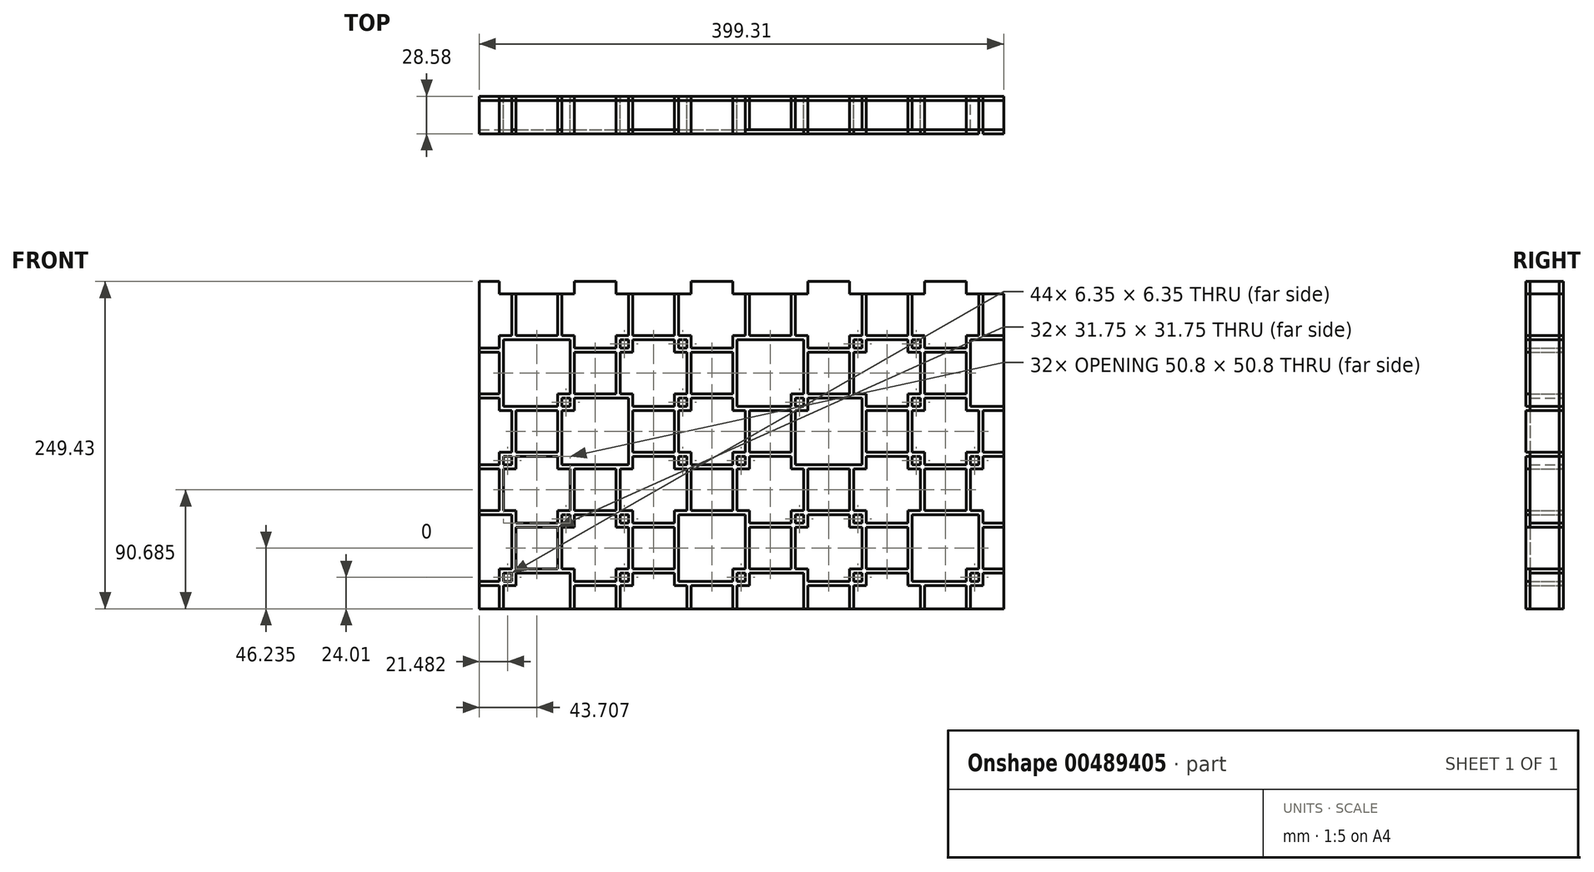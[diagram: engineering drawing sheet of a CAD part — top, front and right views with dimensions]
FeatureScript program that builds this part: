
annotation { "Feature Type Name" : "Feature", "Feature Type Description" : "" }
export const myFeature = defineFeature(function(context is Context, id is Id, definition is map)
    precondition{}
    {
        {
            var Q0;
            Q0=qCreatedBy(makeId("Front.planeOp"),FACE);
            var sketch = newSketch(context, id + "F0", { "sketchPlane" : qUnion([Q0])});
            skLineSegment(sketch, "E0.top", {"start": v(-283.74, 148.71) * mm, "end": v(-268.6, 148.71) * mm});
            skLineSegment(sketch, "E0.right", {"start": v(-259.08, 173.7) * mm, "end": v(-259.08, 158.24) * mm});
            skLineSegment(sketch, "E1.bottom", {"start": v(-265.43, 155.06) * mm, "end": v(-214.63, 155.06) * mm});
            skLineSegment(sketch, "E1.top", {"start": v(-265.43, 104.26) * mm, "end": v(-214.63, 104.26) * mm});
            skLineSegment(sketch, "E1.left", {"start": v(-265.43, 155.06) * mm, "end": v(-265.43, 104.26) * mm});
            skLineSegment(sketch, "E1.right", {"start": v(-214.63, 155.06) * mm, "end": v(-214.63, 104.26) * mm});
            skLineSegment(sketch, "E2.2", {"start": v(-283.74, 145.54) * mm, "end": v(-268.6, 145.54) * mm});
            skLineSegment(sketch, "E2.3", {"start": v(-255.9, 173.7) * mm, "end": v(-255.9, 158.24) * mm});
            skLineSegment(sketch, "E3.0", {"start": v(-268.6, 158.24) * mm, "end": v(-211.46, 158.24) * mm});
            skLineSegment(sketch, "E3.1", {"start": v(-268.6, 158.24) * mm, "end": v(-268.6, 101.09) * mm});
            skLineSegment(sketch, "E3.2", {"start": v(-268.6, 101.09) * mm, "end": v(-211.46, 101.09) * mm});
            skLineSegment(sketch, "E3.3", {"start": v(-211.46, 158.24) * mm, "end": v(-211.46, 101.09) * mm});
            skLineSegment(sketch, "E4.0.1.0", {"start": v(-268.6, 12.19) * mm, "end": v(-224.16, 12.19) * mm});
            skLineSegment(sketch, "E4.0.1.1", {"start": v(-268.6, 69.34) * mm, "end": v(-211.46, 69.34) * mm});
            skLineSegment(sketch, "E4.0.1.2", {"start": v(-265.43, 66.16) * mm, "end": v(-214.63, 66.16) * mm});
            skLineSegment(sketch, "E4.0.1.3", {"start": v(-283.74, 113.79) * mm, "end": v(-268.6, 113.79) * mm});
            skLineSegment(sketch, "E4.0.1.4", {"start": v(-214.63, 66.16) * mm, "end": v(-214.63, 24.89) * mm});
            skLineSegment(sketch, "E4.0.1.5", {"start": v(-265.43, 66.16) * mm, "end": v(-265.43, 15.36) * mm});
            skLineSegment(sketch, "E4.0.1.6", {"start": v(-265.43, 15.36) * mm, "end": v(-224.16, 15.36) * mm});
            skLineSegment(sketch, "E4.0.1.7", {"start": v(-259.08, 101.09) * mm, "end": v(-259.08, 69.34) * mm});
            skLineSegment(sketch, "E4.0.1.9", {"start": v(-283.74, 59.81) * mm, "end": v(-268.6, 59.81) * mm});
            skLineSegment(sketch, "E4.0.1.10", {"start": v(-283.74, 110.61) * mm, "end": v(-268.6, 110.61) * mm});
            skLineSegment(sketch, "E4.0.1.11", {"start": v(-211.46, 69.34) * mm, "end": v(-211.46, 24.89) * mm});
            skLineSegment(sketch, "E4.0.1.13", {"start": v(-268.6, 69.34) * mm, "end": v(-268.6, 12.19) * mm});
            skLineSegment(sketch, "E4.0.1.14", {"start": v(-283.74, 56.64) * mm, "end": v(-268.6, 56.64) * mm});
            skLineSegment(sketch, "E4.0.1.15", {"start": v(-255.9, 101.09) * mm, "end": v(-255.9, 69.34) * mm});
            skLineSegment(sketch, "E4.0.2.0", {"start": v(-255.9, -76.71) * mm, "end": v(-211.46, -76.71) * mm});
            skLineSegment(sketch, "E4.0.2.1", {"start": v(-268.6, -19.56) * mm, "end": v(-224.16, -19.56) * mm});
            skLineSegment(sketch, "E4.0.2.2", {"start": v(-265.43, -22.74) * mm, "end": v(-224.16, -22.74) * mm});
            skLineSegment(sketch, "E4.0.2.4", {"start": v(-214.63, -32.26) * mm, "end": v(-214.63, -73.54) * mm});
            skLineSegment(sketch, "E4.0.2.5", {"start": v(-265.43, -22.74) * mm, "end": v(-265.43, -64.01) * mm});
            skLineSegment(sketch, "E4.0.2.6", {"start": v(-255.9, -73.54) * mm, "end": v(-214.63, -73.54) * mm});
            skLineSegment(sketch, "E4.0.2.7", {"start": v(-259.08, 12.19) * mm, "end": v(-259.08, -29.09) * mm});
            skLineSegment(sketch, "E4.0.2.9", {"start": v(-283.74, -29.09) * mm, "end": v(-259.08, -29.09) * mm});
            skLineSegment(sketch, "E4.0.2.10", {"start": v(-283.74, 21.71) * mm, "end": v(-268.6, 21.71) * mm});
            skLineSegment(sketch, "E4.0.2.11", {"start": v(-211.46, -32.26) * mm, "end": v(-211.46, -76.71) * mm});
            skLineSegment(sketch, "E4.0.2.13", {"start": v(-268.6, -19.56) * mm, "end": v(-268.6, -32.26) * mm});
            skLineSegment(sketch, "E4.0.2.14", {"start": v(-283.74, -32.26) * mm, "end": v(-255.9, -32.26) * mm});
            skLineSegment(sketch, "E4.0.2.15", {"start": v(-255.9, 12.19) * mm, "end": v(-255.9, -32.26) * mm});
            skLineSegment(sketch, "E4.0.3.1", {"start": v(-268.6, -108.46) * mm, "end": v(-211.46, -108.46) * mm});
            skLineSegment(sketch, "E4.0.3.2", {"start": v(-265.43, -111.64) * mm, "end": v(-214.63, -111.64) * mm});
            skLineSegment(sketch, "E4.0.3.3", {"start": v(-283.74, -64.01) * mm, "end": v(-255.9, -64.01) * mm});
            skLineSegment(sketch, "E4.0.3.4", {"start": v(-214.63, -111.64) * mm, "end": v(-214.63, -138.82) * mm});
            skLineSegment(sketch, "E4.0.3.5", {"start": v(-265.43, -111.64) * mm, "end": v(-265.43, -138.82) * mm});
            skLineSegment(sketch, "E4.0.3.7", {"start": v(-259.08, -67.19) * mm, "end": v(-259.08, -108.46) * mm});
            skLineSegment(sketch, "E4.0.3.9", {"start": v(-283.74, -117.99) * mm, "end": v(-268.6, -117.99) * mm});
            skLineSegment(sketch, "E4.0.3.10", {"start": v(-283.74, -67.19) * mm, "end": v(-259.08, -67.19) * mm});
            skLineSegment(sketch, "E4.0.3.11", {"start": v(-211.46, -108.46) * mm, "end": v(-211.46, -138.82) * mm});
            skLineSegment(sketch, "E4.0.3.13", {"start": v(-268.6, -108.46) * mm, "end": v(-268.6, -138.82) * mm});
            skLineSegment(sketch, "E4.0.3.14", {"start": v(-283.74, -121.16) * mm, "end": v(-268.6, -121.16) * mm});
            skLineSegment(sketch, "E4.0.3.15", {"start": v(-255.9, -64.01) * mm, "end": v(-255.9, -108.46) * mm});
            skLineSegment(sketch, "E4.1.0.0", {"start": v(-179.7, 101.09) * mm, "end": v(-122.56, 101.09) * mm});
            skLineSegment(sketch, "E4.1.0.1", {"start": v(-179.7, 158.24) * mm, "end": v(-170.18, 158.24) * mm});
            skLineSegment(sketch, "E4.1.0.2", {"start": v(-176.53, 155.06) * mm, "end": v(-125.73, 155.06) * mm});
            skLineSegment(sketch, "E4.1.0.4", {"start": v(-125.73, 155.06) * mm, "end": v(-125.73, 104.26) * mm});
            skLineSegment(sketch, "E4.1.0.5", {"start": v(-176.53, 155.06) * mm, "end": v(-176.53, 148.71) * mm});
            skLineSegment(sketch, "E4.1.0.6", {"start": v(-176.53, 104.26) * mm, "end": v(-125.73, 104.26) * mm});
            skLineSegment(sketch, "E4.1.0.7", {"start": v(-170.18, 173.7) * mm, "end": v(-170.18, 158.24) * mm});
            skLineSegment(sketch, "E4.1.0.8", {"start": v(-220.98, 173.7) * mm, "end": v(-220.98, 158.24) * mm});
            skLineSegment(sketch, "E4.1.0.9", {"start": v(-211.46, 148.71) * mm, "end": v(-179.7, 148.71) * mm});
            skLineSegment(sketch, "E4.1.0.11", {"start": v(-122.56, 158.24) * mm, "end": v(-122.56, 101.09) * mm});
            skLineSegment(sketch, "E4.1.0.12", {"start": v(-224.16, 173.7) * mm, "end": v(-224.16, 158.24) * mm});
            skLineSegment(sketch, "E4.1.0.13", {"start": v(-179.7, 158.24) * mm, "end": v(-179.7, 148.71) * mm});
            skLineSegment(sketch, "E4.1.0.14", {"start": v(-211.46, 145.54) * mm, "end": v(-179.7, 145.54) * mm});
            skLineSegment(sketch, "E4.1.0.15", {"start": v(-167, 173.7) * mm, "end": v(-167, 158.24) * mm});
            skLineSegment(sketch, "E4.1.1.0", {"start": v(-167, 12.19) * mm, "end": v(-122.56, 12.19) * mm});
            skLineSegment(sketch, "E4.1.1.1", {"start": v(-179.7, 69.34) * mm, "end": v(-122.56, 69.34) * mm});
            skLineSegment(sketch, "E4.1.1.2", {"start": v(-176.53, 66.16) * mm, "end": v(-125.73, 66.16) * mm});
            skLineSegment(sketch, "E4.1.1.3", {"start": v(-211.46, 113.79) * mm, "end": v(-179.7, 113.79) * mm});
            skLineSegment(sketch, "E4.1.1.4", {"start": v(-125.73, 66.16) * mm, "end": v(-125.73, 15.36) * mm});
            skLineSegment(sketch, "E4.1.1.5", {"start": v(-176.53, 66.16) * mm, "end": v(-176.53, 24.89) * mm});
            skLineSegment(sketch, "E4.1.1.6", {"start": v(-167, 15.36) * mm, "end": v(-125.73, 15.36) * mm});
            skLineSegment(sketch, "E4.1.1.7", {"start": v(-170.18, 101.09) * mm, "end": v(-170.18, 59.81) * mm});
            skLineSegment(sketch, "E4.1.1.8", {"start": v(-220.98, 101.09) * mm, "end": v(-220.98, 69.34) * mm});
            skLineSegment(sketch, "E4.1.1.9", {"start": v(-211.46, 59.81) * mm, "end": v(-170.18, 59.81) * mm});
            skLineSegment(sketch, "E4.1.1.10", {"start": v(-211.46, 110.61) * mm, "end": v(-179.7, 110.61) * mm});
            skLineSegment(sketch, "E4.1.1.11", {"start": v(-122.56, 69.34) * mm, "end": v(-122.56, 12.19) * mm});
            skLineSegment(sketch, "E4.1.1.12", {"start": v(-224.16, 101.09) * mm, "end": v(-224.16, 69.34) * mm});
            skLineSegment(sketch, "E4.1.1.13", {"start": v(-179.7, 69.34) * mm, "end": v(-179.7, 24.89) * mm});
            skLineSegment(sketch, "E4.1.1.14", {"start": v(-211.46, 56.64) * mm, "end": v(-167, 56.64) * mm});
            skLineSegment(sketch, "E4.1.1.15", {"start": v(-167, 101.09) * mm, "end": v(-167, 56.64) * mm});
            skLineSegment(sketch, "E4.1.2.0", {"start": v(-179.7, -76.71) * mm, "end": v(-167, -76.71) * mm});
            skLineSegment(sketch, "E4.1.2.1", {"start": v(-167, -19.56) * mm, "end": v(-122.56, -19.56) * mm});
            skLineSegment(sketch, "E4.1.2.2", {"start": v(-167, -22.74) * mm, "end": v(-125.73, -22.74) * mm});
            skLineSegment(sketch, "E4.1.2.3", {"start": v(-224.16, 24.89) * mm, "end": v(-167, 24.89) * mm});
            skLineSegment(sketch, "E4.1.2.4", {"start": v(-125.73, -22.74) * mm, "end": v(-125.73, -64.01) * mm});
            skLineSegment(sketch, "E4.1.2.6", {"start": v(-176.53, -73.54) * mm, "end": v(-167, -73.54) * mm});
            skLineSegment(sketch, "E4.1.2.7", {"start": v(-170.18, 21.71) * mm, "end": v(-170.18, -29.09) * mm});
            skLineSegment(sketch, "E4.1.2.8", {"start": v(-220.98, 21.71) * mm, "end": v(-220.98, -29.09) * mm});
            skLineSegment(sketch, "E4.1.2.9", {"start": v(-220.98, -29.09) * mm, "end": v(-170.18, -29.09) * mm});
            skLineSegment(sketch, "E4.1.2.10", {"start": v(-220.98, 21.71) * mm, "end": v(-170.18, 21.71) * mm});
            skLineSegment(sketch, "E4.1.2.11", {"start": v(-122.56, -19.56) * mm, "end": v(-122.56, -64.01) * mm});
            skLineSegment(sketch, "E4.1.2.12", {"start": v(-224.16, 24.89) * mm, "end": v(-224.16, -32.26) * mm});
            skLineSegment(sketch, "E4.1.2.13", {"start": v(-179.7, -32.26) * mm, "end": v(-179.7, -76.71) * mm});
            skLineSegment(sketch, "E4.1.2.14", {"start": v(-224.16, -32.26) * mm, "end": v(-167, -32.26) * mm});
            skLineSegment(sketch, "E4.1.2.15", {"start": v(-167, 24.89) * mm, "end": v(-167, -32.26) * mm});
            skLineSegment(sketch, "E4.1.3.1", {"start": v(-179.7, -108.46) * mm, "end": v(-135.26, -108.46) * mm});
            skLineSegment(sketch, "E4.1.3.2", {"start": v(-176.53, -111.64) * mm, "end": v(-135.26, -111.64) * mm});
            skLineSegment(sketch, "E4.1.3.3", {"start": v(-224.16, -64.01) * mm, "end": v(-167, -64.01) * mm});
            skLineSegment(sketch, "E4.1.3.4", {"start": v(-125.73, -121.16) * mm, "end": v(-125.73, -138.82) * mm});
            skLineSegment(sketch, "E4.1.3.5", {"start": v(-176.53, -111.64) * mm, "end": v(-176.53, -138.82) * mm});
            skLineSegment(sketch, "E4.1.3.7", {"start": v(-170.18, -67.19) * mm, "end": v(-170.18, -117.99) * mm});
            skLineSegment(sketch, "E4.1.3.8", {"start": v(-220.98, -67.19) * mm, "end": v(-220.98, -108.46) * mm});
            skLineSegment(sketch, "E4.1.3.9", {"start": v(-211.46, -117.99) * mm, "end": v(-170.18, -117.99) * mm});
            skLineSegment(sketch, "E4.1.3.10", {"start": v(-220.98, -67.19) * mm, "end": v(-170.18, -67.19) * mm});
            skLineSegment(sketch, "E4.1.3.11", {"start": v(-122.56, -121.16) * mm, "end": v(-122.56, -138.82) * mm});
            skLineSegment(sketch, "E4.1.3.12", {"start": v(-224.16, -64.01) * mm, "end": v(-224.16, -108.46) * mm});
            skLineSegment(sketch, "E4.1.3.13", {"start": v(-179.7, -108.46) * mm, "end": v(-179.7, -138.82) * mm});
            skLineSegment(sketch, "E4.1.3.14", {"start": v(-211.46, -121.16) * mm, "end": v(-167, -121.16) * mm});
            skLineSegment(sketch, "E4.1.3.15", {"start": v(-167, -64.01) * mm, "end": v(-167, -121.16) * mm});
            skLineSegment(sketch, "E4.2.0.0", {"start": v(-90.8, 101.09) * mm, "end": v(-33.66, 101.09) * mm});
            skLineSegment(sketch, "E4.2.0.1", {"start": v(-90.8, 158.24) * mm, "end": v(-33.66, 158.24) * mm});
            skLineSegment(sketch, "E4.2.0.2", {"start": v(-87.63, 155.06) * mm, "end": v(-36.83, 155.06) * mm});
            skLineSegment(sketch, "E4.2.0.4", {"start": v(-36.83, 155.06) * mm, "end": v(-36.83, 104.26) * mm});
            skLineSegment(sketch, "E4.2.0.5", {"start": v(-87.63, 155.06) * mm, "end": v(-87.63, 104.26) * mm});
            skLineSegment(sketch, "E4.2.0.6", {"start": v(-87.63, 104.26) * mm, "end": v(-36.83, 104.26) * mm});
            skLineSegment(sketch, "E4.2.0.7", {"start": v(-81.28, 173.7) * mm, "end": v(-81.28, 158.24) * mm});
            skLineSegment(sketch, "E4.2.0.8", {"start": v(-132.08, 173.7) * mm, "end": v(-132.08, 158.24) * mm});
            skLineSegment(sketch, "E4.2.0.9", {"start": v(-122.56, 148.71) * mm, "end": v(-90.8, 148.71) * mm});
            skLineSegment(sketch, "E4.2.0.11", {"start": v(-33.66, 158.24) * mm, "end": v(-33.66, 101.09) * mm});
            skLineSegment(sketch, "E4.2.0.12", {"start": v(-135.26, 173.7) * mm, "end": v(-135.26, 158.24) * mm});
            skLineSegment(sketch, "E4.2.0.13", {"start": v(-90.8, 158.24) * mm, "end": v(-90.8, 101.09) * mm});
            skLineSegment(sketch, "E4.2.0.14", {"start": v(-122.56, 145.54) * mm, "end": v(-90.8, 145.54) * mm});
            skLineSegment(sketch, "E4.2.0.15", {"start": v(-78.1, 173.7) * mm, "end": v(-78.1, 158.24) * mm});
            skLineSegment(sketch, "E4.2.1.0", {"start": v(-90.8, 12.19) * mm, "end": v(-46.36, 12.19) * mm});
            skLineSegment(sketch, "E4.2.1.1", {"start": v(-90.8, 69.34) * mm, "end": v(-33.66, 69.34) * mm});
            skLineSegment(sketch, "E4.2.1.2", {"start": v(-87.63, 66.16) * mm, "end": v(-36.83, 66.16) * mm});
            skLineSegment(sketch, "E4.2.1.3", {"start": v(-122.56, 113.79) * mm, "end": v(-90.8, 113.79) * mm});
            skLineSegment(sketch, "E4.2.1.4", {"start": v(-36.83, 66.16) * mm, "end": v(-36.83, 24.89) * mm});
            skLineSegment(sketch, "E4.2.1.5", {"start": v(-87.63, 66.16) * mm, "end": v(-87.63, 15.36) * mm});
            skLineSegment(sketch, "E4.2.1.6", {"start": v(-87.63, 15.36) * mm, "end": v(-46.36, 15.36) * mm});
            skLineSegment(sketch, "E4.2.1.7", {"start": v(-81.28, 101.09) * mm, "end": v(-81.28, 69.34) * mm});
            skLineSegment(sketch, "E4.2.1.8", {"start": v(-132.08, 101.09) * mm, "end": v(-132.08, 59.81) * mm});
            skLineSegment(sketch, "E4.2.1.9", {"start": v(-132.08, 59.81) * mm, "end": v(-90.8, 59.81) * mm});
            skLineSegment(sketch, "E4.2.1.10", {"start": v(-122.56, 110.61) * mm, "end": v(-90.8, 110.61) * mm});
            skLineSegment(sketch, "E4.2.1.11", {"start": v(-33.66, 69.34) * mm, "end": v(-33.66, 24.89) * mm});
            skLineSegment(sketch, "E4.2.1.12", {"start": v(-135.26, 101.09) * mm, "end": v(-135.26, 56.64) * mm});
            skLineSegment(sketch, "E4.2.1.13", {"start": v(-90.8, 69.34) * mm, "end": v(-90.8, 12.19) * mm});
            skLineSegment(sketch, "E4.2.1.14", {"start": v(-135.26, 56.64) * mm, "end": v(-90.8, 56.64) * mm});
            skLineSegment(sketch, "E4.2.1.15", {"start": v(-78.1, 101.09) * mm, "end": v(-78.1, 69.34) * mm});
            skLineSegment(sketch, "E4.2.2.1", {"start": v(-90.8, -19.56) * mm, "end": v(-46.36, -19.56) * mm});
            skLineSegment(sketch, "E4.2.2.2", {"start": v(-87.63, -22.74) * mm, "end": v(-46.36, -22.74) * mm});
            skLineSegment(sketch, "E4.2.2.3", {"start": v(-135.26, 24.89) * mm, "end": v(-90.8, 24.89) * mm});
            skLineSegment(sketch, "E4.2.2.5", {"start": v(-87.63, -22.74) * mm, "end": v(-87.63, -64.01) * mm});
            skLineSegment(sketch, "E4.2.2.7", {"start": v(-81.28, 12.19) * mm, "end": v(-81.28, -29.09) * mm});
            skLineSegment(sketch, "E4.2.2.8", {"start": v(-132.08, 21.71) * mm, "end": v(-132.08, -29.09) * mm});
            skLineSegment(sketch, "E4.2.2.9", {"start": v(-132.08, -29.09) * mm, "end": v(-81.28, -29.09) * mm});
            skLineSegment(sketch, "E4.2.2.10", {"start": v(-132.08, 21.71) * mm, "end": v(-90.8, 21.71) * mm});
            skLineSegment(sketch, "E4.2.2.12", {"start": v(-135.26, 24.89) * mm, "end": v(-135.26, -32.26) * mm});
            skLineSegment(sketch, "E4.2.2.13", {"start": v(-90.8, -19.56) * mm, "end": v(-90.8, -64.01) * mm});
            skLineSegment(sketch, "E4.2.2.14", {"start": v(-135.26, -32.26) * mm, "end": v(-78.1, -32.26) * mm});
            skLineSegment(sketch, "E4.2.2.15", {"start": v(-78.1, 12.19) * mm, "end": v(-78.1, -32.26) * mm});
            skLineSegment(sketch, "E4.2.3.1", {"start": v(-90.8, -108.46) * mm, "end": v(-33.66, -108.46) * mm});
            skLineSegment(sketch, "E4.2.3.2", {"start": v(-87.63, -111.64) * mm, "end": v(-36.83, -111.64) * mm});
            skLineSegment(sketch, "E4.2.3.3", {"start": v(-135.26, -64.01) * mm, "end": v(-78.1, -64.01) * mm});
            skLineSegment(sketch, "E4.2.3.4", {"start": v(-36.83, -111.64) * mm, "end": v(-36.83, -138.82) * mm});
            skLineSegment(sketch, "E4.2.3.5", {"start": v(-87.63, -111.64) * mm, "end": v(-87.63, -138.82) * mm});
            skLineSegment(sketch, "E4.2.3.7", {"start": v(-81.28, -67.19) * mm, "end": v(-81.28, -108.46) * mm});
            skLineSegment(sketch, "E4.2.3.8", {"start": v(-132.08, -67.19) * mm, "end": v(-132.08, -117.99) * mm});
            skLineSegment(sketch, "E4.2.3.9", {"start": v(-132.08, -117.99) * mm, "end": v(-90.8, -117.99) * mm});
            skLineSegment(sketch, "E4.2.3.10", {"start": v(-132.08, -67.19) * mm, "end": v(-81.28, -67.19) * mm});
            skLineSegment(sketch, "E4.2.3.11", {"start": v(-33.66, -108.46) * mm, "end": v(-33.66, -138.82) * mm});
            skLineSegment(sketch, "E4.2.3.12", {"start": v(-135.26, -64.01) * mm, "end": v(-135.26, -121.16) * mm});
            skLineSegment(sketch, "E4.2.3.13", {"start": v(-90.8, -108.46) * mm, "end": v(-90.8, -138.82) * mm});
            skLineSegment(sketch, "E4.2.3.14", {"start": v(-135.26, -121.16) * mm, "end": v(-90.8, -121.16) * mm});
            skLineSegment(sketch, "E4.2.3.15", {"start": v(-78.1, -64.01) * mm, "end": v(-78.1, -108.46) * mm});
            skLineSegment(sketch, "E4.3.0.0", {"start": v(-1.9, 101.09) * mm, "end": v(55.24, 101.09) * mm});
            skLineSegment(sketch, "E4.3.0.1", {"start": v(-1.9, 158.24) * mm, "end": v(55.24, 158.24) * mm});
            skLineSegment(sketch, "E4.3.0.2", {"start": v(1.27, 155.06) * mm, "end": v(52.07, 155.06) * mm});
            skLineSegment(sketch, "E4.3.0.4", {"start": v(52.07, 155.06) * mm, "end": v(52.07, 104.26) * mm});
            skLineSegment(sketch, "E4.3.0.5", {"start": v(1.27, 155.06) * mm, "end": v(1.27, 104.26) * mm});
            skLineSegment(sketch, "E4.3.0.6", {"start": v(1.27, 104.26) * mm, "end": v(52.07, 104.26) * mm});
            skLineSegment(sketch, "E4.3.0.7", {"start": v(7.62, 173.7) * mm, "end": v(7.62, 158.24) * mm});
            skLineSegment(sketch, "E4.3.0.8", {"start": v(-43.18, 173.7) * mm, "end": v(-43.18, 158.24) * mm});
            skLineSegment(sketch, "E4.3.0.9", {"start": v(-33.66, 148.71) * mm, "end": v(-1.9, 148.71) * mm});
            skLineSegment(sketch, "E4.3.0.11", {"start": v(55.24, 158.24) * mm, "end": v(55.24, 101.09) * mm});
            skLineSegment(sketch, "E4.3.0.12", {"start": v(-46.36, 173.7) * mm, "end": v(-46.36, 158.24) * mm});
            skLineSegment(sketch, "E4.3.0.13", {"start": v(-1.9, 158.24) * mm, "end": v(-1.9, 101.09) * mm});
            skLineSegment(sketch, "E4.3.0.14", {"start": v(-33.66, 145.54) * mm, "end": v(-1.9, 145.54) * mm});
            skLineSegment(sketch, "E4.3.0.15", {"start": v(10.8, 173.7) * mm, "end": v(10.8, 158.24) * mm});
            skLineSegment(sketch, "E4.3.1.0", {"start": v(10.8, 12.19) * mm, "end": v(55.24, 12.19) * mm});
            skLineSegment(sketch, "E4.3.1.1", {"start": v(-1.9, 69.34) * mm, "end": v(55.24, 69.34) * mm});
            skLineSegment(sketch, "E4.3.1.2", {"start": v(1.27, 66.16) * mm, "end": v(52.07, 66.16) * mm});
            skLineSegment(sketch, "E4.3.1.3", {"start": v(-33.66, 113.79) * mm, "end": v(-1.9, 113.79) * mm});
            skLineSegment(sketch, "E4.3.1.4", {"start": v(52.07, 66.16) * mm, "end": v(52.07, 15.36) * mm});
            skLineSegment(sketch, "E4.3.1.5", {"start": v(1.27, 66.16) * mm, "end": v(1.27, 24.89) * mm});
            skLineSegment(sketch, "E4.3.1.6", {"start": v(10.8, 15.36) * mm, "end": v(52.07, 15.36) * mm});
            skLineSegment(sketch, "E4.3.1.8", {"start": v(-43.18, 101.09) * mm, "end": v(-43.18, 69.34) * mm});
            skLineSegment(sketch, "E4.3.1.10", {"start": v(-33.66, 110.61) * mm, "end": v(-1.9, 110.61) * mm});
            skLineSegment(sketch, "E4.3.1.11", {"start": v(55.24, 69.34) * mm, "end": v(55.24, 12.19) * mm});
            skLineSegment(sketch, "E4.3.1.12", {"start": v(-46.36, 101.09) * mm, "end": v(-46.36, 69.34) * mm});
            skLineSegment(sketch, "E4.3.1.13", {"start": v(-1.9, 69.34) * mm, "end": v(-1.9, 24.89) * mm});
            skLineSegment(sketch, "E4.3.2.0", {"start": v(-1.9, -76.71) * mm, "end": v(42.54, -76.71) * mm});
            skLineSegment(sketch, "E4.3.2.3", {"start": v(-46.36, 24.89) * mm, "end": v(-36.83, 24.89) * mm});
            skLineSegment(sketch, "E4.3.2.4", {"start": v(52.07, -22.74) * mm, "end": v(52.07, -64.01) * mm});
            skLineSegment(sketch, "E4.3.2.5", {"start": v(1.27, -32.26) * mm, "end": v(1.27, -73.54) * mm});
            skLineSegment(sketch, "E4.3.2.6", {"start": v(1.27, -73.54) * mm, "end": v(10.8, -73.54) * mm});
            skLineSegment(sketch, "E4.3.2.7", {"start": v(7.62, 21.71) * mm, "end": v(7.62, -29.09) * mm});
            skLineSegment(sketch, "E4.3.2.8", {"start": v(-43.18, 21.71) * mm, "end": v(-43.18, -29.09) * mm});
            skLineSegment(sketch, "E4.3.2.9", {"start": v(-43.18, -29.09) * mm, "end": v(7.62, -29.09) * mm});
            skLineSegment(sketch, "E4.3.2.10", {"start": v(-43.18, 21.71) * mm, "end": v(-36.83, 21.71) * mm});
            skLineSegment(sketch, "E4.3.2.11", {"start": v(55.24, -19.56) * mm, "end": v(55.24, -64.01) * mm});
            skLineSegment(sketch, "E4.3.2.12", {"start": v(-46.36, 24.89) * mm, "end": v(-46.36, -32.26) * mm});
            skLineSegment(sketch, "E4.3.2.13", {"start": v(-1.9, -32.26) * mm, "end": v(-1.9, -76.71) * mm});
            skLineSegment(sketch, "E4.3.2.14", {"start": v(-46.36, -32.26) * mm, "end": v(10.8, -32.26) * mm});
            skLineSegment(sketch, "E4.3.2.15", {"start": v(10.8, 24.89) * mm, "end": v(10.8, -32.26) * mm});
            skLineSegment(sketch, "E4.3.3.1", {"start": v(-1.9, -108.46) * mm, "end": v(42.54, -108.46) * mm});
            skLineSegment(sketch, "E4.3.3.2", {"start": v(1.27, -111.64) * mm, "end": v(10.8, -111.64) * mm});
            skLineSegment(sketch, "E4.3.3.3", {"start": v(-46.36, -64.01) * mm, "end": v(10.8, -64.01) * mm});
            skLineSegment(sketch, "E4.3.3.4", {"start": v(52.07, -121.16) * mm, "end": v(52.07, -138.82) * mm});
            skLineSegment(sketch, "E4.3.3.5", {"start": v(1.27, -111.64) * mm, "end": v(1.27, -138.82) * mm});
            skLineSegment(sketch, "E4.3.3.7", {"start": v(7.62, -67.19) * mm, "end": v(7.62, -117.99) * mm});
            skLineSegment(sketch, "E4.3.3.8", {"start": v(-43.18, -67.19) * mm, "end": v(-43.18, -108.46) * mm});
            skLineSegment(sketch, "E4.3.3.10", {"start": v(-43.18, -67.19) * mm, "end": v(7.62, -67.19) * mm});
            skLineSegment(sketch, "E4.3.3.11", {"start": v(55.24, -121.16) * mm, "end": v(55.24, -138.82) * mm});
            skLineSegment(sketch, "E4.3.3.12", {"start": v(-46.36, -64.01) * mm, "end": v(-46.36, -108.46) * mm});
            skLineSegment(sketch, "E4.3.3.13", {"start": v(-1.9, -108.46) * mm, "end": v(-1.9, -138.82) * mm});
            skLineSegment(sketch, "E4.3.3.15", {"start": v(10.8, -64.01) * mm, "end": v(10.8, -121.16) * mm});
            skLineSegment(sketch, "E4.4.0.0", {"start": v(87, 101.09) * mm, "end": v(115.57, 101.09) * mm});
            skLineSegment(sketch, "E4.4.0.1", {"start": v(87, 158.24) * mm, "end": v(115.57, 158.24) * mm});
            skLineSegment(sketch, "E4.4.0.2", {"start": v(90.17, 155.06) * mm, "end": v(115.57, 155.06) * mm});
            skLineSegment(sketch, "E4.4.0.5", {"start": v(90.17, 155.06) * mm, "end": v(90.17, 104.26) * mm});
            skLineSegment(sketch, "E4.4.0.6", {"start": v(90.17, 104.26) * mm, "end": v(115.57, 104.26) * mm});
            skLineSegment(sketch, "E4.4.0.7", {"start": v(96.52, 173.7) * mm, "end": v(96.52, 148.71) * mm});
            skLineSegment(sketch, "E4.4.0.8", {"start": v(45.72, 173.7) * mm, "end": v(45.72, 158.24) * mm});
            skLineSegment(sketch, "E4.4.0.9", {"start": v(55.24, 148.71) * mm, "end": v(96.52, 148.71) * mm});
            skLineSegment(sketch, "E4.4.0.12", {"start": v(42.54, 173.7) * mm, "end": v(42.54, 158.24) * mm});
            skLineSegment(sketch, "E4.4.0.13", {"start": v(87, 158.24) * mm, "end": v(87, 101.09) * mm});
            skLineSegment(sketch, "E4.4.0.14", {"start": v(55.24, 145.54) * mm, "end": v(99.7, 145.54) * mm});
            skLineSegment(sketch, "E4.4.0.15", {"start": v(99.7, 173.7) * mm, "end": v(99.7, 145.54) * mm});
            skLineSegment(sketch, "E4.4.1.0", {"start": v(87, 12.19) * mm, "end": v(115.57, 12.19) * mm});
            skLineSegment(sketch, "E4.4.1.1", {"start": v(87, 69.34) * mm, "end": v(115.57, 69.34) * mm});
            skLineSegment(sketch, "E4.4.1.2", {"start": v(90.17, 66.16) * mm, "end": v(115.57, 66.16) * mm});
            skLineSegment(sketch, "E4.4.1.3", {"start": v(55.24, 113.79) * mm, "end": v(99.7, 113.79) * mm});
            skLineSegment(sketch, "E4.4.1.5", {"start": v(90.17, 66.16) * mm, "end": v(90.17, 15.36) * mm});
            skLineSegment(sketch, "E4.4.1.6", {"start": v(90.17, 15.36) * mm, "end": v(115.57, 15.36) * mm});
            skLineSegment(sketch, "E4.4.1.7", {"start": v(96.52, 110.61) * mm, "end": v(96.52, 69.34) * mm});
            skLineSegment(sketch, "E4.4.1.8", {"start": v(45.72, 101.09) * mm, "end": v(45.72, 59.81) * mm});
            skLineSegment(sketch, "E4.4.1.9", {"start": v(45.72, 59.81) * mm, "end": v(87, 59.81) * mm});
            skLineSegment(sketch, "E4.4.1.10", {"start": v(55.24, 110.61) * mm, "end": v(96.52, 110.61) * mm});
            skLineSegment(sketch, "E4.4.1.12", {"start": v(42.54, 101.09) * mm, "end": v(42.54, 56.64) * mm});
            skLineSegment(sketch, "E4.4.1.13", {"start": v(87, 69.34) * mm, "end": v(87, 12.19) * mm});
            skLineSegment(sketch, "E4.4.1.14", {"start": v(42.54, 56.64) * mm, "end": v(87, 56.64) * mm});
            skLineSegment(sketch, "E4.4.1.15", {"start": v(99.7, 113.79) * mm, "end": v(99.7, 69.34) * mm});
            skLineSegment(sketch, "E4.4.2.1", {"start": v(87, -19.56) * mm, "end": v(115.57, -19.56) * mm});
            skLineSegment(sketch, "E4.4.2.2", {"start": v(90.17, -22.74) * mm, "end": v(115.57, -22.74) * mm});
            skLineSegment(sketch, "E4.4.2.3", {"start": v(42.54, 24.89) * mm, "end": v(87, 24.89) * mm});
            skLineSegment(sketch, "E4.4.2.5", {"start": v(90.17, -22.74) * mm, "end": v(90.17, -32.26) * mm});
            skLineSegment(sketch, "E4.4.2.7", {"start": v(96.52, 12.19) * mm, "end": v(96.52, -29.09) * mm});
            skLineSegment(sketch, "E4.4.2.8", {"start": v(45.72, 21.71) * mm, "end": v(45.72, -29.09) * mm});
            skLineSegment(sketch, "E4.4.2.9", {"start": v(45.72, -29.09) * mm, "end": v(96.52, -29.09) * mm});
            skLineSegment(sketch, "E4.4.2.10", {"start": v(45.72, 21.71) * mm, "end": v(87, 21.71) * mm});
            skLineSegment(sketch, "E4.4.2.12", {"start": v(42.54, 24.89) * mm, "end": v(42.54, -32.26) * mm});
            skLineSegment(sketch, "E4.4.2.13", {"start": v(87, -19.56) * mm, "end": v(87, -64.01) * mm});
            skLineSegment(sketch, "E4.4.2.14", {"start": v(42.54, -32.26) * mm, "end": v(99.7, -32.26) * mm});
            skLineSegment(sketch, "E4.4.3.1", {"start": v(87, -108.46) * mm, "end": v(115.57, -108.46) * mm});
            skLineSegment(sketch, "E4.4.3.2", {"start": v(90.17, -111.64) * mm, "end": v(115.57, -111.64) * mm});
            skLineSegment(sketch, "E4.4.3.3", {"start": v(42.54, -64.01) * mm, "end": v(99.7, -64.01) * mm});
            skLineSegment(sketch, "E4.4.3.5", {"start": v(90.17, -111.64) * mm, "end": v(90.17, -138.82) * mm});
            skLineSegment(sketch, "E4.4.3.7", {"start": v(96.52, -67.19) * mm, "end": v(96.52, -108.46) * mm});
            skLineSegment(sketch, "E4.4.3.8", {"start": v(45.72, -67.19) * mm, "end": v(45.72, -117.99) * mm});
            skLineSegment(sketch, "E4.4.3.9", {"start": v(45.72, -117.99) * mm, "end": v(87, -117.99) * mm});
            skLineSegment(sketch, "E4.4.3.10", {"start": v(45.72, -67.19) * mm, "end": v(96.52, -67.19) * mm});
            skLineSegment(sketch, "E4.4.3.12", {"start": v(42.54, -64.01) * mm, "end": v(42.54, -121.16) * mm});
            skLineSegment(sketch, "E4.4.3.13", {"start": v(87, -108.46) * mm, "end": v(87, -138.82) * mm});
            skLineSegment(sketch, "E4.4.3.14", {"start": v(42.54, -121.16) * mm, "end": v(87, -121.16) * mm});
            skLineSegment(sketch, "E4.4.3.15", {"start": v(99.7, -64.01) * mm, "end": v(99.7, -108.46) * mm});
            skLineSegment(sketch, "E4.direction1", {"start": v(-268.6, 101.09) * mm, "end": v(-179.7, 101.09) * mm, "construction": true});
            skLineSegment(sketch, "E4.direction2", {"start": v(-268.6, 101.09) * mm, "end": v(-268.6, 12.19) * mm, "construction": true});
            skPoint(sketch, "E5.oppositeSnap0", {"position": v(115.57, -111.64) * mm});
            skLineSegment(sketch, "E5.bottom", {"start": v(-283.74, 173.7) * mm, "end": v(115.57, 173.7) * mm});
            skLineSegment(sketch, "E5.top", {"start": v(-283.74, -138.82) * mm, "end": v(115.57, -138.82) * mm});
            skLineSegment(sketch, "E5.left", {"start": v(-283.74, 173.7) * mm, "end": v(-283.74, -138.82) * mm});
            skLineSegment(sketch, "E5.right", {"start": v(115.57, 173.7) * mm, "end": v(115.57, -138.82) * mm});
            skPoint(sketch, "E6.orphan", {"position": v(140.97, -111.64) * mm});
            skLineSegment(sketch, "E7.trimOffspring", {"start": v(-259.08, 155.06) * mm, "end": v(-259.08, 148.71) * mm});
            skLineSegment(sketch, "E8.trimOffspring", {"start": v(-255.9, 155.06) * mm, "end": v(-255.9, 145.54) * mm});
            skLineSegment(sketch, "E9.trimOffspring", {"start": v(-265.43, 148.71) * mm, "end": v(-259.08, 148.71) * mm});
            skLineSegment(sketch, "E10.trimOffspring", {"start": v(-265.43, 145.54) * mm, "end": v(-255.9, 145.54) * mm});
            skLineSegment(sketch, "E11.trimOffspring", {"start": v(-176.53, 148.71) * mm, "end": v(-170.18, 148.71) * mm});
            skLineSegment(sketch, "E12.trimOffspring", {"start": v(-176.53, 145.54) * mm, "end": v(-167, 145.54) * mm});
            skLineSegment(sketch, "E13.trimOffspring", {"start": v(-167, 158.24) * mm, "end": v(-122.56, 158.24) * mm});
            skLineSegment(sketch, "E14.trimOffspring", {"start": v(-170.18, 155.06) * mm, "end": v(-170.18, 148.71) * mm});
            skLineSegment(sketch, "E15.trimOffspring", {"start": v(-167, 155.06) * mm, "end": v(-167, 145.54) * mm});
            skLineSegment(sketch, "E16.trimOffspring", {"start": v(-176.53, 145.54) * mm, "end": v(-176.53, 104.26) * mm});
            skLineSegment(sketch, "E17.trimOffspring", {"start": v(-179.7, 145.54) * mm, "end": v(-179.7, 101.09) * mm});
            skLineSegment(sketch, "E18", {"start": v(-179.7, 148.71) * mm, "end": v(-179.7, 145.54) * mm});
            skLineSegment(sketch, "E19", {"start": v(-176.53, 148.71) * mm, "end": v(-176.53, 145.54) * mm});
            skLineSegment(sketch, "E20", {"start": v(-170.18, 158.24) * mm, "end": v(-167, 158.24) * mm});
            skLineSegment(sketch, "E21.trimOffspring", {"start": v(-78.1, 155.06) * mm, "end": v(-78.1, 145.54) * mm});
            skLineSegment(sketch, "E22.trimOffspring", {"start": v(-81.28, 155.06) * mm, "end": v(-81.28, 148.71) * mm});
            skLineSegment(sketch, "E23.trimOffspring", {"start": v(-87.63, 148.71) * mm, "end": v(-81.28, 148.71) * mm});
            skLineSegment(sketch, "E24.trimOffspring", {"start": v(-87.63, 145.54) * mm, "end": v(-78.1, 145.54) * mm});
            skLineSegment(sketch, "E25.trimOffspring", {"start": v(7.62, 155.06) * mm, "end": v(7.62, 148.71) * mm});
            skLineSegment(sketch, "E26.trimOffspring", {"start": v(10.8, 155.06) * mm, "end": v(10.8, 145.54) * mm});
            skLineSegment(sketch, "E27.trimOffspring", {"start": v(1.27, 148.71) * mm, "end": v(7.62, 148.71) * mm});
            skLineSegment(sketch, "E28.trimOffspring", {"start": v(1.27, 145.54) * mm, "end": v(10.8, 145.54) * mm});
            skLineSegment(sketch, "E29.trimOffspring", {"start": v(10.8, 101.09) * mm, "end": v(10.8, 56.64) * mm});
            skLineSegment(sketch, "E30.trimOffspring", {"start": v(7.62, 101.09) * mm, "end": v(7.62, 59.81) * mm});
            skLineSegment(sketch, "E31.trimOffspring", {"start": v(-220.98, 15.36) * mm, "end": v(-214.63, 15.36) * mm});
            skLineSegment(sketch, "E32.trimOffspring", {"start": v(-220.98, 12.19) * mm, "end": v(-211.46, 12.19) * mm});
            skLineSegment(sketch, "E33.trimOffspring", {"start": v(-214.63, 21.71) * mm, "end": v(-214.63, 15.36) * mm});
            skLineSegment(sketch, "E34.trimOffspring", {"start": v(-211.46, 21.71) * mm, "end": v(-211.46, 12.19) * mm});
            skLineSegment(sketch, "E35.trimOffspring", {"start": v(-176.53, -32.26) * mm, "end": v(-176.53, -73.54) * mm});
            skLineSegment(sketch, "E36.trimOffspring", {"start": v(-43.18, 15.36) * mm, "end": v(-36.83, 15.36) * mm});
            skLineSegment(sketch, "E37.trimOffspring", {"start": v(-43.18, 12.19) * mm, "end": v(-33.66, 12.19) * mm});
            skLineSegment(sketch, "E38.trimOffspring", {"start": v(-33.66, 21.71) * mm, "end": v(7.62, 21.71) * mm});
            skLineSegment(sketch, "E39.trimOffspring", {"start": v(-33.66, 24.89) * mm, "end": v(10.8, 24.89) * mm});
            skLineSegment(sketch, "E40.trimOffspring", {"start": v(-33.66, 56.64) * mm, "end": v(10.8, 56.64) * mm});
            skLineSegment(sketch, "E41.trimOffspring", {"start": v(-33.66, 59.81) * mm, "end": v(7.62, 59.81) * mm});
            skLineSegment(sketch, "E42", {"start": v(-33.66, 24.89) * mm, "end": v(-36.83, 24.89) * mm});
            skLineSegment(sketch, "E43", {"start": v(-33.66, 21.71) * mm, "end": v(-36.83, 21.71) * mm});
            skLineSegment(sketch, "E44.trimOffspring", {"start": v(-36.83, 21.71) * mm, "end": v(-36.83, 15.36) * mm});
            skLineSegment(sketch, "E45.trimOffspring", {"start": v(-33.66, 21.71) * mm, "end": v(-33.66, 12.19) * mm});
            skLineSegment(sketch, "E46.trimOffspring", {"start": v(10.8, -19.56) * mm, "end": v(55.24, -19.56) * mm});
            skLineSegment(sketch, "E47.trimOffspring", {"start": v(10.8, -22.74) * mm, "end": v(52.07, -22.74) * mm});
            skLineSegment(sketch, "E48.trimOffspring", {"start": v(-33.66, -32.26) * mm, "end": v(-33.66, -76.71) * mm});
            skLineSegment(sketch, "E49.trimOffspring", {"start": v(-36.83, -32.26) * mm, "end": v(-36.83, -73.54) * mm});
            skLineSegment(sketch, "E50.trimOffspring", {"start": v(-259.08, -111.64) * mm, "end": v(-259.08, -117.99) * mm});
            skLineSegment(sketch, "E51.trimOffspring", {"start": v(-255.9, -111.64) * mm, "end": v(-255.9, -121.16) * mm});
            skLineSegment(sketch, "E52.trimOffspring", {"start": v(-265.43, -117.99) * mm, "end": v(-259.08, -117.99) * mm});
            skLineSegment(sketch, "E53.trimOffspring", {"start": v(-265.43, -121.16) * mm, "end": v(-255.9, -121.16) * mm});
            skLineSegment(sketch, "E54.trimOffspring", {"start": v(-78.1, -73.54) * mm, "end": v(-36.83, -73.54) * mm});
            skLineSegment(sketch, "E55.trimOffspring", {"start": v(-78.1, -76.71) * mm, "end": v(-33.66, -76.71) * mm});
            skLineSegment(sketch, "E56.trimOffspring", {"start": v(-81.28, -111.64) * mm, "end": v(-81.28, -117.99) * mm});
            skLineSegment(sketch, "E57.trimOffspring", {"start": v(-78.1, -111.64) * mm, "end": v(-78.1, -121.16) * mm});
            skLineSegment(sketch, "E58.trimOffspring", {"start": v(-87.63, -117.99) * mm, "end": v(-81.28, -117.99) * mm});
            skLineSegment(sketch, "E59.trimOffspring", {"start": v(-87.63, -121.16) * mm, "end": v(-78.1, -121.16) * mm});
            skLineSegment(sketch, "E60.trimOffspring", {"start": v(-33.66, -117.99) * mm, "end": v(7.62, -117.99) * mm});
            skLineSegment(sketch, "E61.trimOffspring", {"start": v(-33.66, -121.16) * mm, "end": v(10.8, -121.16) * mm});
            skLineSegment(sketch, "E62.trimOffspring", {"start": v(99.7, -73.54) * mm, "end": v(115.57, -73.54) * mm});
            skLineSegment(sketch, "E63.trimOffspring", {"start": v(99.7, -76.71) * mm, "end": v(115.57, -76.71) * mm});
            skLineSegment(sketch, "E64.trimOffspring", {"start": v(96.52, -111.64) * mm, "end": v(96.52, -117.99) * mm});
            skLineSegment(sketch, "E65.trimOffspring", {"start": v(99.7, -111.64) * mm, "end": v(99.7, -121.16) * mm});
            skLineSegment(sketch, "E66.trimOffspring", {"start": v(90.17, -117.99) * mm, "end": v(96.52, -117.99) * mm});
            skLineSegment(sketch, "E67.trimOffspring", {"start": v(90.17, -121.16) * mm, "end": v(99.7, -121.16) * mm});
            skLineSegment(sketch, "E68", {"start": v(10.8, -111.64) * mm, "end": v(42.54, -111.64) * mm});
            skLineSegment(sketch, "E69", {"start": v(10.8, -73.54) * mm, "end": v(42.54, -73.54) * mm});
            skLineSegment(sketch, "E70", {"start": v(-268.6, 24.89) * mm, "end": v(-283.74, 24.89) * mm});
            skLineSegment(sketch, "E71.trimOffspring", {"start": v(99.7, 12.19) * mm, "end": v(99.7, -32.26) * mm});
            skLineSegment(sketch, "E72", {"start": v(-167, -76.71) * mm, "end": v(-135.26, -76.71) * mm});
            skLineSegment(sketch, "E73", {"start": v(-167, -73.54) * mm, "end": v(-135.26, -73.54) * mm});
            skLineSegment(sketch, "E74", {"start": v(-268.6, -32.26) * mm, "end": v(-268.6, -64.01) * mm});
            skLineSegment(sketch, "E75", {"start": v(90.17, -32.26) * mm, "end": v(90.17, -64.01) * mm});
            skSolve(sketch);
        }
        {
            var Q0;
            {var subQ0=sQuery(id+"F0.wireOp",EDGE,"E4.0.1.9");Q0=makeQuery(id+"F0.imprint","IMPRINT",FACE,{"disambiguationData":[TD([[makeQuery(id+"F0.imprint","IMPRINT",EDGE,{"derivedFrom":subQ0}),-1.0]])]});}
            var Q1;
            Q1=makeQuery(id+"F0.imprint","IMPRINT",FACE,{"disambiguationData":[TD([[makeQuery(id+"F0.imprint","IMPRINT",EDGE,{"derivedFrom":sQuery(id+"F0.wireOp",EDGE,"E4.0.1.2")}),1.0]])]});
            var Q2;
            {var subQ0=sQuery(id+"F0.wireOp",EDGE,"E4.0.1.7");Q2=makeQuery(id+"F0.imprint","IMPRINT",FACE,{"disambiguationData":[TD([[makeQuery(id+"F0.imprint","IMPRINT",EDGE,{"derivedFrom":subQ0}),1.0]])]});}
            var Q3;
            {var subQ0=sQuery(id+"F0.wireOp",EDGE,"E4.1.1.8");Q3=makeQuery(id+"F0.imprint","IMPRINT",FACE,{"disambiguationData":[TD([[makeQuery(id+"F0.imprint","IMPRINT",EDGE,{"derivedFrom":subQ0}),-1.0]])]});}
            var Q4;
            {var subQ0=sQuery(id+"F0.wireOp",EDGE,"E4.1.1.9");var subQ1=sQuery(id+"F0.wireOp",EDGE,"E4.0.1.11");var subQ2=makeQuery(id+"F0.imprint","INTERSECT",VERTEX,{"derivedFrom":[subQ1,subQ0]});Q4=makeQuery(id+"F0.imprint","IMPRINT",FACE,{"disambiguationData":[TD([[makeQuery(id+"F0.imprint","IMPRINT",EDGE,{"disambiguationData":[TD([[subQ2,-1.0]])],"derivedFrom":subQ1}),1.0]])]});}
            var Q5;
            {var subQ0=sQuery(id+"F0.wireOp",EDGE,"E4.1.1.9");var subQ1=sQuery(id+"F0.wireOp",EDGE,"E4.1.1.5");var subQ2=makeQuery(id+"F0.imprint","INTERSECT",VERTEX,{"derivedFrom":[subQ1,subQ0]});Q5=makeQuery(id+"F0.imprint","IMPRINT",FACE,{"disambiguationData":[TD([[makeQuery(id+"F0.imprint","IMPRINT",EDGE,{"disambiguationData":[TD([[subQ2,-1.0]])],"derivedFrom":subQ1}),-1.0]])]});}
            var Q6;
            {var subQ1=sQuery(id+"F0.wireOp",EDGE,"E4.1.1.7");var subQ7=sQuery(id+"F0.wireOp",EDGE,"E4.1.1.2");var subQ8=makeQuery(id+"F0.imprint","INTERSECT",VERTEX,{"derivedFrom":[subQ7,subQ1]});Q6=makeQuery(id+"F0.imprint","IMPRINT",FACE,{"disambiguationData":[TD([[makeQuery(id+"F0.imprint","IMPRINT",EDGE,{"disambiguationData":[TD([[subQ8,-1.0]])],"derivedFrom":subQ7}),-1.0]])]});}
            var Q7;
            {var subQ1=sQuery(id+"F0.wireOp",EDGE,"E4.1.1.1");var subQ9=sQuery(id+"F0.wireOp",EDGE,"E4.1.1.13");var subQ11=makeQuery(id+"F0.imprint","INTERSECT",VERTEX,{"derivedFrom":[subQ1,subQ9]});Q7=makeQuery(id+"F0.imprint","IMPRINT",FACE,{"disambiguationData":[TD([[makeQuery(id+"F0.imprint","IMPRINT",EDGE,{"disambiguationData":[TD([[subQ11,-1.0]])],"derivedFrom":subQ1}),-1.0]])]});}
            var Q8;
            {var subQ0=sQuery(id+"F0.wireOp",EDGE,"E4.1.1.7");var subQ1=sQuery(id+"F0.wireOp",EDGE,"E4.1.1.1");var subQ2=makeQuery(id+"F0.imprint","INTERSECT",VERTEX,{"derivedFrom":[subQ1,subQ0]});Q8=makeQuery(id+"F0.imprint","IMPRINT",FACE,{"disambiguationData":[TD([[makeQuery(id+"F0.imprint","IMPRINT",EDGE,{"disambiguationData":[TD([[subQ2,-1.0]])],"derivedFrom":subQ1}),-1.0]])]});}
            var Q9;
            {var subQ0=sQuery(id+"F0.wireOp",EDGE,"E4.1.1.7");var subQ1=sQuery(id+"F0.wireOp",EDGE,"E4.1.0.0");var subQ2=makeQuery(id+"F0.imprint","INTERSECT",VERTEX,{"derivedFrom":[subQ1,subQ0]});Q9=makeQuery(id+"F0.imprint","IMPRINT",FACE,{"disambiguationData":[TD([[makeQuery(id+"F0.imprint","IMPRINT",EDGE,{"disambiguationData":[TD([[subQ2,-1.0]])],"derivedFrom":subQ1}),-1.0]])]});}
            var Q10;
            {var subQ12=sQuery(id+"F0.wireOp",EDGE,"E4.1.2.7");Q10=makeQuery(id+"F0.imprint","IMPRINT",FACE,{"disambiguationData":[TD([[makeQuery(id+"F0.imprint","IMPRINT",EDGE,{"derivedFrom":subQ12}),1.0]])]});}
            var Q11;
            {var subQ0=sQuery(id+"F0.wireOp",EDGE,"E31.trimOffspring");Q11=makeQuery(id+"F0.imprint","IMPRINT",FACE,{"disambiguationData":[TD([[makeQuery(id+"F0.imprint","IMPRINT",EDGE,{"derivedFrom":subQ0}),-1.0]])]});}
            var Q12;
            {var subQ0=sQuery(id+"F0.wireOp",EDGE,"E4.1.2.3");var subQ1=sQuery(id+"F0.wireOp",EDGE,"E4.1.1.5");var subQ2=makeQuery(id+"F0.imprint","INTERSECT",VERTEX,{"derivedFrom":[subQ1,subQ0]});Q12=makeQuery(id+"F0.imprint","IMPRINT",FACE,{"disambiguationData":[TD([[makeQuery(id+"F0.imprint","IMPRINT",EDGE,{"disambiguationData":[TD([[subQ2,1.0]])],"derivedFrom":subQ1}),-1.0]])]});}
            var Q13;
            {var subQ0=sQuery(id+"F0.wireOp",EDGE,"E4.1.2.15");var subQ1=sQuery(id+"F0.wireOp",EDGE,"E4.1.1.0");var subQ2=makeQuery(id+"F0.imprint","INTERSECT",VERTEX,{"derivedFrom":[subQ1,subQ0]});Q13=makeQuery(id+"F0.imprint","IMPRINT",FACE,{"disambiguationData":[TD([[makeQuery(id+"F0.imprint","IMPRINT",EDGE,{"disambiguationData":[TD([[subQ2,-1.0]])],"derivedFrom":subQ1}),1.0]])]});}
            var Q14;
            {var subQ0=sQuery(id+"F0.wireOp",EDGE,"E4.0.2.10");Q14=makeQuery(id+"F0.imprint","IMPRINT",FACE,{"disambiguationData":[TD([[makeQuery(id+"F0.imprint","IMPRINT",EDGE,{"derivedFrom":subQ0}),1.0]])]});}
            var Q15;
            {var subQ0=sQuery(id+"F0.wireOp",EDGE,"E4.0.2.7");var subQ1=sQuery(id+"F0.wireOp",EDGE,"E4.0.1.0");var subQ2=makeQuery(id+"F0.imprint","INTERSECT",VERTEX,{"derivedFrom":[subQ1,subQ0]});Q15=makeQuery(id+"F0.imprint","IMPRINT",FACE,{"disambiguationData":[TD([[makeQuery(id+"F0.imprint","IMPRINT",EDGE,{"disambiguationData":[TD([[subQ2,-1.0]])],"derivedFrom":subQ1}),-1.0]])]});}
            var Q16;
            {var subQ0=sQuery(id+"F0.wireOp",EDGE,"E4.1.2.15");var subQ1=sQuery(id+"F0.wireOp",EDGE,"E4.1.2.1");var subQ2=makeQuery(id+"F0.imprint","INTERSECT",VERTEX,{"derivedFrom":[subQ1,subQ0]});Q16=makeQuery(id+"F0.imprint","IMPRINT",FACE,{"disambiguationData":[TD([[makeQuery(id+"F0.imprint","IMPRINT",EDGE,{"disambiguationData":[TD([[subQ2,-1.0]])],"derivedFrom":subQ1}),-1.0]])]});}
            var Q17;
            {var subQ0=sQuery(id+"F0.wireOp",EDGE,"E4.2.2.12");var subQ1=sQuery(id+"F0.wireOp",EDGE,"E4.1.2.1");var subQ2=makeQuery(id+"F0.imprint","INTERSECT",VERTEX,{"derivedFrom":[subQ1,subQ0]});Q17=makeQuery(id+"F0.imprint","IMPRINT",FACE,{"disambiguationData":[TD([[makeQuery(id+"F0.imprint","IMPRINT",EDGE,{"disambiguationData":[TD([[subQ2,-1.0]])],"derivedFrom":subQ1}),-1.0]])]});}
            var Q18;
            {var subQ0=sQuery(id+"F0.wireOp",EDGE,"E4.1.2.11");var subQ1=sQuery(id+"F0.wireOp",EDGE,"E4.1.2.1");var subQ2=makeQuery(id+"F0.imprint","INTERSECT",VERTEX,{"derivedFrom":[subQ1,subQ0]});Q18=makeQuery(id+"F0.imprint","IMPRINT",FACE,{"disambiguationData":[TD([[makeQuery(id+"F0.imprint","IMPRINT",EDGE,{"disambiguationData":[TD([[subQ2,1.0]])],"derivedFrom":subQ1}),-1.0]])]});}
            var Q19;
            {var subQ5=sQuery(id+"F0.wireOp",EDGE,"E4.1.2.2");var subQ7=sQuery(id+"F0.wireOp",EDGE,"E4.2.2.12");var subQ8=makeQuery(id+"F0.imprint","INTERSECT",VERTEX,{"derivedFrom":[subQ5,subQ7]});Q19=makeQuery(id+"F0.imprint","IMPRINT",FACE,{"disambiguationData":[TD([[makeQuery(id+"F0.imprint","IMPRINT",EDGE,{"disambiguationData":[TD([[subQ8,-1.0]])],"derivedFrom":subQ5}),-1.0]])]});}
            var Q20;
            {var subQ0=sQuery(id+"F0.wireOp",EDGE,"E4.2.2.9");var subQ1=sQuery(id+"F0.wireOp",EDGE,"E4.1.2.4");var subQ2=makeQuery(id+"F0.imprint","INTERSECT",VERTEX,{"derivedFrom":[subQ1,subQ0]});Q20=makeQuery(id+"F0.imprint","IMPRINT",FACE,{"disambiguationData":[TD([[makeQuery(id+"F0.imprint","IMPRINT",EDGE,{"disambiguationData":[TD([[subQ2,-1.0]])],"derivedFrom":subQ1}),1.0]])]});}
            var Q21;
            {var subQ0=sQuery(id+"F0.wireOp",EDGE,"E4.2.2.9");var subQ1=sQuery(id+"F0.wireOp",EDGE,"E4.1.2.11");var subQ2=makeQuery(id+"F0.imprint","INTERSECT",VERTEX,{"derivedFrom":[subQ1,subQ0]});Q21=makeQuery(id+"F0.imprint","IMPRINT",FACE,{"disambiguationData":[TD([[makeQuery(id+"F0.imprint","IMPRINT",EDGE,{"disambiguationData":[TD([[subQ2,-1.0]])],"derivedFrom":subQ1}),1.0]])]});}
            var Q22;
            {var subQ0=sQuery(id+"F0.wireOp",EDGE,"E4.2.2.12");var subQ1=sQuery(id+"F0.wireOp",EDGE,"E4.1.1.0");var subQ2=makeQuery(id+"F0.imprint","INTERSECT",VERTEX,{"derivedFrom":[subQ1,subQ0]});Q22=makeQuery(id+"F0.imprint","IMPRINT",FACE,{"disambiguationData":[TD([[makeQuery(id+"F0.imprint","IMPRINT",EDGE,{"disambiguationData":[TD([[subQ2,-1.0]])],"derivedFrom":subQ1}),-1.0]])]});}
            var Q23;
            {var subQ0=sQuery(id+"F0.wireOp",EDGE,"E4.2.2.12");var subQ1=sQuery(id+"F0.wireOp",EDGE,"E4.1.1.0");var subQ2=makeQuery(id+"F0.imprint","INTERSECT",VERTEX,{"derivedFrom":[subQ1,subQ0]});Q23=makeQuery(id+"F0.imprint","IMPRINT",FACE,{"disambiguationData":[TD([[makeQuery(id+"F0.imprint","IMPRINT",EDGE,{"disambiguationData":[TD([[subQ2,-1.0]])],"derivedFrom":subQ1}),1.0]])]});}
            var Q24;
            {var subQ5=sQuery(id+"F0.wireOp",EDGE,"E4.2.2.3");var subQ6=sQuery(id+"F0.wireOp",EDGE,"E4.1.1.4");var subQ7=makeQuery(id+"F0.imprint","INTERSECT",VERTEX,{"derivedFrom":[subQ6,subQ5]});Q24=makeQuery(id+"F0.imprint","IMPRINT",FACE,{"disambiguationData":[TD([[makeQuery(id+"F0.imprint","IMPRINT",EDGE,{"disambiguationData":[TD([[subQ7,-1.0]])],"derivedFrom":subQ6}),-1.0]])]});}
            var Q25;
            {var subQ0=sQuery(id+"F0.wireOp",EDGE,"E4.2.2.3");var subQ1=sQuery(id+"F0.wireOp",EDGE,"E4.1.1.4");var subQ2=makeQuery(id+"F0.imprint","INTERSECT",VERTEX,{"derivedFrom":[subQ1,subQ0]});Q25=makeQuery(id+"F0.imprint","IMPRINT",FACE,{"disambiguationData":[TD([[makeQuery(id+"F0.imprint","IMPRINT",EDGE,{"disambiguationData":[TD([[subQ2,-1.0]])],"derivedFrom":subQ1}),1.0]])]});}
            var Q26;
            {var subQ5=sQuery(id+"F0.wireOp",EDGE,"E4.1.1.11");var subQ6=sQuery(id+"F0.wireOp",EDGE,"E4.1.1.0");var subQ7=makeQuery(id+"F0.imprint","INTERSECT",VERTEX,{"derivedFrom":[subQ6,subQ5]});Q26=makeQuery(id+"F0.imprint","IMPRINT",FACE,{"disambiguationData":[TD([[makeQuery(id+"F0.imprint","IMPRINT",EDGE,{"disambiguationData":[TD([[subQ7,1.0]])],"derivedFrom":subQ6}),1.0]])]});}
            var Q27;
            {var subQ0=sQuery(id+"F0.wireOp",EDGE,"E4.2.2.3");var subQ1=sQuery(id+"F0.wireOp",EDGE,"E4.1.1.11");var subQ2=makeQuery(id+"F0.imprint","INTERSECT",VERTEX,{"derivedFrom":[subQ1,subQ0]});Q27=makeQuery(id+"F0.imprint","IMPRINT",FACE,{"disambiguationData":[TD([[makeQuery(id+"F0.imprint","IMPRINT",EDGE,{"disambiguationData":[TD([[subQ2,-1.0]])],"derivedFrom":subQ1}),1.0]])]});}
            var Q28;
            {var subQ0=sQuery(id+"F0.wireOp",EDGE,"E4.2.1.14");var subQ1=sQuery(id+"F0.wireOp",EDGE,"E4.1.1.4");var subQ2=makeQuery(id+"F0.imprint","INTERSECT",VERTEX,{"derivedFrom":[subQ1,subQ0]});Q28=makeQuery(id+"F0.imprint","IMPRINT",FACE,{"disambiguationData":[TD([[makeQuery(id+"F0.imprint","IMPRINT",EDGE,{"disambiguationData":[TD([[subQ2,-1.0]])],"derivedFrom":subQ1}),1.0]])]});}
            var Q29;
            Q29=makeQuery(id+"F0.imprint","IMPRINT",FACE,{"disambiguationData":[TD([[makeQuery(id+"F0.imprint","IMPRINT",EDGE,{"derivedFrom":sQuery(id+"F0.wireOp",EDGE,"E4.2.1.2")}),1.0]])]});
            var Q30;
            {var subQ0=sQuery(id+"F0.wireOp",EDGE,"E4.2.2.7");var subQ1=sQuery(id+"F0.wireOp",EDGE,"E4.2.1.0");var subQ2=makeQuery(id+"F0.imprint","INTERSECT",VERTEX,{"derivedFrom":[subQ1,subQ0]});Q30=makeQuery(id+"F0.imprint","IMPRINT",FACE,{"disambiguationData":[TD([[makeQuery(id+"F0.imprint","IMPRINT",EDGE,{"disambiguationData":[TD([[subQ2,-1.0]])],"derivedFrom":subQ1}),-1.0]])]});}
            var Q31;
            {var subQ0=sQuery(id+"F0.wireOp",EDGE,"E4.2.2.7");var subQ1=sQuery(id+"F0.wireOp",EDGE,"E4.2.2.1");var subQ2=makeQuery(id+"F0.imprint","INTERSECT",VERTEX,{"derivedFrom":[subQ1,subQ0]});Q31=makeQuery(id+"F0.imprint","IMPRINT",FACE,{"disambiguationData":[TD([[makeQuery(id+"F0.imprint","IMPRINT",EDGE,{"disambiguationData":[TD([[subQ2,-1.0]])],"derivedFrom":subQ1}),-1.0]])]});}
            var Q32;
            {var subQ7=sQuery(id+"F0.wireOp",EDGE,"E4.2.2.2");var subQ9=sQuery(id+"F0.wireOp",EDGE,"E4.2.2.7");var subQ11=makeQuery(id+"F0.imprint","INTERSECT",VERTEX,{"derivedFrom":[subQ7,subQ9]});Q32=makeQuery(id+"F0.imprint","IMPRINT",FACE,{"disambiguationData":[TD([[makeQuery(id+"F0.imprint","IMPRINT",EDGE,{"disambiguationData":[TD([[subQ11,-1.0]])],"derivedFrom":subQ7}),-1.0]])]});}
            var Q33;
            {var subQ0=sQuery(id+"F0.wireOp",EDGE,"E4.2.2.9");var subQ1=sQuery(id+"F0.wireOp",EDGE,"E4.2.2.5");var subQ2=makeQuery(id+"F0.imprint","INTERSECT",VERTEX,{"derivedFrom":[subQ1,subQ0]});Q33=makeQuery(id+"F0.imprint","IMPRINT",FACE,{"disambiguationData":[TD([[makeQuery(id+"F0.imprint","IMPRINT",EDGE,{"disambiguationData":[TD([[subQ2,-1.0]])],"derivedFrom":subQ1}),-1.0]])]});}
            var Q34;
            {var subQ6=sQuery(id+"F0.wireOp",EDGE,"E4.2.2.1");var subQ9=sQuery(id+"F0.wireOp",EDGE,"E4.2.2.13");var subQ10=makeQuery(id+"F0.imprint","INTERSECT",VERTEX,{"derivedFrom":[subQ6,subQ9]});Q34=makeQuery(id+"F0.imprint","IMPRINT",FACE,{"disambiguationData":[TD([[makeQuery(id+"F0.imprint","IMPRINT",EDGE,{"disambiguationData":[TD([[subQ10,-1.0]])],"derivedFrom":subQ6}),-1.0]])]});}
            var Q35;
            {var subQ0=sQuery(id+"F0.wireOp",EDGE,"E4.3.2.12");var subQ1=sQuery(id+"F0.wireOp",EDGE,"E4.2.2.1");var subQ2=makeQuery(id+"F0.imprint","INTERSECT",VERTEX,{"derivedFrom":[subQ1,subQ0]});Q35=makeQuery(id+"F0.imprint","IMPRINT",FACE,{"disambiguationData":[TD([[makeQuery(id+"F0.imprint","IMPRINT",EDGE,{"disambiguationData":[TD([[subQ2,1.0]])],"derivedFrom":subQ1}),-1.0]])]});}
            var Q36;
            {var subQ19=sQuery(id+"F0.wireOp",EDGE,"E4.3.2.3");Q36=makeQuery(id+"F0.imprint","IMPRINT",FACE,{"disambiguationData":[TD([[makeQuery(id+"F0.imprint","IMPRINT",EDGE,{"derivedFrom":subQ19}),-1.0]])]});}
            var Q37;
            {var subQ1=sQuery(id+"F0.wireOp",EDGE,"E36.trimOffspring");Q37=makeQuery(id+"F0.imprint","IMPRINT",FACE,{"disambiguationData":[TD([[makeQuery(id+"F0.imprint","IMPRINT",EDGE,{"derivedFrom":subQ1}),-1.0]])]});}
            var Q38;
            {var subQ0=sQuery(id+"F0.wireOp",EDGE,"E4.2.1.8");var subQ1=sQuery(id+"F0.wireOp",EDGE,"E4.1.0.0");var subQ2=makeQuery(id+"F0.imprint","INTERSECT",VERTEX,{"derivedFrom":[subQ1,subQ0]});Q38=makeQuery(id+"F0.imprint","IMPRINT",FACE,{"disambiguationData":[TD([[makeQuery(id+"F0.imprint","IMPRINT",EDGE,{"disambiguationData":[TD([[subQ2,1.0]])],"derivedFrom":subQ1}),-1.0]])]});}
            var Q39;
            {var subQ0=sQuery(id+"F0.wireOp",EDGE,"E4.2.1.12");var subQ1=sQuery(id+"F0.wireOp",EDGE,"E4.1.1.1");var subQ2=makeQuery(id+"F0.imprint","INTERSECT",VERTEX,{"derivedFrom":[subQ1,subQ0]});Q39=makeQuery(id+"F0.imprint","IMPRINT",FACE,{"disambiguationData":[TD([[makeQuery(id+"F0.imprint","IMPRINT",EDGE,{"disambiguationData":[TD([[subQ2,-1.0]])],"derivedFrom":subQ1}),-1.0]])]});}
            var Q40;
            {var subQ7=sQuery(id+"F0.wireOp",EDGE,"E4.1.1.2");var subQ9=sQuery(id+"F0.wireOp",EDGE,"E4.2.1.12");var subQ10=makeQuery(id+"F0.imprint","INTERSECT",VERTEX,{"derivedFrom":[subQ7,subQ9]});Q40=makeQuery(id+"F0.imprint","IMPRINT",FACE,{"disambiguationData":[TD([[makeQuery(id+"F0.imprint","IMPRINT",EDGE,{"disambiguationData":[TD([[subQ10,-1.0]])],"derivedFrom":subQ7}),-1.0]])]});}
            var Q41;
            {var subQ0=sQuery(id+"F0.wireOp",EDGE,"E4.1.1.11");var subQ1=sQuery(id+"F0.wireOp",EDGE,"E4.1.1.1");var subQ2=makeQuery(id+"F0.imprint","INTERSECT",VERTEX,{"derivedFrom":[subQ1,subQ0]});Q41=makeQuery(id+"F0.imprint","IMPRINT",FACE,{"disambiguationData":[TD([[makeQuery(id+"F0.imprint","IMPRINT",EDGE,{"disambiguationData":[TD([[subQ2,1.0]])],"derivedFrom":subQ1}),-1.0]])]});}
            var Q42;
            {var subQ0=sQuery(id+"F0.wireOp",EDGE,"E4.1.1.15");var subQ1=sQuery(id+"F0.wireOp",EDGE,"E4.1.1.1");var subQ2=makeQuery(id+"F0.imprint","INTERSECT",VERTEX,{"derivedFrom":[subQ1,subQ0]});Q42=makeQuery(id+"F0.imprint","IMPRINT",FACE,{"disambiguationData":[TD([[makeQuery(id+"F0.imprint","IMPRINT",EDGE,{"disambiguationData":[TD([[subQ2,-1.0]])],"derivedFrom":subQ1}),-1.0]])]});}
            var Q43;
            {var subQ0=sQuery(id+"F0.wireOp",EDGE,"E4.2.1.9");var subQ1=sQuery(id+"F0.wireOp",EDGE,"E4.1.1.11");var subQ2=makeQuery(id+"F0.imprint","INTERSECT",VERTEX,{"derivedFrom":[subQ1,subQ0]});Q43=makeQuery(id+"F0.imprint","IMPRINT",FACE,{"disambiguationData":[TD([[makeQuery(id+"F0.imprint","IMPRINT",EDGE,{"disambiguationData":[TD([[subQ2,-1.0]])],"derivedFrom":subQ1}),1.0]])]});}
            var Q44;
            {var subQ0=sQuery(id+"F0.wireOp",EDGE,"E4.2.1.9");var subQ1=sQuery(id+"F0.wireOp",EDGE,"E4.1.1.4");var subQ2=makeQuery(id+"F0.imprint","INTERSECT",VERTEX,{"derivedFrom":[subQ1,subQ0]});Q44=makeQuery(id+"F0.imprint","IMPRINT",FACE,{"disambiguationData":[TD([[makeQuery(id+"F0.imprint","IMPRINT",EDGE,{"disambiguationData":[TD([[subQ2,-1.0]])],"derivedFrom":subQ1}),1.0]])]});}
            var Q45;
            {var subQ0=sQuery(id+"F0.wireOp",EDGE,"E4.2.1.7");Q45=makeQuery(id+"F0.imprint","IMPRINT",FACE,{"disambiguationData":[TD([[makeQuery(id+"F0.imprint","IMPRINT",EDGE,{"derivedFrom":subQ0}),1.0]])]});}
            var Q46;
            {var subQ0=sQuery(id+"F0.wireOp",EDGE,"E4.3.1.8");Q46=makeQuery(id+"F0.imprint","IMPRINT",FACE,{"disambiguationData":[TD([[makeQuery(id+"F0.imprint","IMPRINT",EDGE,{"derivedFrom":subQ0}),-1.0]])]});}
            var Q47;
            {var subQ0=sQuery(id+"F0.wireOp",EDGE,"E40.trimOffspring");var subQ1=sQuery(id+"F0.wireOp",EDGE,"E4.2.1.11");var subQ2=makeQuery(id+"F0.imprint","INTERSECT",VERTEX,{"derivedFrom":[subQ1,subQ0]});Q47=makeQuery(id+"F0.imprint","IMPRINT",FACE,{"disambiguationData":[TD([[makeQuery(id+"F0.imprint","IMPRINT",EDGE,{"disambiguationData":[TD([[subQ2,1.0]])],"derivedFrom":subQ1}),1.0]])]});}
            var Q48;
            {var subQ0=sQuery(id+"F0.wireOp",EDGE,"E41.trimOffspring");var subQ1=sQuery(id+"F0.wireOp",EDGE,"E4.3.1.5");var subQ2=makeQuery(id+"F0.imprint","INTERSECT",VERTEX,{"derivedFrom":[subQ1,subQ0]});Q48=makeQuery(id+"F0.imprint","IMPRINT",FACE,{"disambiguationData":[TD([[makeQuery(id+"F0.imprint","IMPRINT",EDGE,{"disambiguationData":[TD([[subQ2,-1.0]])],"derivedFrom":subQ1}),-1.0]])]});}
            var Q49;
            {var subQ1=sQuery(id+"F0.wireOp",EDGE,"E30.trimOffspring");var subQ3=sQuery(id+"F0.wireOp",EDGE,"E4.3.1.2");var subQ4=makeQuery(id+"F0.imprint","INTERSECT",VERTEX,{"derivedFrom":[subQ3,subQ1]});Q49=makeQuery(id+"F0.imprint","IMPRINT",FACE,{"disambiguationData":[TD([[makeQuery(id+"F0.imprint","IMPRINT",EDGE,{"disambiguationData":[TD([[subQ4,-1.0]])],"derivedFrom":subQ3}),-1.0]])]});}
            var Q50;
            {var subQ7=sQuery(id+"F0.wireOp",EDGE,"E4.3.1.13");var subQ8=sQuery(id+"F0.wireOp",EDGE,"E4.3.1.1");var subQ9=makeQuery(id+"F0.imprint","INTERSECT",VERTEX,{"derivedFrom":[subQ8,subQ7]});Q50=makeQuery(id+"F0.imprint","IMPRINT",FACE,{"disambiguationData":[TD([[makeQuery(id+"F0.imprint","IMPRINT",EDGE,{"disambiguationData":[TD([[subQ9,-1.0]])],"derivedFrom":subQ8}),-1.0]])]});}
            var Q51;
            {var subQ0=sQuery(id+"F0.wireOp",EDGE,"E30.trimOffspring");var subQ1=sQuery(id+"F0.wireOp",EDGE,"E4.3.1.1");var subQ2=makeQuery(id+"F0.imprint","INTERSECT",VERTEX,{"derivedFrom":[subQ1,subQ0]});Q51=makeQuery(id+"F0.imprint","IMPRINT",FACE,{"disambiguationData":[TD([[makeQuery(id+"F0.imprint","IMPRINT",EDGE,{"disambiguationData":[TD([[subQ2,-1.0]])],"derivedFrom":subQ1}),-1.0]])]});}
            var Q52;
            {var subQ0=sQuery(id+"F0.wireOp",EDGE,"E29.trimOffspring");var subQ1=sQuery(id+"F0.wireOp",EDGE,"E4.3.0.0");var subQ2=makeQuery(id+"F0.imprint","INTERSECT",VERTEX,{"derivedFrom":[subQ1,subQ0]});Q52=makeQuery(id+"F0.imprint","IMPRINT",FACE,{"disambiguationData":[TD([[makeQuery(id+"F0.imprint","IMPRINT",EDGE,{"disambiguationData":[TD([[subQ2,1.0]])],"derivedFrom":subQ1}),-1.0]])]});}
            var Q53;
            {var subQ0=sQuery(id+"F0.wireOp",EDGE,"E29.trimOffspring");var subQ1=sQuery(id+"F0.wireOp",EDGE,"E4.3.1.1");var subQ2=makeQuery(id+"F0.imprint","INTERSECT",VERTEX,{"derivedFrom":[subQ1,subQ0]});Q53=makeQuery(id+"F0.imprint","IMPRINT",FACE,{"disambiguationData":[TD([[makeQuery(id+"F0.imprint","IMPRINT",EDGE,{"disambiguationData":[TD([[subQ2,-1.0]])],"derivedFrom":subQ1}),-1.0]])]});}
            var Q54;
            {var subQ0=sQuery(id+"F0.wireOp",EDGE,"E39.trimOffspring");var subQ1=sQuery(id+"F0.wireOp",EDGE,"E4.3.1.5");var subQ2=makeQuery(id+"F0.imprint","INTERSECT",VERTEX,{"derivedFrom":[subQ1,subQ0]});Q54=makeQuery(id+"F0.imprint","IMPRINT",FACE,{"disambiguationData":[TD([[makeQuery(id+"F0.imprint","IMPRINT",EDGE,{"disambiguationData":[TD([[subQ2,1.0]])],"derivedFrom":subQ1}),-1.0]])]});}
            var Q55;
            {var subQ0=sQuery(id+"F0.wireOp",EDGE,"E46.trimOffspring");var subQ1=sQuery(id+"F0.wireOp",EDGE,"E4.3.2.15");var subQ2=makeQuery(id+"F0.imprint","INTERSECT",VERTEX,{"derivedFrom":[subQ1,subQ0]});Q55=makeQuery(id+"F0.imprint","IMPRINT",FACE,{"disambiguationData":[TD([[makeQuery(id+"F0.imprint","IMPRINT",EDGE,{"disambiguationData":[TD([[subQ2,-1.0]])],"derivedFrom":subQ1}),1.0]])]});}
            var Q56;
            {var subQ0=sQuery(id+"F0.wireOp",EDGE,"E46.trimOffspring");var subQ1=sQuery(id+"F0.wireOp",EDGE,"E4.4.2.8");var subQ2=makeQuery(id+"F0.imprint","INTERSECT",VERTEX,{"derivedFrom":[subQ1,subQ0]});Q56=makeQuery(id+"F0.imprint","IMPRINT",FACE,{"disambiguationData":[TD([[makeQuery(id+"F0.imprint","IMPRINT",EDGE,{"disambiguationData":[TD([[subQ2,-1.0]])],"derivedFrom":subQ1}),-1.0]])]});}
            var Q57;
            {var subQ1=sQuery(id+"F0.wireOp",EDGE,"E4.3.2.4");var subQ9=sQuery(id+"F0.wireOp",EDGE,"E47.trimOffspring");var subQ11=makeQuery(id+"F0.imprint","INTERSECT",VERTEX,{"derivedFrom":[subQ1,subQ9]});Q57=makeQuery(id+"F0.imprint","IMPRINT",FACE,{"disambiguationData":[TD([[makeQuery(id+"F0.imprint","IMPRINT",EDGE,{"disambiguationData":[TD([[subQ11,-1.0]])],"derivedFrom":subQ1}),1.0]])]});}
            var Q58;
            {var subQ0=sQuery(id+"F0.wireOp",EDGE,"E4.4.2.12");var subQ1=sQuery(id+"F0.wireOp",EDGE,"E4.3.1.0");var subQ2=makeQuery(id+"F0.imprint","INTERSECT",VERTEX,{"derivedFrom":[subQ1,subQ0]});Q58=makeQuery(id+"F0.imprint","IMPRINT",FACE,{"disambiguationData":[TD([[makeQuery(id+"F0.imprint","IMPRINT",EDGE,{"disambiguationData":[TD([[subQ2,-1.0]])],"derivedFrom":subQ1}),-1.0]])]});}
            var Q59;
            {var subQ0=sQuery(id+"F0.wireOp",EDGE,"E4.4.2.12");var subQ1=sQuery(id+"F0.wireOp",EDGE,"E4.3.1.0");var subQ2=makeQuery(id+"F0.imprint","INTERSECT",VERTEX,{"derivedFrom":[subQ1,subQ0]});Q59=makeQuery(id+"F0.imprint","IMPRINT",FACE,{"disambiguationData":[TD([[makeQuery(id+"F0.imprint","IMPRINT",EDGE,{"disambiguationData":[TD([[subQ2,-1.0]])],"derivedFrom":subQ1}),1.0]])]});}
            var Q60;
            {var subQ1=sQuery(id+"F0.wireOp",EDGE,"E4.4.2.3");var subQ3=sQuery(id+"F0.wireOp",EDGE,"E4.3.1.4");var subQ4=makeQuery(id+"F0.imprint","INTERSECT",VERTEX,{"derivedFrom":[subQ3,subQ1]});Q60=makeQuery(id+"F0.imprint","IMPRINT",FACE,{"disambiguationData":[TD([[makeQuery(id+"F0.imprint","IMPRINT",EDGE,{"disambiguationData":[TD([[subQ4,-1.0]])],"derivedFrom":subQ3}),-1.0]])]});}
            var Q61;
            {var subQ0=sQuery(id+"F0.wireOp",EDGE,"E4.3.1.11");var subQ1=sQuery(id+"F0.wireOp",EDGE,"E4.3.1.0");var subQ2=makeQuery(id+"F0.imprint","INTERSECT",VERTEX,{"derivedFrom":[subQ1,subQ0]});Q61=makeQuery(id+"F0.imprint","IMPRINT",FACE,{"disambiguationData":[TD([[makeQuery(id+"F0.imprint","IMPRINT",EDGE,{"disambiguationData":[TD([[subQ2,1.0]])],"derivedFrom":subQ1}),1.0]])]});}
            var Q62;
            {var subQ0=sQuery(id+"F0.wireOp",EDGE,"E4.3.2.15");var subQ1=sQuery(id+"F0.wireOp",EDGE,"E4.3.1.0");var subQ2=makeQuery(id+"F0.imprint","INTERSECT",VERTEX,{"derivedFrom":[subQ1,subQ0]});Q62=makeQuery(id+"F0.imprint","IMPRINT",FACE,{"disambiguationData":[TD([[makeQuery(id+"F0.imprint","IMPRINT",EDGE,{"disambiguationData":[TD([[subQ2,-1.0]])],"derivedFrom":subQ1}),1.0]])]});}
            var Q63;
            {var subQ0=sQuery(id+"F0.wireOp",EDGE,"E4.4.2.3");var subQ1=sQuery(id+"F0.wireOp",EDGE,"E4.3.1.4");var subQ2=makeQuery(id+"F0.imprint","INTERSECT",VERTEX,{"derivedFrom":[subQ1,subQ0]});Q63=makeQuery(id+"F0.imprint","IMPRINT",FACE,{"disambiguationData":[TD([[makeQuery(id+"F0.imprint","IMPRINT",EDGE,{"disambiguationData":[TD([[subQ2,-1.0]])],"derivedFrom":subQ1}),1.0]])]});}
            var Q64;
            {var subQ0=sQuery(id+"F0.wireOp",EDGE,"E4.4.1.14");var subQ1=sQuery(id+"F0.wireOp",EDGE,"E4.3.1.4");var subQ2=makeQuery(id+"F0.imprint","INTERSECT",VERTEX,{"derivedFrom":[subQ1,subQ0]});Q64=makeQuery(id+"F0.imprint","IMPRINT",FACE,{"disambiguationData":[TD([[makeQuery(id+"F0.imprint","IMPRINT",EDGE,{"disambiguationData":[TD([[subQ2,-1.0]])],"derivedFrom":subQ1}),1.0]])]});}
            var Q65;
            {var subQ0=sQuery(id+"F0.wireOp",EDGE,"E4.4.2.3");var subQ1=sQuery(id+"F0.wireOp",EDGE,"E4.3.1.11");var subQ2=makeQuery(id+"F0.imprint","INTERSECT",VERTEX,{"derivedFrom":[subQ1,subQ0]});Q65=makeQuery(id+"F0.imprint","IMPRINT",FACE,{"disambiguationData":[TD([[makeQuery(id+"F0.imprint","IMPRINT",EDGE,{"disambiguationData":[TD([[subQ2,-1.0]])],"derivedFrom":subQ1}),1.0]])]});}
            var Q66;
            {var subQ0=sQuery(id+"F0.wireOp",EDGE,"E4.4.1.9");var subQ1=sQuery(id+"F0.wireOp",EDGE,"E4.3.1.4");var subQ2=makeQuery(id+"F0.imprint","INTERSECT",VERTEX,{"derivedFrom":[subQ1,subQ0]});Q66=makeQuery(id+"F0.imprint","IMPRINT",FACE,{"disambiguationData":[TD([[makeQuery(id+"F0.imprint","IMPRINT",EDGE,{"disambiguationData":[TD([[subQ2,-1.0]])],"derivedFrom":subQ1}),1.0]])]});}
            var Q67;
            {var subQ0=sQuery(id+"F0.wireOp",EDGE,"E4.4.1.9");var subQ1=sQuery(id+"F0.wireOp",EDGE,"E4.3.1.11");var subQ2=makeQuery(id+"F0.imprint","INTERSECT",VERTEX,{"derivedFrom":[subQ1,subQ0]});Q67=makeQuery(id+"F0.imprint","IMPRINT",FACE,{"disambiguationData":[TD([[makeQuery(id+"F0.imprint","IMPRINT",EDGE,{"disambiguationData":[TD([[subQ2,-1.0]])],"derivedFrom":subQ1}),1.0]])]});}
            var Q68;
            {var subQ0=sQuery(id+"F0.wireOp",EDGE,"E4.4.1.2");Q68=makeQuery(id+"F0.imprint","IMPRINT",FACE,{"disambiguationData":[TD([[makeQuery(id+"F0.imprint","IMPRINT",EDGE,{"derivedFrom":subQ0}),1.0]])]});}
            var Q69;
            {var subQ5=sQuery(id+"F0.wireOp",EDGE,"E4.3.1.11");var subQ6=sQuery(id+"F0.wireOp",EDGE,"E4.3.1.1");var subQ7=makeQuery(id+"F0.imprint","INTERSECT",VERTEX,{"derivedFrom":[subQ6,subQ5]});Q69=makeQuery(id+"F0.imprint","IMPRINT",FACE,{"disambiguationData":[TD([[makeQuery(id+"F0.imprint","IMPRINT",EDGE,{"disambiguationData":[TD([[subQ7,1.0]])],"derivedFrom":subQ6}),-1.0]])]});}
            var Q70;
            {var subQ0=sQuery(id+"F0.wireOp",EDGE,"E4.4.1.12");var subQ1=sQuery(id+"F0.wireOp",EDGE,"E4.3.1.1");var subQ2=makeQuery(id+"F0.imprint","INTERSECT",VERTEX,{"derivedFrom":[subQ1,subQ0]});Q70=makeQuery(id+"F0.imprint","IMPRINT",FACE,{"disambiguationData":[TD([[makeQuery(id+"F0.imprint","IMPRINT",EDGE,{"disambiguationData":[TD([[subQ2,-1.0]])],"derivedFrom":subQ1}),-1.0]])]});}
            var Q71;
            {var subQ5=sQuery(id+"F0.wireOp",EDGE,"E4.3.1.2");var subQ9=sQuery(id+"F0.wireOp",EDGE,"E4.4.1.12");var subQ10=makeQuery(id+"F0.imprint","INTERSECT",VERTEX,{"derivedFrom":[subQ5,subQ9]});Q71=makeQuery(id+"F0.imprint","IMPRINT",FACE,{"disambiguationData":[TD([[makeQuery(id+"F0.imprint","IMPRINT",EDGE,{"disambiguationData":[TD([[subQ10,-1.0]])],"derivedFrom":subQ5}),-1.0]])]});}
            var Q72;
            {var subQ0=sQuery(id+"F0.wireOp",EDGE,"E4.4.1.8");var subQ1=sQuery(id+"F0.wireOp",EDGE,"E4.3.0.0");var subQ2=makeQuery(id+"F0.imprint","INTERSECT",VERTEX,{"derivedFrom":[subQ1,subQ0]});Q72=makeQuery(id+"F0.imprint","IMPRINT",FACE,{"disambiguationData":[TD([[makeQuery(id+"F0.imprint","IMPRINT",EDGE,{"disambiguationData":[TD([[subQ2,1.0]])],"derivedFrom":subQ1}),-1.0]])]});}
            var Q73;
            {var subQ0=sQuery(id+"F0.wireOp",EDGE,"E4.4.1.7");var subQ1=sQuery(id+"F0.wireOp",EDGE,"E4.4.0.0");var subQ2=makeQuery(id+"F0.imprint","INTERSECT",VERTEX,{"derivedFrom":[subQ1,subQ0]});Q73=makeQuery(id+"F0.imprint","IMPRINT",FACE,{"disambiguationData":[TD([[makeQuery(id+"F0.imprint","IMPRINT",EDGE,{"disambiguationData":[TD([[subQ2,-1.0]])],"derivedFrom":subQ1}),-1.0]])]});}
            var Q74;
            {var subQ0=sQuery(id+"F0.wireOp",EDGE,"E4.4.2.7");var subQ1=sQuery(id+"F0.wireOp",EDGE,"E4.4.1.0");var subQ2=makeQuery(id+"F0.imprint","INTERSECT",VERTEX,{"derivedFrom":[subQ1,subQ0]});Q74=makeQuery(id+"F0.imprint","IMPRINT",FACE,{"disambiguationData":[TD([[makeQuery(id+"F0.imprint","IMPRINT",EDGE,{"disambiguationData":[TD([[subQ2,-1.0]])],"derivedFrom":subQ1}),-1.0]])]});}
            var Q75;
            {var subQ5=sQuery(id+"F0.wireOp",EDGE,"E4.4.2.9");var subQ8=sQuery(id+"F0.wireOp",EDGE,"E4.3.2.4");var subQ9=makeQuery(id+"F0.imprint","INTERSECT",VERTEX,{"derivedFrom":[subQ8,subQ5]});Q75=makeQuery(id+"F0.imprint","IMPRINT",FACE,{"disambiguationData":[TD([[makeQuery(id+"F0.imprint","IMPRINT",EDGE,{"disambiguationData":[TD([[subQ9,-1.0]])],"derivedFrom":subQ8}),-1.0]])]});}
            var Q76;
            {var subQ0=sQuery(id+"F0.wireOp",EDGE,"E4.4.3.3");var subQ1=sQuery(id+"F0.wireOp",EDGE,"E4.3.2.4");var subQ2=makeQuery(id+"F0.imprint","INTERSECT",VERTEX,{"derivedFrom":[subQ1,subQ0]});Q76=makeQuery(id+"F0.imprint","IMPRINT",FACE,{"disambiguationData":[TD([[makeQuery(id+"F0.imprint","IMPRINT",EDGE,{"disambiguationData":[TD([[subQ2,1.0]])],"derivedFrom":subQ1}),1.0]])]});}
            var Q77;
            {var subQ0=sQuery(id+"F0.wireOp",EDGE,"E4.4.2.9");var subQ1=sQuery(id+"F0.wireOp",EDGE,"E4.3.2.4");var subQ2=makeQuery(id+"F0.imprint","INTERSECT",VERTEX,{"derivedFrom":[subQ1,subQ0]});Q77=makeQuery(id+"F0.imprint","IMPRINT",FACE,{"disambiguationData":[TD([[makeQuery(id+"F0.imprint","IMPRINT",EDGE,{"disambiguationData":[TD([[subQ2,-1.0]])],"derivedFrom":subQ1}),1.0]])]});}
            var Q78;
            {var subQ0=sQuery(id+"F0.wireOp",EDGE,"E4.4.2.9");var subQ1=sQuery(id+"F0.wireOp",EDGE,"E4.3.2.11");var subQ2=makeQuery(id+"F0.imprint","INTERSECT",VERTEX,{"derivedFrom":[subQ1,subQ0]});Q78=makeQuery(id+"F0.imprint","IMPRINT",FACE,{"disambiguationData":[TD([[makeQuery(id+"F0.imprint","IMPRINT",EDGE,{"disambiguationData":[TD([[subQ2,-1.0]])],"derivedFrom":subQ1}),1.0]])]});}
            var Q79;
            {var subQ1=sQuery(id+"F0.wireOp",EDGE,"E4.4.2.7");var subQ5=sQuery(id+"F0.wireOp",EDGE,"E4.4.2.2");var subQ6=makeQuery(id+"F0.imprint","INTERSECT",VERTEX,{"derivedFrom":[subQ5,subQ1]});Q79=makeQuery(id+"F0.imprint","IMPRINT",FACE,{"disambiguationData":[TD([[makeQuery(id+"F0.imprint","IMPRINT",EDGE,{"disambiguationData":[TD([[subQ6,-1.0]])],"derivedFrom":subQ5}),-1.0]])]});}
            var Q80;
            {var subQ0=sQuery(id+"F0.wireOp",EDGE,"E4.4.2.14");var subQ1=sQuery(id+"F0.wireOp",EDGE,"E4.4.2.5");var subQ2=makeQuery(id+"F0.imprint","INTERSECT",VERTEX,{"derivedFrom":[subQ1,subQ0]});Q80=makeQuery(id+"F0.imprint","IMPRINT",FACE,{"disambiguationData":[TD([[makeQuery(id+"F0.imprint","IMPRINT",EDGE,{"disambiguationData":[TD([[subQ2,1.0]])],"derivedFrom":subQ1}),-1.0]])]});}
            var Q81;
            {var subQ1=sQuery(id+"F0.wireOp",EDGE,"E4.4.2.1");var subQ9=sQuery(id+"F0.wireOp",EDGE,"E4.4.2.13");var subQ10=makeQuery(id+"F0.imprint","INTERSECT",VERTEX,{"derivedFrom":[subQ1,subQ9]});Q81=makeQuery(id+"F0.imprint","IMPRINT",FACE,{"disambiguationData":[TD([[makeQuery(id+"F0.imprint","IMPRINT",EDGE,{"disambiguationData":[TD([[subQ10,-1.0]])],"derivedFrom":subQ1}),-1.0]])]});}
            var Q82;
            {var subQ0=sQuery(id+"F0.wireOp",EDGE,"E5.right");var subQ1=sQuery(id+"F0.wireOp",EDGE,"E4.4.2.1");var subQ2=makeQuery(id+"F0.imprint","INTERSECT",VERTEX,{"derivedFrom":[subQ1,subQ0]});Q82=makeQuery(id+"F0.imprint","IMPRINT",FACE,{"disambiguationData":[TD([[makeQuery(id+"F0.imprint","IMPRINT",EDGE,{"disambiguationData":[TD([[subQ2,1.0]])],"derivedFrom":subQ1}),-1.0]])]});}
            var Q83;
            {var subQ0=sQuery(id+"F0.wireOp",EDGE,"E4.4.2.7");var subQ1=sQuery(id+"F0.wireOp",EDGE,"E4.4.2.1");var subQ2=makeQuery(id+"F0.imprint","INTERSECT",VERTEX,{"derivedFrom":[subQ1,subQ0]});Q83=makeQuery(id+"F0.imprint","IMPRINT",FACE,{"disambiguationData":[TD([[makeQuery(id+"F0.imprint","IMPRINT",EDGE,{"disambiguationData":[TD([[subQ2,-1.0]])],"derivedFrom":subQ1}),-1.0]])]});}
            var Q84;
            {var subQ1=sQuery(id+"F0.wireOp",EDGE,"E4.4.3.7");Q84=makeQuery(id+"F0.imprint","IMPRINT",FACE,{"disambiguationData":[TD([[makeQuery(id+"F0.imprint","IMPRINT",EDGE,{"derivedFrom":subQ1}),1.0]])]});}
            var Q85;
            {var subQ0=sQuery(id+"F0.wireOp",EDGE,"E62.trimOffspring");Q85=makeQuery(id+"F0.imprint","IMPRINT",FACE,{"disambiguationData":[TD([[makeQuery(id+"F0.imprint","IMPRINT",EDGE,{"derivedFrom":subQ0}),-1.0]])]});}
            var Q86;
            {var subQ7=sQuery(id+"F0.wireOp",EDGE,"E4.4.3.1");var subQ10=sQuery(id+"F0.wireOp",EDGE,"E4.4.3.13");var subQ11=makeQuery(id+"F0.imprint","INTERSECT",VERTEX,{"derivedFrom":[subQ7,subQ10]});Q86=makeQuery(id+"F0.imprint","IMPRINT",FACE,{"disambiguationData":[TD([[makeQuery(id+"F0.imprint","IMPRINT",EDGE,{"disambiguationData":[TD([[subQ11,-1.0]])],"derivedFrom":subQ7}),-1.0]])]});}
            var Q87;
            {var subQ0=sQuery(id+"F0.wireOp",EDGE,"E64.trimOffspring");Q87=makeQuery(id+"F0.imprint","IMPRINT",FACE,{"disambiguationData":[TD([[makeQuery(id+"F0.imprint","IMPRINT",EDGE,{"derivedFrom":subQ0}),1.0]])]});}
            var Q88;
            {var subQ0=sQuery(id+"F0.wireOp",EDGE,"E4.3.3.4");Q88=makeQuery(id+"F0.imprint","IMPRINT",FACE,{"disambiguationData":[TD([[makeQuery(id+"F0.imprint","IMPRINT",EDGE,{"derivedFrom":subQ0}),1.0]])]});}
            var Q89;
            {var subQ5=sQuery(id+"F0.wireOp",EDGE,"E68");Q89=makeQuery(id+"F0.imprint","IMPRINT",FACE,{"disambiguationData":[TD([[makeQuery(id+"F0.imprint","IMPRINT",EDGE,{"derivedFrom":subQ5}),1.0]])]});}
            var Q90;
            {var subQ0=sQuery(id+"F0.wireOp",EDGE,"E4.3.3.7");var subQ1=sQuery(id+"F0.wireOp",EDGE,"E4.3.3.1");var subQ2=makeQuery(id+"F0.imprint","INTERSECT",VERTEX,{"derivedFrom":[subQ1,subQ0]});Q90=makeQuery(id+"F0.imprint","IMPRINT",FACE,{"disambiguationData":[TD([[makeQuery(id+"F0.imprint","IMPRINT",EDGE,{"disambiguationData":[TD([[subQ2,-1.0]])],"derivedFrom":subQ1}),-1.0]])]});}
            var Q91;
            {var subQ1=sQuery(id+"F0.wireOp",EDGE,"E4.3.3.1");var subQ9=sQuery(id+"F0.wireOp",EDGE,"E4.3.3.13");var subQ10=makeQuery(id+"F0.imprint","INTERSECT",VERTEX,{"derivedFrom":[subQ1,subQ9]});Q91=makeQuery(id+"F0.imprint","IMPRINT",FACE,{"disambiguationData":[TD([[makeQuery(id+"F0.imprint","IMPRINT",EDGE,{"disambiguationData":[TD([[subQ10,-1.0]])],"derivedFrom":subQ1}),-1.0]])]});}
            var Q92;
            {var subQ5=sQuery(id+"F0.wireOp",EDGE,"E60.trimOffspring");var subQ8=sQuery(id+"F0.wireOp",EDGE,"E4.3.3.5");var subQ9=makeQuery(id+"F0.imprint","INTERSECT",VERTEX,{"derivedFrom":[subQ8,subQ5]});Q92=makeQuery(id+"F0.imprint","IMPRINT",FACE,{"disambiguationData":[TD([[makeQuery(id+"F0.imprint","IMPRINT",EDGE,{"disambiguationData":[TD([[subQ9,-1.0]])],"derivedFrom":subQ8}),1.0]])]});}
            var Q93;
            {var subQ0=sQuery(id+"F0.wireOp",EDGE,"E5.top");var subQ1=sQuery(id+"F0.wireOp",EDGE,"E4.3.3.5");var subQ2=makeQuery(id+"F0.imprint","INTERSECT",VERTEX,{"derivedFrom":[subQ1,subQ0]});Q93=makeQuery(id+"F0.imprint","IMPRINT",FACE,{"disambiguationData":[TD([[makeQuery(id+"F0.imprint","IMPRINT",EDGE,{"disambiguationData":[TD([[subQ2,1.0]])],"derivedFrom":subQ1}),-1.0]])]});}
            var Q94;
            {var subQ0=sQuery(id+"F0.wireOp",EDGE,"E60.trimOffspring");var subQ1=sQuery(id+"F0.wireOp",EDGE,"E4.3.3.5");var subQ2=makeQuery(id+"F0.imprint","INTERSECT",VERTEX,{"derivedFrom":[subQ1,subQ0]});Q94=makeQuery(id+"F0.imprint","IMPRINT",FACE,{"disambiguationData":[TD([[makeQuery(id+"F0.imprint","IMPRINT",EDGE,{"disambiguationData":[TD([[subQ2,-1.0]])],"derivedFrom":subQ1}),-1.0]])]});}
            var Q95;
            {var subQ0=sQuery(id+"F0.wireOp",EDGE,"E60.trimOffspring");var subQ1=sQuery(id+"F0.wireOp",EDGE,"E4.2.3.11");var subQ2=makeQuery(id+"F0.imprint","INTERSECT",VERTEX,{"derivedFrom":[subQ1,subQ0]});Q95=makeQuery(id+"F0.imprint","IMPRINT",FACE,{"disambiguationData":[TD([[makeQuery(id+"F0.imprint","IMPRINT",EDGE,{"disambiguationData":[TD([[subQ2,-1.0]])],"derivedFrom":subQ1}),1.0]])]});}
            var Q96;
            {var subQ0=sQuery(id+"F0.wireOp",EDGE,"E4.3.3.7");var subQ1=sQuery(id+"F0.wireOp",EDGE,"E4.3.2.0");var subQ2=makeQuery(id+"F0.imprint","INTERSECT",VERTEX,{"derivedFrom":[subQ1,subQ0]});Q96=makeQuery(id+"F0.imprint","IMPRINT",FACE,{"disambiguationData":[TD([[makeQuery(id+"F0.imprint","IMPRINT",EDGE,{"disambiguationData":[TD([[subQ2,-1.0]])],"derivedFrom":subQ1}),-1.0]])]});}
            var Q97;
            {var subQ0=sQuery(id+"F0.wireOp",EDGE,"E4.3.3.7");var subQ1=sQuery(id+"F0.wireOp",EDGE,"E4.3.2.0");var subQ2=makeQuery(id+"F0.imprint","INTERSECT",VERTEX,{"derivedFrom":[subQ1,subQ0]});Q97=makeQuery(id+"F0.imprint","IMPRINT",FACE,{"disambiguationData":[TD([[makeQuery(id+"F0.imprint","IMPRINT",EDGE,{"disambiguationData":[TD([[subQ2,-1.0]])],"derivedFrom":subQ1}),1.0]])]});}
            var Q98;
            {var subQ7=sQuery(id+"F0.wireOp",EDGE,"E4.3.3.3");var subQ9=sQuery(id+"F0.wireOp",EDGE,"E4.3.2.5");var subQ10=makeQuery(id+"F0.imprint","INTERSECT",VERTEX,{"derivedFrom":[subQ9,subQ7]});Q98=makeQuery(id+"F0.imprint","IMPRINT",FACE,{"disambiguationData":[TD([[makeQuery(id+"F0.imprint","IMPRINT",EDGE,{"disambiguationData":[TD([[subQ10,-1.0]])],"derivedFrom":subQ9}),1.0]])]});}
            var Q99;
            {var subQ0=sQuery(id+"F0.wireOp",EDGE,"E4.3.2.13");var subQ1=sQuery(id+"F0.wireOp",EDGE,"E4.3.2.0");var subQ2=makeQuery(id+"F0.imprint","INTERSECT",VERTEX,{"derivedFrom":[subQ1,subQ0]});Q99=makeQuery(id+"F0.imprint","IMPRINT",FACE,{"disambiguationData":[TD([[makeQuery(id+"F0.imprint","IMPRINT",EDGE,{"disambiguationData":[TD([[subQ2,-1.0]])],"derivedFrom":subQ1}),1.0]])]});}
            var Q100;
            {var subQ5=sQuery(id+"F0.wireOp",EDGE,"E69");Q100=makeQuery(id+"F0.imprint","IMPRINT",FACE,{"disambiguationData":[TD([[makeQuery(id+"F0.imprint","IMPRINT",EDGE,{"derivedFrom":subQ5}),-1.0]])]});}
            var Q101;
            {var subQ0=sQuery(id+"F0.wireOp",EDGE,"E4.3.2.14");var subQ1=sQuery(id+"F0.wireOp",EDGE,"E4.3.2.5");var subQ2=makeQuery(id+"F0.imprint","INTERSECT",VERTEX,{"derivedFrom":[subQ1,subQ0]});Q101=makeQuery(id+"F0.imprint","IMPRINT",FACE,{"disambiguationData":[TD([[makeQuery(id+"F0.imprint","IMPRINT",EDGE,{"disambiguationData":[TD([[subQ2,-1.0]])],"derivedFrom":subQ1}),-1.0]])]});}
            var Q102;
            {var subQ0=sQuery(id+"F0.wireOp",EDGE,"E4.3.3.3");var subQ1=sQuery(id+"F0.wireOp",EDGE,"E4.3.2.5");var subQ2=makeQuery(id+"F0.imprint","INTERSECT",VERTEX,{"derivedFrom":[subQ1,subQ0]});Q102=makeQuery(id+"F0.imprint","IMPRINT",FACE,{"disambiguationData":[TD([[makeQuery(id+"F0.imprint","IMPRINT",EDGE,{"disambiguationData":[TD([[subQ2,-1.0]])],"derivedFrom":subQ1}),-1.0]])]});}
            var Q103;
            {var subQ0=sQuery(id+"F0.wireOp",EDGE,"E4.3.3.3");var subQ1=sQuery(id+"F0.wireOp",EDGE,"E4.3.2.13");var subQ2=makeQuery(id+"F0.imprint","INTERSECT",VERTEX,{"derivedFrom":[subQ1,subQ0]});Q103=makeQuery(id+"F0.imprint","IMPRINT",FACE,{"disambiguationData":[TD([[makeQuery(id+"F0.imprint","IMPRINT",EDGE,{"disambiguationData":[TD([[subQ2,-1.0]])],"derivedFrom":subQ1}),-1.0]])]});}
            var Q104;
            {var subQ0=sQuery(id+"F0.wireOp",EDGE,"E49.trimOffspring");var subQ1=sQuery(id+"F0.wireOp",EDGE,"E4.3.3.3");var subQ2=makeQuery(id+"F0.imprint","INTERSECT",VERTEX,{"derivedFrom":[subQ1,subQ0]});Q104=makeQuery(id+"F0.imprint","IMPRINT",FACE,{"disambiguationData":[TD([[makeQuery(id+"F0.imprint","IMPRINT",EDGE,{"disambiguationData":[TD([[subQ2,-1.0]])],"derivedFrom":subQ1}),-1.0]])]});}
            var Q105;
            {var subQ0=sQuery(id+"F0.wireOp",EDGE,"E4.3.3.12");var subQ1=sQuery(id+"F0.wireOp",EDGE,"E4.3.3.3");var subQ2=makeQuery(id+"F0.imprint","INTERSECT",VERTEX,{"derivedFrom":[subQ1,subQ0]});Q105=makeQuery(id+"F0.imprint","IMPRINT",FACE,{"disambiguationData":[TD([[makeQuery(id+"F0.imprint","IMPRINT",EDGE,{"disambiguationData":[TD([[subQ2,-1.0]])],"derivedFrom":subQ1}),-1.0]])]});}
            var Q106;
            {var subQ0=sQuery(id+"F0.wireOp",EDGE,"E54.trimOffspring");var subQ9=sQuery(id+"F0.wireOp",EDGE,"E4.3.3.8");var subQ10=makeQuery(id+"F0.imprint","INTERSECT",VERTEX,{"derivedFrom":[subQ9,subQ0]});Q106=makeQuery(id+"F0.imprint","IMPRINT",FACE,{"disambiguationData":[TD([[makeQuery(id+"F0.imprint","IMPRINT",EDGE,{"disambiguationData":[TD([[subQ10,-1.0]])],"derivedFrom":subQ9}),1.0]])]});}
            var Q107;
            {var subQ0=sQuery(id+"F0.wireOp",EDGE,"E48.trimOffspring");var subQ1=sQuery(id+"F0.wireOp",EDGE,"E4.3.2.14");var subQ2=makeQuery(id+"F0.imprint","INTERSECT",VERTEX,{"derivedFrom":[subQ1,subQ0]});Q107=makeQuery(id+"F0.imprint","IMPRINT",FACE,{"disambiguationData":[TD([[makeQuery(id+"F0.imprint","IMPRINT",EDGE,{"disambiguationData":[TD([[subQ2,1.0]])],"derivedFrom":subQ1}),-1.0]])]});}
            var Q108;
            {var subQ0=sQuery(id+"F0.wireOp",EDGE,"E54.trimOffspring");var subQ1=sQuery(id+"F0.wireOp",EDGE,"E4.3.3.8");var subQ2=makeQuery(id+"F0.imprint","INTERSECT",VERTEX,{"derivedFrom":[subQ1,subQ0]});Q108=makeQuery(id+"F0.imprint","IMPRINT",FACE,{"disambiguationData":[TD([[makeQuery(id+"F0.imprint","IMPRINT",EDGE,{"disambiguationData":[TD([[subQ2,-1.0]])],"derivedFrom":subQ1}),-1.0]])]});}
            var Q109;
            {var subQ0=sQuery(id+"F0.wireOp",EDGE,"E54.trimOffspring");var subQ1=sQuery(id+"F0.wireOp",EDGE,"E4.2.3.15");var subQ2=makeQuery(id+"F0.imprint","INTERSECT",VERTEX,{"derivedFrom":[subQ1,subQ0]});Q109=makeQuery(id+"F0.imprint","IMPRINT",FACE,{"disambiguationData":[TD([[makeQuery(id+"F0.imprint","IMPRINT",EDGE,{"disambiguationData":[TD([[subQ2,-1.0]])],"derivedFrom":subQ1}),1.0]])]});}
            var Q110;
            {var subQ0=sQuery(id+"F0.wireOp",EDGE,"E4.3.3.8");var subQ1=sQuery(id+"F0.wireOp",EDGE,"E4.2.3.1");var subQ2=makeQuery(id+"F0.imprint","INTERSECT",VERTEX,{"derivedFrom":[subQ1,subQ0]});Q110=makeQuery(id+"F0.imprint","IMPRINT",FACE,{"disambiguationData":[TD([[makeQuery(id+"F0.imprint","IMPRINT",EDGE,{"disambiguationData":[TD([[subQ2,1.0]])],"derivedFrom":subQ1}),1.0]])]});}
            var Q111;
            {var subQ0=sQuery(id+"F0.wireOp",EDGE,"E4.2.3.7");Q111=makeQuery(id+"F0.imprint","IMPRINT",FACE,{"disambiguationData":[TD([[makeQuery(id+"F0.imprint","IMPRINT",EDGE,{"derivedFrom":subQ0}),1.0]])]});}
            var Q112;
            {var subQ0=sQuery(id+"F0.wireOp",EDGE,"E4.2.3.3");var subQ1=sQuery(id+"F0.wireOp",EDGE,"E4.2.2.5");var subQ2=makeQuery(id+"F0.imprint","INTERSECT",VERTEX,{"derivedFrom":[subQ1,subQ0]});Q112=makeQuery(id+"F0.imprint","IMPRINT",FACE,{"disambiguationData":[TD([[makeQuery(id+"F0.imprint","IMPRINT",EDGE,{"disambiguationData":[TD([[subQ2,1.0]])],"derivedFrom":subQ1}),-1.0]])]});}
            var Q113;
            {var subQ0=sQuery(id+"F0.wireOp",EDGE,"E4.2.3.3");var subQ1=sQuery(id+"F0.wireOp",EDGE,"E4.1.2.4");var subQ2=makeQuery(id+"F0.imprint","INTERSECT",VERTEX,{"derivedFrom":[subQ1,subQ0]});Q113=makeQuery(id+"F0.imprint","IMPRINT",FACE,{"disambiguationData":[TD([[makeQuery(id+"F0.imprint","IMPRINT",EDGE,{"disambiguationData":[TD([[subQ2,1.0]])],"derivedFrom":subQ1}),1.0]])]});}
            var Q114;
            {var subQ0=sQuery(id+"F0.wireOp",EDGE,"E4.2.3.4");Q114=makeQuery(id+"F0.imprint","IMPRINT",FACE,{"disambiguationData":[TD([[makeQuery(id+"F0.imprint","IMPRINT",EDGE,{"derivedFrom":subQ0}),1.0]])]});}
            var Q115;
            {var subQ4=sQuery(id+"F0.wireOp",EDGE,"E56.trimOffspring");Q115=makeQuery(id+"F0.imprint","IMPRINT",FACE,{"disambiguationData":[TD([[makeQuery(id+"F0.imprint","IMPRINT",EDGE,{"derivedFrom":subQ4}),1.0]])]});}
            var Q116;
            {var subQ0=sQuery(id+"F0.wireOp",EDGE,"E4.1.3.4");Q116=makeQuery(id+"F0.imprint","IMPRINT",FACE,{"disambiguationData":[TD([[makeQuery(id+"F0.imprint","IMPRINT",EDGE,{"derivedFrom":subQ0}),1.0]])]});}
            var Q117;
            {var subQ0=sQuery(id+"F0.wireOp",EDGE,"E4.2.3.12");var subQ1=sQuery(id+"F0.wireOp",EDGE,"E4.1.3.1");var subQ2=makeQuery(id+"F0.imprint","INTERSECT",VERTEX,{"derivedFrom":[subQ1,subQ0]});Q117=makeQuery(id+"F0.imprint","IMPRINT",FACE,{"disambiguationData":[TD([[makeQuery(id+"F0.imprint","IMPRINT",EDGE,{"disambiguationData":[TD([[subQ2,1.0]])],"derivedFrom":subQ1}),-1.0]])]});}
            var Q118;
            {var subQ0=sQuery(id+"F0.wireOp",EDGE,"E72");Q118=makeQuery(id+"F0.imprint","IMPRINT",FACE,{"disambiguationData":[TD([[makeQuery(id+"F0.imprint","IMPRINT",EDGE,{"derivedFrom":subQ0}),1.0]])]});}
            var Q119;
            {var subQ5=sQuery(id+"F0.wireOp",EDGE,"E4.1.3.15");var subQ8=sQuery(id+"F0.wireOp",EDGE,"E4.1.3.3");var subQ9=makeQuery(id+"F0.imprint","INTERSECT",VERTEX,{"derivedFrom":[subQ8,subQ5]});Q119=makeQuery(id+"F0.imprint","IMPRINT",FACE,{"disambiguationData":[TD([[makeQuery(id+"F0.imprint","IMPRINT",EDGE,{"disambiguationData":[TD([[subQ9,1.0]])],"derivedFrom":subQ8}),-1.0]])]});}
            var Q120;
            {var subQ0=sQuery(id+"F0.wireOp",EDGE,"E4.1.2.14");var subQ1=sQuery(id+"F0.wireOp",EDGE,"E4.1.2.13");var subQ2=makeQuery(id+"F0.imprint","INTERSECT",VERTEX,{"derivedFrom":[subQ1,subQ0]});Q120=makeQuery(id+"F0.imprint","IMPRINT",FACE,{"disambiguationData":[TD([[makeQuery(id+"F0.imprint","IMPRINT",EDGE,{"disambiguationData":[TD([[subQ2,-1.0]])],"derivedFrom":subQ1}),1.0]])]});}
            var Q121;
            {var subQ0=sQuery(id+"F0.wireOp",EDGE,"E4.1.3.3");var subQ1=sQuery(id+"F0.wireOp",EDGE,"E4.1.2.13");var subQ2=makeQuery(id+"F0.imprint","INTERSECT",VERTEX,{"derivedFrom":[subQ1,subQ0]});Q121=makeQuery(id+"F0.imprint","IMPRINT",FACE,{"disambiguationData":[TD([[makeQuery(id+"F0.imprint","IMPRINT",EDGE,{"disambiguationData":[TD([[subQ2,-1.0]])],"derivedFrom":subQ1}),1.0]])]});}
            var Q122;
            {var subQ1=sQuery(id+"F0.wireOp",EDGE,"E4.1.2.0");var subQ5=sQuery(id+"F0.wireOp",EDGE,"E4.1.2.13");var subQ6=makeQuery(id+"F0.imprint","INTERSECT",VERTEX,{"derivedFrom":[subQ1,subQ5]});Q122=makeQuery(id+"F0.imprint","IMPRINT",FACE,{"disambiguationData":[TD([[makeQuery(id+"F0.imprint","IMPRINT",EDGE,{"disambiguationData":[TD([[subQ6,-1.0]])],"derivedFrom":subQ1}),1.0]])]});}
            var Q123;
            {var subQ1=sQuery(id+"F0.wireOp",EDGE,"E4.1.2.0");var subQ3=sQuery(id+"F0.wireOp",EDGE,"E4.1.3.7");var subQ4=makeQuery(id+"F0.imprint","INTERSECT",VERTEX,{"derivedFrom":[subQ1,subQ3]});Q123=makeQuery(id+"F0.imprint","IMPRINT",FACE,{"disambiguationData":[TD([[makeQuery(id+"F0.imprint","IMPRINT",EDGE,{"disambiguationData":[TD([[subQ4,1.0]])],"derivedFrom":subQ3}),1.0]])]});}
            var Q124;
            {var subQ3=sQuery(id+"F0.wireOp",EDGE,"E4.1.3.7");var subQ5=sQuery(id+"F0.wireOp",EDGE,"E4.1.3.1");var subQ6=makeQuery(id+"F0.imprint","INTERSECT",VERTEX,{"derivedFrom":[subQ5,subQ3]});Q124=makeQuery(id+"F0.imprint","IMPRINT",FACE,{"disambiguationData":[TD([[makeQuery(id+"F0.imprint","IMPRINT",EDGE,{"disambiguationData":[TD([[subQ6,-1.0]])],"derivedFrom":subQ5}),1.0]])]});}
            var Q125;
            {var subQ0=sQuery(id+"F0.wireOp",EDGE,"E4.1.3.7");var subQ1=sQuery(id+"F0.wireOp",EDGE,"E4.1.3.1");var subQ2=makeQuery(id+"F0.imprint","INTERSECT",VERTEX,{"derivedFrom":[subQ1,subQ0]});Q125=makeQuery(id+"F0.imprint","IMPRINT",FACE,{"disambiguationData":[TD([[makeQuery(id+"F0.imprint","IMPRINT",EDGE,{"disambiguationData":[TD([[subQ2,-1.0]])],"derivedFrom":subQ1}),-1.0]])]});}
            var Q126;
            {var subQ1=sQuery(id+"F0.wireOp",EDGE,"E4.1.3.7");var subQ7=sQuery(id+"F0.wireOp",EDGE,"E4.1.3.2");var subQ8=makeQuery(id+"F0.imprint","INTERSECT",VERTEX,{"derivedFrom":[subQ7,subQ1]});Q126=makeQuery(id+"F0.imprint","IMPRINT",FACE,{"disambiguationData":[TD([[makeQuery(id+"F0.imprint","IMPRINT",EDGE,{"disambiguationData":[TD([[subQ8,-1.0]])],"derivedFrom":subQ7}),-1.0]])]});}
            var Q127;
            {var subQ6=sQuery(id+"F0.wireOp",EDGE,"E4.1.3.1");var subQ9=sQuery(id+"F0.wireOp",EDGE,"E4.1.3.13");var subQ10=makeQuery(id+"F0.imprint","INTERSECT",VERTEX,{"derivedFrom":[subQ6,subQ9]});Q127=makeQuery(id+"F0.imprint","IMPRINT",FACE,{"disambiguationData":[TD([[makeQuery(id+"F0.imprint","IMPRINT",EDGE,{"disambiguationData":[TD([[subQ10,-1.0]])],"derivedFrom":subQ6}),-1.0]])]});}
            var Q128;
            {var subQ0=sQuery(id+"F0.wireOp",EDGE,"E4.1.3.9");var subQ1=sQuery(id+"F0.wireOp",EDGE,"E4.1.3.5");var subQ2=makeQuery(id+"F0.imprint","INTERSECT",VERTEX,{"derivedFrom":[subQ1,subQ0]});Q128=makeQuery(id+"F0.imprint","IMPRINT",FACE,{"disambiguationData":[TD([[makeQuery(id+"F0.imprint","IMPRINT",EDGE,{"disambiguationData":[TD([[subQ2,-1.0]])],"derivedFrom":subQ1}),-1.0]])]});}
            var Q129;
            {var subQ0=sQuery(id+"F0.wireOp",EDGE,"E4.1.3.9");var subQ1=sQuery(id+"F0.wireOp",EDGE,"E4.0.3.11");var subQ2=makeQuery(id+"F0.imprint","INTERSECT",VERTEX,{"derivedFrom":[subQ1,subQ0]});Q129=makeQuery(id+"F0.imprint","IMPRINT",FACE,{"disambiguationData":[TD([[makeQuery(id+"F0.imprint","IMPRINT",EDGE,{"disambiguationData":[TD([[subQ2,-1.0]])],"derivedFrom":subQ1}),1.0]])]});}
            var Q130;
            {var subQ0=sQuery(id+"F0.wireOp",EDGE,"E5.top");var subQ1=sQuery(id+"F0.wireOp",EDGE,"E4.1.3.5");var subQ2=makeQuery(id+"F0.imprint","INTERSECT",VERTEX,{"derivedFrom":[subQ1,subQ0]});Q130=makeQuery(id+"F0.imprint","IMPRINT",FACE,{"disambiguationData":[TD([[makeQuery(id+"F0.imprint","IMPRINT",EDGE,{"disambiguationData":[TD([[subQ2,1.0]])],"derivedFrom":subQ1}),-1.0]])]});}
            var Q131;
            {var subQ0=sQuery(id+"F0.wireOp",EDGE,"E4.1.2.12");var subQ1=sQuery(id+"F0.wireOp",EDGE,"E4.0.2.1");var subQ2=makeQuery(id+"F0.imprint","INTERSECT",VERTEX,{"derivedFrom":[subQ1,subQ0]});Q131=makeQuery(id+"F0.imprint","IMPRINT",FACE,{"disambiguationData":[TD([[makeQuery(id+"F0.imprint","IMPRINT",EDGE,{"disambiguationData":[TD([[subQ2,1.0]])],"derivedFrom":subQ1}),-1.0]])]});}
            var Q132;
            {var subQ0=sQuery(id+"F0.wireOp",EDGE,"E4.0.2.7");var subQ1=sQuery(id+"F0.wireOp",EDGE,"E4.0.2.1");var subQ2=makeQuery(id+"F0.imprint","INTERSECT",VERTEX,{"derivedFrom":[subQ1,subQ0]});Q132=makeQuery(id+"F0.imprint","IMPRINT",FACE,{"disambiguationData":[TD([[makeQuery(id+"F0.imprint","IMPRINT",EDGE,{"disambiguationData":[TD([[subQ2,-1.0]])],"derivedFrom":subQ1}),-1.0]])]});}
            var Q133;
            {var subQ1=sQuery(id+"F0.wireOp",EDGE,"E4.0.2.7");var subQ3=sQuery(id+"F0.wireOp",EDGE,"E4.0.2.2");var subQ4=makeQuery(id+"F0.imprint","INTERSECT",VERTEX,{"derivedFrom":[subQ3,subQ1]});Q133=makeQuery(id+"F0.imprint","IMPRINT",FACE,{"disambiguationData":[TD([[makeQuery(id+"F0.imprint","IMPRINT",EDGE,{"disambiguationData":[TD([[subQ4,-1.0]])],"derivedFrom":subQ3}),-1.0]])]});}
            var Q134;
            {var subQ1=sQuery(id+"F0.wireOp",EDGE,"E4.0.2.1");var subQ9=sQuery(id+"F0.wireOp",EDGE,"E4.0.2.13");var subQ10=makeQuery(id+"F0.imprint","INTERSECT",VERTEX,{"derivedFrom":[subQ1,subQ9]});Q134=makeQuery(id+"F0.imprint","IMPRINT",FACE,{"disambiguationData":[TD([[makeQuery(id+"F0.imprint","IMPRINT",EDGE,{"disambiguationData":[TD([[subQ10,-1.0]])],"derivedFrom":subQ1}),-1.0]])]});}
            var Q135;
            {var subQ0=sQuery(id+"F0.wireOp",EDGE,"E5.left");var subQ1=sQuery(id+"F0.wireOp",EDGE,"E4.0.2.9");var subQ2=makeQuery(id+"F0.imprint","INTERSECT",VERTEX,{"derivedFrom":[subQ1,subQ0]});Q135=makeQuery(id+"F0.imprint","IMPRINT",FACE,{"disambiguationData":[TD([[makeQuery(id+"F0.imprint","IMPRINT",EDGE,{"disambiguationData":[TD([[subQ2,-1.0]])],"derivedFrom":subQ1}),-1.0]])]});}
            var Q136;
            {var subQ0=sQuery(id+"F0.wireOp",EDGE,"E4.0.2.9");var subQ1=sQuery(id+"F0.wireOp",EDGE,"E4.0.2.5");var subQ2=makeQuery(id+"F0.imprint","INTERSECT",VERTEX,{"derivedFrom":[subQ1,subQ0]});Q136=makeQuery(id+"F0.imprint","IMPRINT",FACE,{"disambiguationData":[TD([[makeQuery(id+"F0.imprint","IMPRINT",EDGE,{"disambiguationData":[TD([[subQ2,-1.0]])],"derivedFrom":subQ1}),-1.0]])]});}
            var Q137;
            {var subQ0=sQuery(id+"F0.wireOp",EDGE,"E4.1.2.14");var subQ1=sQuery(id+"F0.wireOp",EDGE,"E4.0.2.4");var subQ2=makeQuery(id+"F0.imprint","INTERSECT",VERTEX,{"derivedFrom":[subQ1,subQ0]});Q137=makeQuery(id+"F0.imprint","IMPRINT",FACE,{"disambiguationData":[TD([[makeQuery(id+"F0.imprint","IMPRINT",EDGE,{"disambiguationData":[TD([[subQ2,-1.0]])],"derivedFrom":subQ1}),1.0]])]});}
            var Q138;
            {var subQ0=sQuery(id+"F0.wireOp",EDGE,"E4.1.3.3");var subQ1=sQuery(id+"F0.wireOp",EDGE,"E4.0.2.11");var subQ2=makeQuery(id+"F0.imprint","INTERSECT",VERTEX,{"derivedFrom":[subQ1,subQ0]});Q138=makeQuery(id+"F0.imprint","IMPRINT",FACE,{"disambiguationData":[TD([[makeQuery(id+"F0.imprint","IMPRINT",EDGE,{"disambiguationData":[TD([[subQ2,-1.0]])],"derivedFrom":subQ1}),1.0]])]});}
            var Q139;
            {var subQ5=sQuery(id+"F0.wireOp",EDGE,"E4.0.2.11");var subQ7=sQuery(id+"F0.wireOp",EDGE,"E4.0.2.0");var subQ8=makeQuery(id+"F0.imprint","INTERSECT",VERTEX,{"derivedFrom":[subQ7,subQ5]});Q139=makeQuery(id+"F0.imprint","IMPRINT",FACE,{"disambiguationData":[TD([[makeQuery(id+"F0.imprint","IMPRINT",EDGE,{"disambiguationData":[TD([[subQ8,1.0]])],"derivedFrom":subQ7}),1.0]])]});}
            var Q140;
            {var subQ6=sQuery(id+"F0.wireOp",EDGE,"E4.1.3.3");var subQ8=sQuery(id+"F0.wireOp",EDGE,"E4.0.2.4");var subQ9=makeQuery(id+"F0.imprint","INTERSECT",VERTEX,{"derivedFrom":[subQ8,subQ6]});Q140=makeQuery(id+"F0.imprint","IMPRINT",FACE,{"disambiguationData":[TD([[makeQuery(id+"F0.imprint","IMPRINT",EDGE,{"disambiguationData":[TD([[subQ9,-1.0]])],"derivedFrom":subQ8}),-1.0]])]});}
            var Q141;
            {var subQ0=sQuery(id+"F0.wireOp",EDGE,"E4.1.3.12");var subQ1=sQuery(id+"F0.wireOp",EDGE,"E4.0.2.0");var subQ2=makeQuery(id+"F0.imprint","INTERSECT",VERTEX,{"derivedFrom":[subQ1,subQ0]});Q141=makeQuery(id+"F0.imprint","IMPRINT",FACE,{"disambiguationData":[TD([[makeQuery(id+"F0.imprint","IMPRINT",EDGE,{"disambiguationData":[TD([[subQ2,-1.0]])],"derivedFrom":subQ1}),1.0]])]});}
            var Q142;
            {var subQ0=sQuery(id+"F0.wireOp",EDGE,"E4.1.3.3");var subQ1=sQuery(id+"F0.wireOp",EDGE,"E4.0.2.4");var subQ2=makeQuery(id+"F0.imprint","INTERSECT",VERTEX,{"derivedFrom":[subQ1,subQ0]});Q142=makeQuery(id+"F0.imprint","IMPRINT",FACE,{"disambiguationData":[TD([[makeQuery(id+"F0.imprint","IMPRINT",EDGE,{"disambiguationData":[TD([[subQ2,-1.0]])],"derivedFrom":subQ1}),1.0]])]});}
            var Q143;
            {var subQ0=sQuery(id+"F0.wireOp",EDGE,"E4.0.3.15");var subQ1=sQuery(id+"F0.wireOp",EDGE,"E4.0.2.0");var subQ2=makeQuery(id+"F0.imprint","INTERSECT",VERTEX,{"derivedFrom":[subQ1,subQ0]});Q143=makeQuery(id+"F0.imprint","IMPRINT",FACE,{"disambiguationData":[TD([[makeQuery(id+"F0.imprint","IMPRINT",EDGE,{"disambiguationData":[TD([[subQ2,-1.0]])],"derivedFrom":subQ1}),1.0]])]});}
            var Q144;
            {var subQ0=sQuery(id+"F0.wireOp",EDGE,"E4.1.3.12");var subQ1=sQuery(id+"F0.wireOp",EDGE,"E4.0.2.0");var subQ2=makeQuery(id+"F0.imprint","INTERSECT",VERTEX,{"derivedFrom":[subQ1,subQ0]});Q144=makeQuery(id+"F0.imprint","IMPRINT",FACE,{"disambiguationData":[TD([[makeQuery(id+"F0.imprint","IMPRINT",EDGE,{"disambiguationData":[TD([[subQ2,-1.0]])],"derivedFrom":subQ1}),-1.0]])]});}
            var Q145;
            {var subQ0=sQuery(id+"F0.wireOp",EDGE,"E4.0.3.7");Q145=makeQuery(id+"F0.imprint","IMPRINT",FACE,{"disambiguationData":[TD([[makeQuery(id+"F0.imprint","IMPRINT",EDGE,{"derivedFrom":subQ0}),1.0]])]});}
            var Q146;
            {var subQ0=sQuery(id+"F0.wireOp",EDGE,"E4.0.3.4");Q146=makeQuery(id+"F0.imprint","IMPRINT",FACE,{"disambiguationData":[TD([[makeQuery(id+"F0.imprint","IMPRINT",EDGE,{"derivedFrom":subQ0}),1.0]])]});}
            var Q147;
            {var subQ1=sQuery(id+"F0.wireOp",EDGE,"E50.trimOffspring");Q147=makeQuery(id+"F0.imprint","IMPRINT",FACE,{"disambiguationData":[TD([[makeQuery(id+"F0.imprint","IMPRINT",EDGE,{"derivedFrom":subQ1}),1.0]])]});}
            var Q148;
            {var subQ0=sQuery(id+"F0.wireOp",EDGE,"E4.0.3.9");Q148=makeQuery(id+"F0.imprint","IMPRINT",FACE,{"disambiguationData":[TD([[makeQuery(id+"F0.imprint","IMPRINT",EDGE,{"derivedFrom":subQ0}),-1.0]])]});}
            var Q149;
            {var subQ5=sQuery(id+"F0.wireOp",EDGE,"E74");Q149=makeQuery(id+"F0.imprint","IMPRINT",FACE,{"disambiguationData":[TD([[makeQuery(id+"F0.imprint","IMPRINT",EDGE,{"derivedFrom":subQ5}),1.0]])]});}
            var Q150;
            {var subQ5=sQuery(id+"F0.wireOp",EDGE,"E75");Q150=makeQuery(id+"F0.imprint","IMPRINT",FACE,{"disambiguationData":[TD([[makeQuery(id+"F0.imprint","IMPRINT",EDGE,{"derivedFrom":subQ5}),-1.0]])]});}
            extrude(context, id + "F1", {"entities" : qUnion([Q0, Q1, Q2, Q3, Q4, Q5, Q6, Q7, Q8, Q9, Q10, Q11, Q12, Q13, Q14, Q15, Q16, Q17, Q18, Q19, Q20, Q21, Q22, Q23, Q24, Q25, Q26, Q27, Q28, Q29, Q30, Q31, Q32, Q33, Q34, Q35, Q36, Q37, Q38, Q39, Q40, Q41, Q42, Q43, Q44, Q45, Q46, Q47, Q48, Q49, Q50, Q51, Q52, Q53, Q54, Q55, Q56, Q57, Q58, Q59, Q60, Q61, Q62, Q63, Q64, Q65, Q66, Q67, Q68, Q69, Q70, Q71, Q72, Q73, Q74, Q75, Q76, Q77, Q78, Q79, Q80, Q81, Q82, Q83, Q84, Q85, Q86, Q87, Q88, Q89, Q90, Q91, Q92, Q93, Q94, Q95, Q96, Q97, Q98, Q99, Q100, Q101, Q102, Q103, Q104, Q105, Q106, Q107, Q108, Q109, Q110, Q111, Q112, Q113, Q114, Q115, Q116, Q117, Q118, Q119, Q120, Q121, Q122, Q123, Q124, Q125, Q126, Q127, Q128, Q129, Q130, Q131, Q132, Q133, Q134, Q135, Q136, Q137, Q138, Q139, Q140, Q141, Q142, Q143, Q144, Q145, Q146, Q147, Q148, Q149, Q150]), "oppositeDirection" : true, "depth" : 3.17 * mm, "offsetDistance" : 25.4 * mm});
        }
        {
            var Q0;
            {var subQ0=sQuery(id+"F0.wireOp",EDGE,"E4.0.1.7");Q0=makeQuery(id+"F0.imprint","IMPRINT",FACE,{"disambiguationData":[TD([[makeQuery(id+"F0.imprint","IMPRINT",EDGE,{"derivedFrom":subQ0}),-1.0]])]});}
            var Q1;
            {var subQ0=sQuery(id+"F0.wireOp",EDGE,"E4.0.1.15");Q1=makeQuery(id+"F0.imprint","IMPRINT",FACE,{"disambiguationData":[TD([[makeQuery(id+"F0.imprint","IMPRINT",EDGE,{"derivedFrom":subQ0}),1.0]])]});}
            var Q2;
            {var subQ11=sQuery(id+"F0.wireOp",EDGE,"E4.1.1.8");Q2=makeQuery(id+"F0.imprint","IMPRINT",FACE,{"disambiguationData":[TD([[makeQuery(id+"F0.imprint","IMPRINT",EDGE,{"derivedFrom":subQ11}),1.0]])]});}
            var Q3;
            {var subQ0=sQuery(id+"F0.wireOp",EDGE,"E4.1.1.15");var subQ1=sQuery(id+"F0.wireOp",EDGE,"E4.1.0.0");var subQ2=makeQuery(id+"F0.imprint","INTERSECT",VERTEX,{"derivedFrom":[subQ1,subQ0]});Q3=makeQuery(id+"F0.imprint","IMPRINT",FACE,{"disambiguationData":[TD([[makeQuery(id+"F0.imprint","IMPRINT",EDGE,{"disambiguationData":[TD([[subQ2,-1.0]])],"derivedFrom":subQ1}),-1.0]])]});}
            var Q4;
            {var subQ0=sQuery(id+"F0.wireOp",EDGE,"E4.2.1.15");Q4=makeQuery(id+"F0.imprint","IMPRINT",FACE,{"disambiguationData":[TD([[makeQuery(id+"F0.imprint","IMPRINT",EDGE,{"derivedFrom":subQ0}),1.0]])]});}
            var Q5;
            {var subQ5=sQuery(id+"F0.wireOp",EDGE,"E4.3.1.8");Q5=makeQuery(id+"F0.imprint","IMPRINT",FACE,{"disambiguationData":[TD([[makeQuery(id+"F0.imprint","IMPRINT",EDGE,{"derivedFrom":subQ5}),1.0]])]});}
            var Q6;
            {var subQ0=sQuery(id+"F0.wireOp",EDGE,"E4.4.1.12");var subQ1=sQuery(id+"F0.wireOp",EDGE,"E4.3.0.0");var subQ2=makeQuery(id+"F0.imprint","INTERSECT",VERTEX,{"derivedFrom":[subQ1,subQ0]});Q6=makeQuery(id+"F0.imprint","IMPRINT",FACE,{"disambiguationData":[TD([[makeQuery(id+"F0.imprint","IMPRINT",EDGE,{"disambiguationData":[TD([[subQ2,1.0]])],"derivedFrom":subQ1}),-1.0]])]});}
            var Q7;
            {var subQ8=sQuery(id+"F0.wireOp",EDGE,"E4.3.0.0");var subQ20=sQuery(id+"F0.wireOp",EDGE,"E4.3.0.11");var subQ21=makeQuery(id+"F0.imprint","INTERSECT",VERTEX,{"derivedFrom":[subQ8,subQ20]});Q7=makeQuery(id+"F0.imprint","IMPRINT",FACE,{"disambiguationData":[TD([[makeQuery(id+"F0.imprint","IMPRINT",EDGE,{"disambiguationData":[TD([[subQ21,1.0]])],"derivedFrom":subQ8}),-1.0]])]});}
            var Q8;
            {var subQ0=sQuery(id+"F0.wireOp",EDGE,"E5.right");var subQ1=sQuery(id+"F0.wireOp",EDGE,"E4.4.0.0");var subQ2=makeQuery(id+"F0.imprint","INTERSECT",VERTEX,{"derivedFrom":[subQ1,subQ0]});Q8=makeQuery(id+"F0.imprint","IMPRINT",FACE,{"disambiguationData":[TD([[makeQuery(id+"F0.imprint","IMPRINT",EDGE,{"disambiguationData":[TD([[subQ2,1.0]])],"derivedFrom":subQ1}),-1.0]])]});}
            var Q9;
            {var subQ0=sQuery(id+"F0.wireOp",EDGE,"E4.2.1.7");Q9=makeQuery(id+"F0.imprint","IMPRINT",FACE,{"disambiguationData":[TD([[makeQuery(id+"F0.imprint","IMPRINT",EDGE,{"derivedFrom":subQ0}),-1.0]])]});}
            var Q10;
            {var subQ0=sQuery(id+"F0.wireOp",EDGE,"E4.0.1.14");Q10=makeQuery(id+"F0.imprint","IMPRINT",FACE,{"disambiguationData":[TD([[makeQuery(id+"F0.imprint","IMPRINT",EDGE,{"derivedFrom":subQ0}),-1.0]])]});}
            var Q11;
            Q11=makeQuery(id+"F0.imprint","IMPRINT",FACE,{"disambiguationData":[TD([[makeQuery(id+"F0.imprint","IMPRINT",EDGE,{"derivedFrom":sQuery(id+"F0.wireOp",EDGE,"E4.0.1.2")}),-1.0]])]});
            var Q12;
            {var subQ0=sQuery(id+"F0.wireOp",EDGE,"E4.1.2.3");var subQ1=sQuery(id+"F0.wireOp",EDGE,"E4.0.1.11");var subQ2=makeQuery(id+"F0.imprint","INTERSECT",VERTEX,{"derivedFrom":[subQ1,subQ0]});Q12=makeQuery(id+"F0.imprint","IMPRINT",FACE,{"disambiguationData":[TD([[makeQuery(id+"F0.imprint","IMPRINT",EDGE,{"disambiguationData":[TD([[subQ2,1.0]])],"derivedFrom":subQ1}),1.0]])]});}
            var Q13;
            {var subQ14=sQuery(id+"F0.wireOp",EDGE,"E4.1.1.15");var subQ16=sQuery(id+"F0.wireOp",EDGE,"E4.1.1.2");var subQ18=makeQuery(id+"F0.imprint","INTERSECT",VERTEX,{"derivedFrom":[subQ16,subQ14]});Q13=makeQuery(id+"F0.imprint","IMPRINT",FACE,{"disambiguationData":[TD([[makeQuery(id+"F0.imprint","IMPRINT",EDGE,{"disambiguationData":[TD([[subQ18,-1.0]])],"derivedFrom":subQ16}),-1.0]])]});}
            var Q14;
            {var subQ0=sQuery(id+"F0.wireOp",EDGE,"E4.2.1.14");var subQ1=sQuery(id+"F0.wireOp",EDGE,"E4.1.1.11");var subQ2=makeQuery(id+"F0.imprint","INTERSECT",VERTEX,{"derivedFrom":[subQ1,subQ0]});Q14=makeQuery(id+"F0.imprint","IMPRINT",FACE,{"disambiguationData":[TD([[makeQuery(id+"F0.imprint","IMPRINT",EDGE,{"disambiguationData":[TD([[subQ2,-1.0]])],"derivedFrom":subQ1}),1.0]])]});}
            var Q15;
            Q15=makeQuery(id+"F0.imprint","IMPRINT",FACE,{"disambiguationData":[TD([[makeQuery(id+"F0.imprint","IMPRINT",EDGE,{"derivedFrom":sQuery(id+"F0.wireOp",EDGE,"E4.2.1.2")}),-1.0]])]});
            var Q16;
            {var subQ0=sQuery(id+"F0.wireOp",EDGE,"E39.trimOffspring");var subQ5=sQuery(id+"F0.wireOp",EDGE,"E4.3.1.13");var subQ6=makeQuery(id+"F0.imprint","INTERSECT",VERTEX,{"derivedFrom":[subQ5,subQ0]});Q16=makeQuery(id+"F0.imprint","IMPRINT",FACE,{"disambiguationData":[TD([[makeQuery(id+"F0.imprint","IMPRINT",EDGE,{"disambiguationData":[TD([[subQ6,1.0]])],"derivedFrom":subQ5}),-1.0]])]});}
            var Q17;
            {var subQ5=sQuery(id+"F0.wireOp",EDGE,"E29.trimOffspring");var subQ6=sQuery(id+"F0.wireOp",EDGE,"E4.3.1.2");var subQ7=makeQuery(id+"F0.imprint","INTERSECT",VERTEX,{"derivedFrom":[subQ6,subQ5]});Q17=makeQuery(id+"F0.imprint","IMPRINT",FACE,{"disambiguationData":[TD([[makeQuery(id+"F0.imprint","IMPRINT",EDGE,{"disambiguationData":[TD([[subQ7,-1.0]])],"derivedFrom":subQ6}),-1.0]])]});}
            var Q18;
            {var subQ0=sQuery(id+"F0.wireOp",EDGE,"E4.4.1.14");var subQ1=sQuery(id+"F0.wireOp",EDGE,"E4.3.1.11");var subQ2=makeQuery(id+"F0.imprint","INTERSECT",VERTEX,{"derivedFrom":[subQ1,subQ0]});Q18=makeQuery(id+"F0.imprint","IMPRINT",FACE,{"disambiguationData":[TD([[makeQuery(id+"F0.imprint","IMPRINT",EDGE,{"disambiguationData":[TD([[subQ2,-1.0]])],"derivedFrom":subQ1}),1.0]])]});}
            var Q19;
            {var subQ0=sQuery(id+"F0.wireOp",EDGE,"E4.4.1.2");Q19=makeQuery(id+"F0.imprint","IMPRINT",FACE,{"disambiguationData":[TD([[makeQuery(id+"F0.imprint","IMPRINT",EDGE,{"derivedFrom":subQ0}),-1.0]])]});}
            var Q20;
            {var subQ0=sQuery(id+"F0.wireOp",EDGE,"E5.right");var subQ1=sQuery(id+"F0.wireOp",EDGE,"E4.4.1.0");var subQ2=makeQuery(id+"F0.imprint","INTERSECT",VERTEX,{"derivedFrom":[subQ1,subQ0]});Q20=makeQuery(id+"F0.imprint","IMPRINT",FACE,{"disambiguationData":[TD([[makeQuery(id+"F0.imprint","IMPRINT",EDGE,{"disambiguationData":[TD([[subQ2,1.0]])],"derivedFrom":subQ1}),-1.0]])]});}
            var Q21;
            {var subQ5=sQuery(id+"F0.wireOp",EDGE,"E4.3.1.11");var subQ6=sQuery(id+"F0.wireOp",EDGE,"E4.3.1.0");var subQ7=makeQuery(id+"F0.imprint","INTERSECT",VERTEX,{"derivedFrom":[subQ6,subQ5]});Q21=makeQuery(id+"F0.imprint","IMPRINT",FACE,{"disambiguationData":[TD([[makeQuery(id+"F0.imprint","IMPRINT",EDGE,{"disambiguationData":[TD([[subQ7,1.0]])],"derivedFrom":subQ6}),-1.0]])]});}
            var Q22;
            {var subQ0=sQuery(id+"F0.wireOp",EDGE,"E4.3.2.15");var subQ1=sQuery(id+"F0.wireOp",EDGE,"E4.3.1.0");var subQ2=makeQuery(id+"F0.imprint","INTERSECT",VERTEX,{"derivedFrom":[subQ1,subQ0]});Q22=makeQuery(id+"F0.imprint","IMPRINT",FACE,{"disambiguationData":[TD([[makeQuery(id+"F0.imprint","IMPRINT",EDGE,{"disambiguationData":[TD([[subQ2,-1.0]])],"derivedFrom":subQ1}),-1.0]])]});}
            var Q23;
            Q23=makeQuery(id+"F0.imprint","IMPRINT",FACE,{"disambiguationData":[TD([[makeQuery(id+"F0.imprint","IMPRINT",EDGE,{"derivedFrom":sQuery(id+"F0.wireOp",EDGE,"E4.3.2.7")}),-1.0]])]});
            var Q24;
            {var subQ0=sQuery(id+"F0.wireOp",EDGE,"E4.3.2.12");var subQ1=sQuery(id+"F0.wireOp",EDGE,"E4.2.1.0");var subQ2=makeQuery(id+"F0.imprint","INTERSECT",VERTEX,{"derivedFrom":[subQ1,subQ0]});Q24=makeQuery(id+"F0.imprint","IMPRINT",FACE,{"disambiguationData":[TD([[makeQuery(id+"F0.imprint","IMPRINT",EDGE,{"disambiguationData":[TD([[subQ2,1.0]])],"derivedFrom":subQ1}),-1.0]])]});}
            var Q25;
            {var subQ7=sQuery(id+"F0.wireOp",EDGE,"E4.1.1.11");var subQ8=sQuery(id+"F0.wireOp",EDGE,"E4.1.1.0");var subQ9=makeQuery(id+"F0.imprint","INTERSECT",VERTEX,{"derivedFrom":[subQ8,subQ7]});Q25=makeQuery(id+"F0.imprint","IMPRINT",FACE,{"disambiguationData":[TD([[makeQuery(id+"F0.imprint","IMPRINT",EDGE,{"disambiguationData":[TD([[subQ9,1.0]])],"derivedFrom":subQ8}),-1.0]])]});}
            var Q26;
            {var subQ0=sQuery(id+"F0.wireOp",EDGE,"E4.1.2.15");var subQ1=sQuery(id+"F0.wireOp",EDGE,"E4.1.1.0");var subQ2=makeQuery(id+"F0.imprint","INTERSECT",VERTEX,{"derivedFrom":[subQ1,subQ0]});Q26=makeQuery(id+"F0.imprint","IMPRINT",FACE,{"disambiguationData":[TD([[makeQuery(id+"F0.imprint","IMPRINT",EDGE,{"disambiguationData":[TD([[subQ2,-1.0]])],"derivedFrom":subQ1}),-1.0]])]});}
            var Q27;
            {var subQ1=sQuery(id+"F0.wireOp",EDGE,"E4.1.2.7");Q27=makeQuery(id+"F0.imprint","IMPRINT",FACE,{"disambiguationData":[TD([[makeQuery(id+"F0.imprint","IMPRINT",EDGE,{"derivedFrom":subQ1}),-1.0]])]});}
            var Q28;
            {var subQ0=sQuery(id+"F0.wireOp",EDGE,"E4.1.2.12");var subQ1=sQuery(id+"F0.wireOp",EDGE,"E4.0.1.0");var subQ2=makeQuery(id+"F0.imprint","INTERSECT",VERTEX,{"derivedFrom":[subQ1,subQ0]});Q28=makeQuery(id+"F0.imprint","IMPRINT",FACE,{"disambiguationData":[TD([[makeQuery(id+"F0.imprint","IMPRINT",EDGE,{"disambiguationData":[TD([[subQ2,1.0]])],"derivedFrom":subQ1}),-1.0]])]});}
            var Q29;
            {var subQ9=sQuery(id+"F0.wireOp",EDGE,"E4.0.2.10");Q29=makeQuery(id+"F0.imprint","IMPRINT",FACE,{"disambiguationData":[TD([[makeQuery(id+"F0.imprint","IMPRINT",EDGE,{"derivedFrom":subQ9}),-1.0]])]});}
            var Q30;
            {var subQ0=sQuery(id+"F0.wireOp",EDGE,"E74");Q30=makeQuery(id+"F0.imprint","IMPRINT",FACE,{"disambiguationData":[TD([[makeQuery(id+"F0.imprint","IMPRINT",EDGE,{"derivedFrom":subQ0}),-1.0]])]});}
            var Q31;
            {var subQ12=sQuery(id+"F0.wireOp",EDGE,"E4.0.2.2");var subQ17=sQuery(id+"F0.wireOp",EDGE,"E4.1.2.12");var subQ22=makeQuery(id+"F0.imprint","INTERSECT",VERTEX,{"derivedFrom":[subQ12,subQ17]});Q31=makeQuery(id+"F0.imprint","IMPRINT",FACE,{"disambiguationData":[TD([[makeQuery(id+"F0.imprint","IMPRINT",EDGE,{"disambiguationData":[TD([[subQ22,1.0]])],"derivedFrom":subQ12}),-1.0]])]});}
            var Q32;
            {var subQ0=sQuery(id+"F0.wireOp",EDGE,"E4.1.2.14");var subQ1=sQuery(id+"F0.wireOp",EDGE,"E4.0.2.11");var subQ2=makeQuery(id+"F0.imprint","INTERSECT",VERTEX,{"derivedFrom":[subQ1,subQ0]});Q32=makeQuery(id+"F0.imprint","IMPRINT",FACE,{"disambiguationData":[TD([[makeQuery(id+"F0.imprint","IMPRINT",EDGE,{"disambiguationData":[TD([[subQ2,-1.0]])],"derivedFrom":subQ1}),1.0]])]});}
            var Q33;
            {var subQ9=sQuery(id+"F0.wireOp",EDGE,"E73");Q33=makeQuery(id+"F0.imprint","IMPRINT",FACE,{"disambiguationData":[TD([[makeQuery(id+"F0.imprint","IMPRINT",EDGE,{"derivedFrom":subQ9}),1.0]])]});}
            var Q34;
            {var subQ0=sQuery(id+"F0.wireOp",EDGE,"E4.2.3.3");var subQ1=sQuery(id+"F0.wireOp",EDGE,"E4.1.2.11");var subQ2=makeQuery(id+"F0.imprint","INTERSECT",VERTEX,{"derivedFrom":[subQ1,subQ0]});Q34=makeQuery(id+"F0.imprint","IMPRINT",FACE,{"disambiguationData":[TD([[makeQuery(id+"F0.imprint","IMPRINT",EDGE,{"disambiguationData":[TD([[subQ2,1.0]])],"derivedFrom":subQ1}),1.0]])]});}
            var Q35;
            {var subQ13=sQuery(id+"F0.wireOp",EDGE,"E4.3.2.12");var subQ14=sQuery(id+"F0.wireOp",EDGE,"E4.2.2.2");var subQ15=makeQuery(id+"F0.imprint","INTERSECT",VERTEX,{"derivedFrom":[subQ14,subQ13]});Q35=makeQuery(id+"F0.imprint","IMPRINT",FACE,{"disambiguationData":[TD([[makeQuery(id+"F0.imprint","IMPRINT",EDGE,{"disambiguationData":[TD([[subQ15,1.0]])],"derivedFrom":subQ14}),-1.0]])]});}
            var Q36;
            {var subQ0=sQuery(id+"F0.wireOp",EDGE,"E4.3.2.14");var subQ1=sQuery(id+"F0.wireOp",EDGE,"E4.3.2.13");var subQ2=makeQuery(id+"F0.imprint","INTERSECT",VERTEX,{"derivedFrom":[subQ1,subQ0]});Q36=makeQuery(id+"F0.imprint","IMPRINT",FACE,{"disambiguationData":[TD([[makeQuery(id+"F0.imprint","IMPRINT",EDGE,{"disambiguationData":[TD([[subQ2,-1.0]])],"derivedFrom":subQ1}),-1.0]])]});}
            var Q37;
            {var subQ3=sQuery(id+"F0.wireOp",EDGE,"E69");Q37=makeQuery(id+"F0.imprint","IMPRINT",FACE,{"disambiguationData":[TD([[makeQuery(id+"F0.imprint","IMPRINT",EDGE,{"derivedFrom":subQ3}),1.0]])]});}
            var Q38;
            {var subQ0=sQuery(id+"F0.wireOp",EDGE,"E4.4.3.3");var subQ1=sQuery(id+"F0.wireOp",EDGE,"E4.3.2.11");var subQ2=makeQuery(id+"F0.imprint","INTERSECT",VERTEX,{"derivedFrom":[subQ1,subQ0]});Q38=makeQuery(id+"F0.imprint","IMPRINT",FACE,{"disambiguationData":[TD([[makeQuery(id+"F0.imprint","IMPRINT",EDGE,{"disambiguationData":[TD([[subQ2,1.0]])],"derivedFrom":subQ1}),1.0]])]});}
            var Q39;
            {var subQ3=sQuery(id+"F0.wireOp",EDGE,"E62.trimOffspring");Q39=makeQuery(id+"F0.imprint","IMPRINT",FACE,{"disambiguationData":[TD([[makeQuery(id+"F0.imprint","IMPRINT",EDGE,{"derivedFrom":subQ3}),1.0]])]});}
            var Q40;
            {var subQ5=sQuery(id+"F0.wireOp",EDGE,"E63.trimOffspring");Q40=makeQuery(id+"F0.imprint","IMPRINT",FACE,{"disambiguationData":[TD([[makeQuery(id+"F0.imprint","IMPRINT",EDGE,{"derivedFrom":subQ5}),-1.0]])]});}
            var Q41;
            {var subQ1=sQuery(id+"F0.wireOp",EDGE,"E4.4.3.7");Q41=makeQuery(id+"F0.imprint","IMPRINT",FACE,{"disambiguationData":[TD([[makeQuery(id+"F0.imprint","IMPRINT",EDGE,{"derivedFrom":subQ1}),-1.0]])]});}
            var Q42;
            {var subQ0=sQuery(id+"F0.wireOp",EDGE,"E4.4.3.12");var subQ1=sQuery(id+"F0.wireOp",EDGE,"E4.3.2.0");var subQ2=makeQuery(id+"F0.imprint","INTERSECT",VERTEX,{"derivedFrom":[subQ1,subQ0]});Q42=makeQuery(id+"F0.imprint","IMPRINT",FACE,{"disambiguationData":[TD([[makeQuery(id+"F0.imprint","IMPRINT",EDGE,{"disambiguationData":[TD([[subQ2,1.0]])],"derivedFrom":subQ1}),-1.0]])]});}
            var Q43;
            {var subQ13=sQuery(id+"F0.wireOp",EDGE,"E4.2.3.1");var subQ16=sQuery(id+"F0.wireOp",EDGE,"E4.2.3.11");var subQ17=makeQuery(id+"F0.imprint","INTERSECT",VERTEX,{"derivedFrom":[subQ13,subQ16]});Q43=makeQuery(id+"F0.imprint","IMPRINT",FACE,{"disambiguationData":[TD([[makeQuery(id+"F0.imprint","IMPRINT",EDGE,{"disambiguationData":[TD([[subQ17,1.0]])],"derivedFrom":subQ13}),1.0]])]});}
            var Q44;
            {var subQ0=sQuery(id+"F0.wireOp",EDGE,"E4.2.3.15");var subQ1=sQuery(id+"F0.wireOp",EDGE,"E4.2.3.1");var subQ2=makeQuery(id+"F0.imprint","INTERSECT",VERTEX,{"derivedFrom":[subQ1,subQ0]});Q44=makeQuery(id+"F0.imprint","IMPRINT",FACE,{"disambiguationData":[TD([[makeQuery(id+"F0.imprint","IMPRINT",EDGE,{"disambiguationData":[TD([[subQ2,-1.0]])],"derivedFrom":subQ1}),1.0]])]});}
            var Q45;
            {var subQ4=sQuery(id+"F0.wireOp",EDGE,"E4.2.3.7");Q45=makeQuery(id+"F0.imprint","IMPRINT",FACE,{"disambiguationData":[TD([[makeQuery(id+"F0.imprint","IMPRINT",EDGE,{"derivedFrom":subQ4}),-1.0]])]});}
            var Q46;
            {var subQ5=sQuery(id+"F0.wireOp",EDGE,"E72");Q46=makeQuery(id+"F0.imprint","IMPRINT",FACE,{"disambiguationData":[TD([[makeQuery(id+"F0.imprint","IMPRINT",EDGE,{"derivedFrom":subQ5}),-1.0]])]});}
            var Q47;
            {var subQ16=sQuery(id+"F0.wireOp",EDGE,"E4.0.2.0");var subQ18=sQuery(id+"F0.wireOp",EDGE,"E4.0.2.11");var subQ19=makeQuery(id+"F0.imprint","INTERSECT",VERTEX,{"derivedFrom":[subQ16,subQ18]});Q47=makeQuery(id+"F0.imprint","IMPRINT",FACE,{"disambiguationData":[TD([[makeQuery(id+"F0.imprint","IMPRINT",EDGE,{"disambiguationData":[TD([[subQ19,1.0]])],"derivedFrom":subQ16}),-1.0]])]});}
            var Q48;
            {var subQ0=sQuery(id+"F0.wireOp",EDGE,"E4.0.3.15");var subQ1=sQuery(id+"F0.wireOp",EDGE,"E4.0.2.0");var subQ2=makeQuery(id+"F0.imprint","INTERSECT",VERTEX,{"derivedFrom":[subQ1,subQ0]});Q48=makeQuery(id+"F0.imprint","IMPRINT",FACE,{"disambiguationData":[TD([[makeQuery(id+"F0.imprint","IMPRINT",EDGE,{"disambiguationData":[TD([[subQ2,-1.0]])],"derivedFrom":subQ1}),-1.0]])]});}
            var Q49;
            {var subQ2=sQuery(id+"F0.wireOp",EDGE,"E4.0.3.7");Q49=makeQuery(id+"F0.imprint","IMPRINT",FACE,{"disambiguationData":[TD([[makeQuery(id+"F0.imprint","IMPRINT",EDGE,{"derivedFrom":subQ2}),-1.0]])]});}
            var Q50;
            {var subQ1=sQuery(id+"F0.wireOp",EDGE,"E4.0.3.4");Q50=makeQuery(id+"F0.imprint","IMPRINT",FACE,{"disambiguationData":[TD([[makeQuery(id+"F0.imprint","IMPRINT",EDGE,{"derivedFrom":subQ1}),-1.0]])]});}
            var Q51;
            {var subQ0=sQuery(id+"F0.wireOp",EDGE,"E5.top");var subQ1=sQuery(id+"F0.wireOp",EDGE,"E4.0.3.11");var subQ2=makeQuery(id+"F0.imprint","INTERSECT",VERTEX,{"derivedFrom":[subQ1,subQ0]});Q51=makeQuery(id+"F0.imprint","IMPRINT",FACE,{"disambiguationData":[TD([[makeQuery(id+"F0.imprint","IMPRINT",EDGE,{"disambiguationData":[TD([[subQ2,1.0]])],"derivedFrom":subQ1}),1.0]])]});}
            var Q52;
            {var subQ5=sQuery(id+"F0.wireOp",EDGE,"E4.1.3.4");Q52=makeQuery(id+"F0.imprint","IMPRINT",FACE,{"disambiguationData":[TD([[makeQuery(id+"F0.imprint","IMPRINT",EDGE,{"derivedFrom":subQ5}),-1.0]])]});}
            var Q53;
            {var subQ3=sQuery(id+"F0.wireOp",EDGE,"E4.0.3.14");Q53=makeQuery(id+"F0.imprint","IMPRINT",FACE,{"disambiguationData":[TD([[makeQuery(id+"F0.imprint","IMPRINT",EDGE,{"derivedFrom":subQ3}),-1.0]])]});}
            var Q54;
            {var subQ0=sQuery(id+"F0.wireOp",EDGE,"E4.1.3.11");Q54=makeQuery(id+"F0.imprint","IMPRINT",FACE,{"disambiguationData":[TD([[makeQuery(id+"F0.imprint","IMPRINT",EDGE,{"derivedFrom":subQ0}),1.0]])]});}
            var Q55;
            {var subQ1=sQuery(id+"F0.wireOp",EDGE,"E4.2.3.4");Q55=makeQuery(id+"F0.imprint","IMPRINT",FACE,{"disambiguationData":[TD([[makeQuery(id+"F0.imprint","IMPRINT",EDGE,{"derivedFrom":subQ1}),-1.0]])]});}
            var Q56;
            {var subQ0=sQuery(id+"F0.wireOp",EDGE,"E5.top");var subQ1=sQuery(id+"F0.wireOp",EDGE,"E4.2.3.11");var subQ2=makeQuery(id+"F0.imprint","INTERSECT",VERTEX,{"derivedFrom":[subQ1,subQ0]});Q56=makeQuery(id+"F0.imprint","IMPRINT",FACE,{"disambiguationData":[TD([[makeQuery(id+"F0.imprint","IMPRINT",EDGE,{"disambiguationData":[TD([[subQ2,1.0]])],"derivedFrom":subQ1}),1.0]])]});}
            var Q57;
            {var subQ11=sQuery(id+"F0.wireOp",EDGE,"E4.3.3.4");Q57=makeQuery(id+"F0.imprint","IMPRINT",FACE,{"disambiguationData":[TD([[makeQuery(id+"F0.imprint","IMPRINT",EDGE,{"derivedFrom":subQ11}),-1.0]])]});}
            var Q58;
            {var subQ0=sQuery(id+"F0.wireOp",EDGE,"E4.3.3.11");Q58=makeQuery(id+"F0.imprint","IMPRINT",FACE,{"disambiguationData":[TD([[makeQuery(id+"F0.imprint","IMPRINT",EDGE,{"derivedFrom":subQ0}),1.0]])]});}
            var Q59;
            {var subQ7=sQuery(id+"F0.wireOp",EDGE,"E65.trimOffspring");Q59=makeQuery(id+"F0.imprint","IMPRINT",FACE,{"disambiguationData":[TD([[makeQuery(id+"F0.imprint","IMPRINT",EDGE,{"derivedFrom":subQ7}),1.0]])]});}
            var Q60;
            {var subQ3=sQuery(id+"F0.wireOp",EDGE,"E64.trimOffspring");Q60=makeQuery(id+"F0.imprint","IMPRINT",FACE,{"disambiguationData":[TD([[makeQuery(id+"F0.imprint","IMPRINT",EDGE,{"derivedFrom":subQ3}),-1.0]])]});}
            var Q61;
            {var subQ0=sQuery(id+"F0.wireOp",EDGE,"E4.3.3.5");var subQ1=sQuery(id+"F0.wireOp",EDGE,"E4.3.3.2");var subQ2=makeQuery(id+"F0.imprint","INTERSECT",VERTEX,{"derivedFrom":[subQ1,subQ0]});Q61=makeQuery(id+"F0.imprint","IMPRINT",FACE,{"disambiguationData":[TD([[makeQuery(id+"F0.imprint","IMPRINT",EDGE,{"disambiguationData":[TD([[subQ2,-1.0]])],"derivedFrom":subQ1}),-1.0]])]});}
            var Q62;
            {var subQ0=sQuery(id+"F0.wireOp",EDGE,"E4.3.2.6");var subQ1=sQuery(id+"F0.wireOp",EDGE,"E4.3.2.5");var subQ2=makeQuery(id+"F0.imprint","INTERSECT",VERTEX,{"derivedFrom":[subQ1,subQ0]});Q62=makeQuery(id+"F0.imprint","IMPRINT",FACE,{"disambiguationData":[TD([[makeQuery(id+"F0.imprint","IMPRINT",EDGE,{"disambiguationData":[TD([[subQ2,1.0]])],"derivedFrom":subQ1}),1.0]])]});}
            var Q63;
            {var subQ0=sQuery(id+"F0.wireOp",EDGE,"E4.4.2.5");var subQ1=sQuery(id+"F0.wireOp",EDGE,"E4.4.2.2");var subQ2=makeQuery(id+"F0.imprint","INTERSECT",VERTEX,{"derivedFrom":[subQ1,subQ0]});Q63=makeQuery(id+"F0.imprint","IMPRINT",FACE,{"disambiguationData":[TD([[makeQuery(id+"F0.imprint","IMPRINT",EDGE,{"disambiguationData":[TD([[subQ2,-1.0]])],"derivedFrom":subQ1}),-1.0]])]});}
            var Q64;
            {var subQ0=sQuery(id+"F0.wireOp",EDGE,"E47.trimOffspring");var subQ1=sQuery(id+"F0.wireOp",EDGE,"E4.3.2.4");var subQ2=makeQuery(id+"F0.imprint","INTERSECT",VERTEX,{"derivedFrom":[subQ1,subQ0]});Q64=makeQuery(id+"F0.imprint","IMPRINT",FACE,{"disambiguationData":[TD([[makeQuery(id+"F0.imprint","IMPRINT",EDGE,{"disambiguationData":[TD([[subQ2,-1.0]])],"derivedFrom":subQ1}),-1.0]])]});}
            var Q65;
            {var subQ0=sQuery(id+"F0.wireOp",EDGE,"E4.3.1.6");var subQ1=sQuery(id+"F0.wireOp",EDGE,"E4.3.1.4");var subQ2=makeQuery(id+"F0.imprint","INTERSECT",VERTEX,{"derivedFrom":[subQ1,subQ0]});Q65=makeQuery(id+"F0.imprint","IMPRINT",FACE,{"disambiguationData":[TD([[makeQuery(id+"F0.imprint","IMPRINT",EDGE,{"disambiguationData":[TD([[subQ2,1.0]])],"derivedFrom":subQ1}),-1.0]])]});}
            var Q66;
            {var subQ0=sQuery(id+"F0.wireOp",EDGE,"E4.3.1.4");var subQ1=sQuery(id+"F0.wireOp",EDGE,"E4.3.1.2");var subQ2=makeQuery(id+"F0.imprint","INTERSECT",VERTEX,{"derivedFrom":[subQ1,subQ0]});Q66=makeQuery(id+"F0.imprint","IMPRINT",FACE,{"disambiguationData":[TD([[makeQuery(id+"F0.imprint","IMPRINT",EDGE,{"disambiguationData":[TD([[subQ2,1.0]])],"derivedFrom":subQ1}),-1.0]])]});}
            var Q67;
            {var subQ0=sQuery(id+"F0.wireOp",EDGE,"E4.3.1.5");var subQ1=sQuery(id+"F0.wireOp",EDGE,"E4.3.1.2");var subQ2=makeQuery(id+"F0.imprint","INTERSECT",VERTEX,{"derivedFrom":[subQ1,subQ0]});Q67=makeQuery(id+"F0.imprint","IMPRINT",FACE,{"disambiguationData":[TD([[makeQuery(id+"F0.imprint","IMPRINT",EDGE,{"disambiguationData":[TD([[subQ2,-1.0]])],"derivedFrom":subQ1}),-1.0]])]});}
            var Q68;
            {var subQ0=sQuery(id+"F0.wireOp",EDGE,"E4.3.2.10");Q68=makeQuery(id+"F0.imprint","IMPRINT",FACE,{"disambiguationData":[TD([[makeQuery(id+"F0.imprint","IMPRINT",EDGE,{"derivedFrom":subQ0}),-1.0]])]});}
            var Q69;
            {var subQ0=sQuery(id+"F0.wireOp",EDGE,"E4.2.2.5");var subQ1=sQuery(id+"F0.wireOp",EDGE,"E4.2.2.2");var subQ2=makeQuery(id+"F0.imprint","INTERSECT",VERTEX,{"derivedFrom":[subQ1,subQ0]});Q69=makeQuery(id+"F0.imprint","IMPRINT",FACE,{"disambiguationData":[TD([[makeQuery(id+"F0.imprint","IMPRINT",EDGE,{"disambiguationData":[TD([[subQ2,-1.0]])],"derivedFrom":subQ1}),-1.0]])]});}
            var Q70;
            {var subQ0=sQuery(id+"F0.wireOp",EDGE,"E4.3.3.10");var subQ1=sQuery(id+"F0.wireOp",EDGE,"E4.3.3.8");var subQ2=makeQuery(id+"F0.imprint","INTERSECT",VERTEX,{"derivedFrom":[subQ1,subQ0]});Q70=makeQuery(id+"F0.imprint","IMPRINT",FACE,{"disambiguationData":[TD([[makeQuery(id+"F0.imprint","IMPRINT",EDGE,{"disambiguationData":[TD([[subQ2,-1.0]])],"derivedFrom":subQ1}),1.0]])]});}
            var Q71;
            {var subQ3=sQuery(id+"F0.wireOp",EDGE,"E56.trimOffspring");Q71=makeQuery(id+"F0.imprint","IMPRINT",FACE,{"disambiguationData":[TD([[makeQuery(id+"F0.imprint","IMPRINT",EDGE,{"derivedFrom":subQ3}),-1.0]])]});}
            var Q72;
            {var subQ0=sQuery(id+"F0.wireOp",EDGE,"E4.1.3.5");var subQ1=sQuery(id+"F0.wireOp",EDGE,"E4.1.3.2");var subQ2=makeQuery(id+"F0.imprint","INTERSECT",VERTEX,{"derivedFrom":[subQ1,subQ0]});Q72=makeQuery(id+"F0.imprint","IMPRINT",FACE,{"disambiguationData":[TD([[makeQuery(id+"F0.imprint","IMPRINT",EDGE,{"disambiguationData":[TD([[subQ2,-1.0]])],"derivedFrom":subQ1}),-1.0]])]});}
            var Q73;
            {var subQ0=sQuery(id+"F0.wireOp",EDGE,"E35.trimOffspring");var subQ1=sQuery(id+"F0.wireOp",EDGE,"E4.1.2.6");var subQ2=makeQuery(id+"F0.imprint","INTERSECT",VERTEX,{"derivedFrom":[subQ1,subQ0]});Q73=makeQuery(id+"F0.imprint","IMPRINT",FACE,{"disambiguationData":[TD([[makeQuery(id+"F0.imprint","IMPRINT",EDGE,{"disambiguationData":[TD([[subQ2,-1.0]])],"derivedFrom":subQ1}),1.0]])]});}
            var Q74;
            {var subQ0=sQuery(id+"F0.wireOp",EDGE,"E4.0.2.6");var subQ1=sQuery(id+"F0.wireOp",EDGE,"E4.0.2.4");var subQ2=makeQuery(id+"F0.imprint","INTERSECT",VERTEX,{"derivedFrom":[subQ1,subQ0]});Q74=makeQuery(id+"F0.imprint","IMPRINT",FACE,{"disambiguationData":[TD([[makeQuery(id+"F0.imprint","IMPRINT",EDGE,{"disambiguationData":[TD([[subQ2,1.0]])],"derivedFrom":subQ1}),-1.0]])]});}
            var Q75;
            {var subQ0=sQuery(id+"F0.wireOp",EDGE,"E4.1.2.4");var subQ1=sQuery(id+"F0.wireOp",EDGE,"E4.1.2.2");var subQ2=makeQuery(id+"F0.imprint","INTERSECT",VERTEX,{"derivedFrom":[subQ1,subQ0]});Q75=makeQuery(id+"F0.imprint","IMPRINT",FACE,{"disambiguationData":[TD([[makeQuery(id+"F0.imprint","IMPRINT",EDGE,{"disambiguationData":[TD([[subQ2,1.0]])],"derivedFrom":subQ1}),-1.0]])]});}
            var Q76;
            {var subQ0=sQuery(id+"F0.wireOp",EDGE,"E4.1.1.6");var subQ1=sQuery(id+"F0.wireOp",EDGE,"E4.1.1.4");var subQ2=makeQuery(id+"F0.imprint","INTERSECT",VERTEX,{"derivedFrom":[subQ1,subQ0]});Q76=makeQuery(id+"F0.imprint","IMPRINT",FACE,{"disambiguationData":[TD([[makeQuery(id+"F0.imprint","IMPRINT",EDGE,{"disambiguationData":[TD([[subQ2,1.0]])],"derivedFrom":subQ1}),-1.0]])]});}
            var Q77;
            {var subQ3=sQuery(id+"F0.wireOp",EDGE,"E31.trimOffspring");Q77=makeQuery(id+"F0.imprint","IMPRINT",FACE,{"disambiguationData":[TD([[makeQuery(id+"F0.imprint","IMPRINT",EDGE,{"derivedFrom":subQ3}),1.0]])]});}
            var Q78;
            {var subQ3=sQuery(id+"F0.wireOp",EDGE,"E50.trimOffspring");Q78=makeQuery(id+"F0.imprint","IMPRINT",FACE,{"disambiguationData":[TD([[makeQuery(id+"F0.imprint","IMPRINT",EDGE,{"derivedFrom":subQ3}),-1.0]])]});}
            var Q79;
            {var subQ0=sQuery(id+"F0.wireOp",EDGE,"E4.0.2.5");var subQ1=sQuery(id+"F0.wireOp",EDGE,"E4.0.2.2");var subQ2=makeQuery(id+"F0.imprint","INTERSECT",VERTEX,{"derivedFrom":[subQ1,subQ0]});Q79=makeQuery(id+"F0.imprint","IMPRINT",FACE,{"disambiguationData":[TD([[makeQuery(id+"F0.imprint","IMPRINT",EDGE,{"disambiguationData":[TD([[subQ2,-1.0]])],"derivedFrom":subQ1}),-1.0]])]});}
            var Q80;
            {var subQ0=sQuery(id+"F0.wireOp",EDGE,"E4.1.1.5");var subQ1=sQuery(id+"F0.wireOp",EDGE,"E4.1.1.2");var subQ2=makeQuery(id+"F0.imprint","INTERSECT",VERTEX,{"derivedFrom":[subQ1,subQ0]});Q80=makeQuery(id+"F0.imprint","IMPRINT",FACE,{"disambiguationData":[TD([[makeQuery(id+"F0.imprint","IMPRINT",EDGE,{"disambiguationData":[TD([[subQ2,-1.0]])],"derivedFrom":subQ1}),-1.0]])]});}
            var Q81;
            {var subQ0=sQuery(id+"F0.wireOp",EDGE,"E4.1.1.4");var subQ1=sQuery(id+"F0.wireOp",EDGE,"E4.1.1.2");var subQ2=makeQuery(id+"F0.imprint","INTERSECT",VERTEX,{"derivedFrom":[subQ1,subQ0]});Q81=makeQuery(id+"F0.imprint","IMPRINT",FACE,{"disambiguationData":[TD([[makeQuery(id+"F0.imprint","IMPRINT",EDGE,{"disambiguationData":[TD([[subQ2,1.0]])],"derivedFrom":subQ1}),-1.0]])]});}
            extrude(context, id + "F2", {"entities" : qUnion([Q0, Q1, Q2, Q3, Q4, Q5, Q6, Q7, Q8, Q9, Q10, Q11, Q12, Q13, Q14, Q15, Q16, Q17, Q18, Q19, Q20, Q21, Q22, Q23, Q24, Q25, Q26, Q27, Q28, Q29, Q30, Q31, Q32, Q33, Q34, Q35, Q36, Q37, Q38, Q39, Q40, Q41, Q42, Q43, Q44, Q45, Q46, Q47, Q48, Q49, Q50, Q51, Q52, Q53, Q54, Q55, Q56, Q57, Q58, Q59, Q60, Q61, Q62, Q63, Q64, Q65, Q66, Q67, Q68, Q69, Q70, Q71, Q72, Q73, Q74, Q75, Q76, Q77, Q78, Q79, Q80, Q81]), "oppositeDirection" : true, "depth" : 3.17 * mm, "offsetDistance" : 25.4 * mm});
        }
        {
            var Q0;
            Q0=makeQuery(id+"F1.opExtrude","CAP_FACE",FACE,{"disambiguationData":[OSD([sQuery(id+"F0.wireOp",EDGE,"E3.2"),sQuery(id+"F0.wireOp",EDGE,"E4.0.1.0"),sQuery(id+"F0.wireOp",EDGE,"E4.0.1.1"),sQuery(id+"F0.wireOp",EDGE,"E4.0.1.2"),sQuery(id+"F0.wireOp",EDGE,"E4.0.1.4"),sQuery(id+"F0.wireOp",EDGE,"E4.0.1.5"),sQuery(id+"F0.wireOp",EDGE,"E4.0.1.6"),sQuery(id+"F0.wireOp",EDGE,"E4.0.1.7"),sQuery(id+"F0.wireOp",EDGE,"E4.0.1.9"),sQuery(id+"F0.wireOp",EDGE,"E4.0.1.11"),sQuery(id+"F0.wireOp",EDGE,"E4.0.1.13"),sQuery(id+"F0.wireOp",EDGE,"E4.0.1.14"),sQuery(id+"F0.wireOp",EDGE,"E4.0.1.15"),sQuery(id+"F0.wireOp",EDGE,"E4.0.2.0"),sQuery(id+"F0.wireOp",EDGE,"E4.0.2.1"),sQuery(id+"F0.wireOp",EDGE,"E4.0.2.2"),sQuery(id+"F0.wireOp",EDGE,"E4.0.2.4"),sQuery(id+"F0.wireOp",EDGE,"E4.0.2.5"),sQuery(id+"F0.wireOp",EDGE,"E4.0.2.6"),sQuery(id+"F0.wireOp",EDGE,"E4.0.2.7"),sQuery(id+"F0.wireOp",EDGE,"E4.0.2.9"),sQuery(id+"F0.wireOp",EDGE,"E4.0.2.10"),sQuery(id+"F0.wireOp",EDGE,"E4.0.2.11"),sQuery(id+"F0.wireOp",EDGE,"E4.0.2.13"),sQuery(id+"F0.wireOp",EDGE,"E4.0.2.14"),sQuery(id+"F0.wireOp",EDGE,"E4.0.2.15"),sQuery(id+"F0.wireOp",EDGE,"E4.0.3.1"),sQuery(id+"F0.wireOp",EDGE,"E4.0.3.2"),sQuery(id+"F0.wireOp",EDGE,"E4.0.3.3"),sQuery(id+"F0.wireOp",EDGE,"E4.0.3.4"),sQuery(id+"F0.wireOp",EDGE,"E4.0.3.5"),sQuery(id+"F0.wireOp",EDGE,"E4.0.3.7"),sQuery(id+"F0.wireOp",EDGE,"E4.0.3.9"),sQuery(id+"F0.wireOp",EDGE,"E4.0.3.10"),sQuery(id+"F0.wireOp",EDGE,"E4.0.3.11"),sQuery(id+"F0.wireOp",EDGE,"E4.0.3.13"),sQuery(id+"F0.wireOp",EDGE,"E4.0.3.14"),sQuery(id+"F0.wireOp",EDGE,"E4.0.3.15"),sQuery(id+"F0.wireOp",EDGE,"E4.1.0.0"),sQuery(id+"F0.wireOp",EDGE,"E4.1.1.0"),sQuery(id+"F0.wireOp",EDGE,"E4.1.1.1"),sQuery(id+"F0.wireOp",EDGE,"E4.1.1.2"),sQuery(id+"F0.wireOp",EDGE,"E4.1.1.4"),sQuery(id+"F0.wireOp",EDGE,"E4.1.1.5"),sQuery(id+"F0.wireOp",EDGE,"E4.1.1.6"),sQuery(id+"F0.wireOp",EDGE,"E4.1.1.7"),sQuery(id+"F0.wireOp",EDGE,"E4.1.1.8"),sQuery(id+"F0.wireOp",EDGE,"E4.1.1.9"),sQuery(id+"F0.wireOp",EDGE,"E4.1.1.11"),sQuery(id+"F0.wireOp",EDGE,"E4.1.1.12"),sQuery(id+"F0.wireOp",EDGE,"E4.1.1.13"),sQuery(id+"F0.wireOp",EDGE,"E4.1.1.14"),sQuery(id+"F0.wireOp",EDGE,"E4.1.1.15"),sQuery(id+"F0.wireOp",EDGE,"E4.1.2.0"),sQuery(id+"F0.wireOp",EDGE,"E4.1.2.1"),sQuery(id+"F0.wireOp",EDGE,"E4.1.2.2"),sQuery(id+"F0.wireOp",EDGE,"E4.1.2.3"),sQuery(id+"F0.wireOp",EDGE,"E4.1.2.4"),sQuery(id+"F0.wireOp",EDGE,"E4.1.2.6"),sQuery(id+"F0.wireOp",EDGE,"E4.1.2.7"),sQuery(id+"F0.wireOp",EDGE,"E4.1.2.8"),sQuery(id+"F0.wireOp",EDGE,"E4.1.2.9"),sQuery(id+"F0.wireOp",EDGE,"E4.1.2.10"),sQuery(id+"F0.wireOp",EDGE,"E4.1.2.11"),sQuery(id+"F0.wireOp",EDGE,"E4.1.2.12"),sQuery(id+"F0.wireOp",EDGE,"E4.1.2.13"),sQuery(id+"F0.wireOp",EDGE,"E4.1.2.14"),sQuery(id+"F0.wireOp",EDGE,"E4.1.2.15"),sQuery(id+"F0.wireOp",EDGE,"E4.1.3.1"),sQuery(id+"F0.wireOp",EDGE,"E4.1.3.2"),sQuery(id+"F0.wireOp",EDGE,"E4.1.3.3"),sQuery(id+"F0.wireOp",EDGE,"E4.1.3.4"),sQuery(id+"F0.wireOp",EDGE,"E4.1.3.5"),sQuery(id+"F0.wireOp",EDGE,"E4.1.3.7"),sQuery(id+"F0.wireOp",EDGE,"E4.1.3.8"),sQuery(id+"F0.wireOp",EDGE,"E4.1.3.9"),sQuery(id+"F0.wireOp",EDGE,"E4.1.3.10"),sQuery(id+"F0.wireOp",EDGE,"E4.1.3.11"),sQuery(id+"F0.wireOp",EDGE,"E4.1.3.12"),sQuery(id+"F0.wireOp",EDGE,"E4.1.3.13"),sQuery(id+"F0.wireOp",EDGE,"E4.1.3.14"),sQuery(id+"F0.wireOp",EDGE,"E4.1.3.15"),sQuery(id+"F0.wireOp",EDGE,"E4.2.0.0"),sQuery(id+"F0.wireOp",EDGE,"E4.2.1.0"),sQuery(id+"F0.wireOp",EDGE,"E4.2.1.1"),sQuery(id+"F0.wireOp",EDGE,"E4.2.1.2"),sQuery(id+"F0.wireOp",EDGE,"E4.2.1.4"),sQuery(id+"F0.wireOp",EDGE,"E4.2.1.5"),sQuery(id+"F0.wireOp",EDGE,"E4.2.1.6"),sQuery(id+"F0.wireOp",EDGE,"E4.2.1.7"),sQuery(id+"F0.wireOp",EDGE,"E4.2.1.8"),sQuery(id+"F0.wireOp",EDGE,"E4.2.1.9"),sQuery(id+"F0.wireOp",EDGE,"E4.2.1.11"),sQuery(id+"F0.wireOp",EDGE,"E4.2.1.12"),sQuery(id+"F0.wireOp",EDGE,"E4.2.1.13"),sQuery(id+"F0.wireOp",EDGE,"E4.2.1.14"),sQuery(id+"F0.wireOp",EDGE,"E4.2.1.15"),sQuery(id+"F0.wireOp",EDGE,"E4.2.2.1"),sQuery(id+"F0.wireOp",EDGE,"E4.2.2.2"),sQuery(id+"F0.wireOp",EDGE,"E4.2.2.3"),sQuery(id+"F0.wireOp",EDGE,"E4.2.2.5"),sQuery(id+"F0.wireOp",EDGE,"E4.2.2.7"),sQuery(id+"F0.wireOp",EDGE,"E4.2.2.8"),sQuery(id+"F0.wireOp",EDGE,"E4.2.2.9"),sQuery(id+"F0.wireOp",EDGE,"E4.2.2.10"),sQuery(id+"F0.wireOp",EDGE,"E4.2.2.12"),sQuery(id+"F0.wireOp",EDGE,"E4.2.2.13"),sQuery(id+"F0.wireOp",EDGE,"E4.2.2.14"),sQuery(id+"F0.wireOp",EDGE,"E4.2.2.15"),sQuery(id+"F0.wireOp",EDGE,"E4.2.3.1"),sQuery(id+"F0.wireOp",EDGE,"E4.2.3.2"),sQuery(id+"F0.wireOp",EDGE,"E4.2.3.3"),sQuery(id+"F0.wireOp",EDGE,"E4.2.3.4"),sQuery(id+"F0.wireOp",EDGE,"E4.2.3.5"),sQuery(id+"F0.wireOp",EDGE,"E4.2.3.7"),sQuery(id+"F0.wireOp",EDGE,"E4.2.3.8"),sQuery(id+"F0.wireOp",EDGE,"E4.2.3.9"),sQuery(id+"F0.wireOp",EDGE,"E4.2.3.10"),sQuery(id+"F0.wireOp",EDGE,"E4.2.3.11"),sQuery(id+"F0.wireOp",EDGE,"E4.2.3.12"),sQuery(id+"F0.wireOp",EDGE,"E4.2.3.13"),sQuery(id+"F0.wireOp",EDGE,"E4.2.3.14"),sQuery(id+"F0.wireOp",EDGE,"E4.2.3.15"),sQuery(id+"F0.wireOp",EDGE,"E4.3.0.0"),sQuery(id+"F0.wireOp",EDGE,"E4.3.1.0"),sQuery(id+"F0.wireOp",EDGE,"E4.3.1.1"),sQuery(id+"F0.wireOp",EDGE,"E4.3.1.2"),sQuery(id+"F0.wireOp",EDGE,"E4.3.1.4"),sQuery(id+"F0.wireOp",EDGE,"E4.3.1.5"),sQuery(id+"F0.wireOp",EDGE,"E4.3.1.6"),sQuery(id+"F0.wireOp",EDGE,"E4.3.1.8"),sQuery(id+"F0.wireOp",EDGE,"E4.3.1.11"),sQuery(id+"F0.wireOp",EDGE,"E4.3.1.12"),sQuery(id+"F0.wireOp",EDGE,"E4.3.1.13"),sQuery(id+"F0.wireOp",EDGE,"E4.3.2.0"),sQuery(id+"F0.wireOp",EDGE,"E4.3.2.3"),sQuery(id+"F0.wireOp",EDGE,"E4.3.2.4"),sQuery(id+"F0.wireOp",EDGE,"E4.3.2.5"),sQuery(id+"F0.wireOp",EDGE,"E4.3.2.6"),sQuery(id+"F0.wireOp",EDGE,"E4.3.2.7"),sQuery(id+"F0.wireOp",EDGE,"E4.3.2.8"),sQuery(id+"F0.wireOp",EDGE,"E4.3.2.9"),sQuery(id+"F0.wireOp",EDGE,"E4.3.2.10"),sQuery(id+"F0.wireOp",EDGE,"E4.3.2.11"),sQuery(id+"F0.wireOp",EDGE,"E4.3.2.12"),sQuery(id+"F0.wireOp",EDGE,"E4.3.2.13"),sQuery(id+"F0.wireOp",EDGE,"E4.3.2.14"),sQuery(id+"F0.wireOp",EDGE,"E4.3.2.15"),sQuery(id+"F0.wireOp",EDGE,"E4.3.3.1"),sQuery(id+"F0.wireOp",EDGE,"E4.3.3.2"),sQuery(id+"F0.wireOp",EDGE,"E4.3.3.3"),sQuery(id+"F0.wireOp",EDGE,"E4.3.3.4"),sQuery(id+"F0.wireOp",EDGE,"E4.3.3.5"),sQuery(id+"F0.wireOp",EDGE,"E4.3.3.7"),sQuery(id+"F0.wireOp",EDGE,"E4.3.3.8"),sQuery(id+"F0.wireOp",EDGE,"E4.3.3.10"),sQuery(id+"F0.wireOp",EDGE,"E4.3.3.11"),sQuery(id+"F0.wireOp",EDGE,"E4.3.3.12"),sQuery(id+"F0.wireOp",EDGE,"E4.3.3.13"),sQuery(id+"F0.wireOp",EDGE,"E4.3.3.15"),sQuery(id+"F0.wireOp",EDGE,"E4.4.0.0"),sQuery(id+"F0.wireOp",EDGE,"E4.4.1.0"),sQuery(id+"F0.wireOp",EDGE,"E4.4.1.1"),sQuery(id+"F0.wireOp",EDGE,"E4.4.1.2"),sQuery(id+"F0.wireOp",EDGE,"E4.4.1.5"),sQuery(id+"F0.wireOp",EDGE,"E4.4.1.6"),sQuery(id+"F0.wireOp",EDGE,"E4.4.1.7"),sQuery(id+"F0.wireOp",EDGE,"E4.4.1.8"),sQuery(id+"F0.wireOp",EDGE,"E4.4.1.9"),sQuery(id+"F0.wireOp",EDGE,"E4.4.1.12"),sQuery(id+"F0.wireOp",EDGE,"E4.4.1.13"),sQuery(id+"F0.wireOp",EDGE,"E4.4.1.14"),sQuery(id+"F0.wireOp",EDGE,"E4.4.1.15"),sQuery(id+"F0.wireOp",EDGE,"E4.4.2.1"),sQuery(id+"F0.wireOp",EDGE,"E4.4.2.2"),sQuery(id+"F0.wireOp",EDGE,"E4.4.2.3"),sQuery(id+"F0.wireOp",EDGE,"E4.4.2.5"),sQuery(id+"F0.wireOp",EDGE,"E4.4.2.7"),sQuery(id+"F0.wireOp",EDGE,"E4.4.2.8"),sQuery(id+"F0.wireOp",EDGE,"E4.4.2.9"),sQuery(id+"F0.wireOp",EDGE,"E4.4.2.10"),sQuery(id+"F0.wireOp",EDGE,"E4.4.2.12"),sQuery(id+"F0.wireOp",EDGE,"E4.4.2.13"),sQuery(id+"F0.wireOp",EDGE,"E4.4.2.14"),sQuery(id+"F0.wireOp",EDGE,"E4.4.3.1"),sQuery(id+"F0.wireOp",EDGE,"E4.4.3.2"),sQuery(id+"F0.wireOp",EDGE,"E4.4.3.3"),sQuery(id+"F0.wireOp",EDGE,"E4.4.3.5"),sQuery(id+"F0.wireOp",EDGE,"E4.4.3.7"),sQuery(id+"F0.wireOp",EDGE,"E4.4.3.8"),sQuery(id+"F0.wireOp",EDGE,"E4.4.3.9"),sQuery(id+"F0.wireOp",EDGE,"E4.4.3.10"),sQuery(id+"F0.wireOp",EDGE,"E4.4.3.12"),sQuery(id+"F0.wireOp",EDGE,"E4.4.3.13"),sQuery(id+"F0.wireOp",EDGE,"E4.4.3.14"),sQuery(id+"F0.wireOp",EDGE,"E4.4.3.15"),sQuery(id+"F0.wireOp",EDGE,"E5.top"),sQuery(id+"F0.wireOp",EDGE,"E5.left"),sQuery(id+"F0.wireOp",EDGE,"E5.right"),sQuery(id+"F0.wireOp",EDGE,"E29.trimOffspring"),sQuery(id+"F0.wireOp",EDGE,"E30.trimOffspring"),sQuery(id+"F0.wireOp",EDGE,"E31.trimOffspring"),sQuery(id+"F0.wireOp",EDGE,"E32.trimOffspring"),sQuery(id+"F0.wireOp",EDGE,"E33.trimOffspring"),sQuery(id+"F0.wireOp",EDGE,"E34.trimOffspring"),sQuery(id+"F0.wireOp",EDGE,"E35.trimOffspring"),sQuery(id+"F0.wireOp",EDGE,"E36.trimOffspring"),sQuery(id+"F0.wireOp",EDGE,"E37.trimOffspring"),sQuery(id+"F0.wireOp",EDGE,"E38.trimOffspring"),sQuery(id+"F0.wireOp",EDGE,"E39.trimOffspring"),sQuery(id+"F0.wireOp",EDGE,"E40.trimOffspring"),sQuery(id+"F0.wireOp",EDGE,"E41.trimOffspring"),sQuery(id+"F0.wireOp",EDGE,"E44.trimOffspring"),sQuery(id+"F0.wireOp",EDGE,"E45.trimOffspring"),sQuery(id+"F0.wireOp",EDGE,"E46.trimOffspring"),sQuery(id+"F0.wireOp",EDGE,"E47.trimOffspring"),sQuery(id+"F0.wireOp",EDGE,"E48.trimOffspring"),sQuery(id+"F0.wireOp",EDGE,"E49.trimOffspring"),sQuery(id+"F0.wireOp",EDGE,"E50.trimOffspring"),sQuery(id+"F0.wireOp",EDGE,"E51.trimOffspring"),sQuery(id+"F0.wireOp",EDGE,"E52.trimOffspring"),sQuery(id+"F0.wireOp",EDGE,"E53.trimOffspring"),sQuery(id+"F0.wireOp",EDGE,"E54.trimOffspring"),sQuery(id+"F0.wireOp",EDGE,"E55.trimOffspring"),sQuery(id+"F0.wireOp",EDGE,"E56.trimOffspring"),sQuery(id+"F0.wireOp",EDGE,"E57.trimOffspring"),sQuery(id+"F0.wireOp",EDGE,"E58.trimOffspring"),sQuery(id+"F0.wireOp",EDGE,"E59.trimOffspring"),sQuery(id+"F0.wireOp",EDGE,"E60.trimOffspring"),sQuery(id+"F0.wireOp",EDGE,"E61.trimOffspring"),sQuery(id+"F0.wireOp",EDGE,"E62.trimOffspring"),sQuery(id+"F0.wireOp",EDGE,"E63.trimOffspring"),sQuery(id+"F0.wireOp",EDGE,"E64.trimOffspring"),sQuery(id+"F0.wireOp",EDGE,"E65.trimOffspring"),sQuery(id+"F0.wireOp",EDGE,"E66.trimOffspring"),sQuery(id+"F0.wireOp",EDGE,"E67.trimOffspring"),sQuery(id+"F0.wireOp",EDGE,"E68"),sQuery(id+"F0.wireOp",EDGE,"E69"),sQuery(id+"F0.wireOp",EDGE,"E70"),sQuery(id+"F0.wireOp",EDGE,"E71.trimOffspring"),sQuery(id+"F0.wireOp",EDGE,"E72"),sQuery(id+"F0.wireOp",EDGE,"E73"),sQuery(id+"F0.wireOp",EDGE,"E74"),sQuery(id+"F0.wireOp",EDGE,"E75")])],"isStart":false});
            var Q1;
            Q1=makeQuery(id+"F2.opExtrude","CAP_FACE",FACE,{"disambiguationData":[OSD([sQuery(id+"F0.wireOp",EDGE,"E4.4.0.0"),sQuery(id+"F0.wireOp",EDGE,"E4.4.1.1"),sQuery(id+"F0.wireOp",EDGE,"E4.4.1.15"),sQuery(id+"F0.wireOp",EDGE,"E5.right")])],"isStart":false});
            var Q2;
            Q2=makeQuery(id+"F2.opExtrude","CAP_FACE",FACE,{"disambiguationData":[OSD([sQuery(id+"F0.wireOp",EDGE,"E4.4.1.2"),sQuery(id+"F0.wireOp",EDGE,"E4.4.1.5"),sQuery(id+"F0.wireOp",EDGE,"E4.4.1.6"),sQuery(id+"F0.wireOp",EDGE,"E5.right")])],"isStart":false});
            var Q3;
            Q3=makeQuery(id+"F2.opExtrude","CAP_FACE",FACE,{"disambiguationData":[OSD([sQuery(id+"F0.wireOp",EDGE,"E4.3.0.0"),sQuery(id+"F0.wireOp",EDGE,"E4.3.0.11"),sQuery(id+"F0.wireOp",EDGE,"E4.3.1.1"),sQuery(id+"F0.wireOp",EDGE,"E4.3.1.11"),sQuery(id+"F0.wireOp",EDGE,"E4.4.0.0"),sQuery(id+"F0.wireOp",EDGE,"E4.4.0.13"),sQuery(id+"F0.wireOp",EDGE,"E4.4.1.1"),sQuery(id+"F0.wireOp",EDGE,"E4.4.1.7"),sQuery(id+"F0.wireOp",EDGE,"E4.4.1.8"),sQuery(id+"F0.wireOp",EDGE,"E4.4.1.9"),sQuery(id+"F0.wireOp",EDGE,"E4.4.1.10"),sQuery(id+"F0.wireOp",EDGE,"E4.4.1.13")])],"isStart":false});
            var Q4;
            Q4=makeQuery(id+"F2.opExtrude","CAP_FACE",FACE,{"disambiguationData":[OSD([sQuery(id+"F0.wireOp",EDGE,"E4.3.0.0"),sQuery(id+"F0.wireOp",EDGE,"E4.3.1.1"),sQuery(id+"F0.wireOp",EDGE,"E4.4.1.12"),sQuery(id+"F0.wireOp",EDGE,"E29.trimOffspring")])],"isStart":false});
            var Q5;
            Q5=makeQuery(id+"F2.opExtrude","CAP_FACE",FACE,{"disambiguationData":[OSD([sQuery(id+"F0.wireOp",EDGE,"E4.2.0.0"),sQuery(id+"F0.wireOp",EDGE,"E4.2.0.11"),sQuery(id+"F0.wireOp",EDGE,"E4.2.1.1"),sQuery(id+"F0.wireOp",EDGE,"E4.2.1.11"),sQuery(id+"F0.wireOp",EDGE,"E4.3.0.0"),sQuery(id+"F0.wireOp",EDGE,"E4.3.0.13"),sQuery(id+"F0.wireOp",EDGE,"E4.3.1.1"),sQuery(id+"F0.wireOp",EDGE,"E4.3.1.8"),sQuery(id+"F0.wireOp",EDGE,"E4.3.1.10"),sQuery(id+"F0.wireOp",EDGE,"E4.3.1.13"),sQuery(id+"F0.wireOp",EDGE,"E30.trimOffspring"),sQuery(id+"F0.wireOp",EDGE,"E41.trimOffspring")])],"isStart":false});
            var Q6;
            Q6=makeQuery(id+"F2.opExtrude","CAP_FACE",FACE,{"disambiguationData":[OSD([sQuery(id+"F0.wireOp",EDGE,"E4.2.0.0"),sQuery(id+"F0.wireOp",EDGE,"E4.2.1.1"),sQuery(id+"F0.wireOp",EDGE,"E4.2.1.15"),sQuery(id+"F0.wireOp",EDGE,"E4.3.1.12")])],"isStart":false});
            var Q7;
            Q7=makeQuery(id+"F2.opExtrude","CAP_FACE",FACE,{"disambiguationData":[OSD([sQuery(id+"F0.wireOp",EDGE,"E4.1.1.2"),sQuery(id+"F0.wireOp",EDGE,"E4.1.1.4"),sQuery(id+"F0.wireOp",EDGE,"E4.1.1.5"),sQuery(id+"F0.wireOp",EDGE,"E4.1.1.6"),sQuery(id+"F0.wireOp",EDGE,"E4.1.1.14"),sQuery(id+"F0.wireOp",EDGE,"E4.1.1.15"),sQuery(id+"F0.wireOp",EDGE,"E4.1.2.3"),sQuery(id+"F0.wireOp",EDGE,"E4.1.2.15"),sQuery(id+"F0.wireOp",EDGE,"E4.2.1.12"),sQuery(id+"F0.wireOp",EDGE,"E4.2.1.14"),sQuery(id+"F0.wireOp",EDGE,"E4.2.2.3"),sQuery(id+"F0.wireOp",EDGE,"E4.2.2.12")])],"isStart":false});
            var Q8;
            Q8=makeQuery(id+"F2.opExtrude","CAP_FACE",FACE,{"disambiguationData":[OSD([sQuery(id+"F0.wireOp",EDGE,"E4.1.0.0"),sQuery(id+"F0.wireOp",EDGE,"E4.1.1.1"),sQuery(id+"F0.wireOp",EDGE,"E4.1.1.15"),sQuery(id+"F0.wireOp",EDGE,"E4.2.1.12")])],"isStart":false});
            var Q9;
            Q9=makeQuery(id+"F2.opExtrude","CAP_FACE",FACE,{"disambiguationData":[OSD([sQuery(id+"F0.wireOp",EDGE,"E4.0.1.2"),sQuery(id+"F0.wireOp",EDGE,"E4.0.1.4"),sQuery(id+"F0.wireOp",EDGE,"E4.0.1.5"),sQuery(id+"F0.wireOp",EDGE,"E4.0.1.6"),sQuery(id+"F0.wireOp",EDGE,"E4.1.2.3"),sQuery(id+"F0.wireOp",EDGE,"E4.1.2.12")])],"isStart":false});
            var Q10;
            Q10=makeQuery(id+"F2.opExtrude","CAP_FACE",FACE,{"disambiguationData":[OSD([sQuery(id+"F0.wireOp",EDGE,"E4.1.2.8"),sQuery(id+"F0.wireOp",EDGE,"E4.1.2.10"),sQuery(id+"F0.wireOp",EDGE,"E31.trimOffspring"),sQuery(id+"F0.wireOp",EDGE,"E33.trimOffspring")])],"isStart":false});
            var Q11;
            Q11=makeQuery(id+"F2.opExtrude","CAP_FACE",FACE,{"disambiguationData":[OSD([sQuery(id+"F0.wireOp",EDGE,"E4.1.1.2"),sQuery(id+"F0.wireOp",EDGE,"E4.1.1.5"),sQuery(id+"F0.wireOp",EDGE,"E4.1.1.7"),sQuery(id+"F0.wireOp",EDGE,"E4.1.1.9")])],"isStart":false});
            var Q12;
            Q12=makeQuery(id+"F2.opExtrude","CAP_FACE",FACE,{"disambiguationData":[OSD([sQuery(id+"F0.wireOp",EDGE,"E4.1.1.2"),sQuery(id+"F0.wireOp",EDGE,"E4.1.1.4"),sQuery(id+"F0.wireOp",EDGE,"E4.2.1.8"),sQuery(id+"F0.wireOp",EDGE,"E4.2.1.9")])],"isStart":false});
            var Q13;
            Q13=makeQuery(id+"F2.opExtrude","CAP_FACE",FACE,{"disambiguationData":[OSD([sQuery(id+"F0.wireOp",EDGE,"E4.1.1.4"),sQuery(id+"F0.wireOp",EDGE,"E4.1.1.6"),sQuery(id+"F0.wireOp",EDGE,"E4.2.2.8"),sQuery(id+"F0.wireOp",EDGE,"E4.2.2.10")])],"isStart":false});
            var Q14;
            Q14=makeQuery(id+"F2.opExtrude","CAP_FACE",FACE,{"disambiguationData":[OSD([sQuery(id+"F0.wireOp",EDGE,"E4.3.2.8"),sQuery(id+"F0.wireOp",EDGE,"E4.3.2.10"),sQuery(id+"F0.wireOp",EDGE,"E36.trimOffspring"),sQuery(id+"F0.wireOp",EDGE,"E44.trimOffspring")])],"isStart":false});
            var Q15;
            Q15=makeQuery(id+"F2.opExtrude","CAP_FACE",FACE,{"disambiguationData":[OSD([sQuery(id+"F0.wireOp",EDGE,"E4.3.1.2"),sQuery(id+"F0.wireOp",EDGE,"E4.3.1.5"),sQuery(id+"F0.wireOp",EDGE,"E30.trimOffspring"),sQuery(id+"F0.wireOp",EDGE,"E41.trimOffspring")])],"isStart":false});
            var Q16;
            Q16=makeQuery(id+"F2.opExtrude","CAP_FACE",FACE,{"disambiguationData":[OSD([sQuery(id+"F0.wireOp",EDGE,"E4.3.1.2"),sQuery(id+"F0.wireOp",EDGE,"E4.3.1.4"),sQuery(id+"F0.wireOp",EDGE,"E4.4.1.8"),sQuery(id+"F0.wireOp",EDGE,"E4.4.1.9")])],"isStart":false});
            var Q17;
            Q17=makeQuery(id+"F2.opExtrude","CAP_FACE",FACE,{"disambiguationData":[OSD([sQuery(id+"F0.wireOp",EDGE,"E4.3.1.4"),sQuery(id+"F0.wireOp",EDGE,"E4.3.1.6"),sQuery(id+"F0.wireOp",EDGE,"E4.4.2.8"),sQuery(id+"F0.wireOp",EDGE,"E4.4.2.10")])],"isStart":false});
            var Q18;
            Q18=makeQuery(id+"F2.opExtrude","CAP_FACE",FACE,{"disambiguationData":[OSD([sQuery(id+"F0.wireOp",EDGE,"E4.3.1.0"),sQuery(id+"F0.wireOp",EDGE,"E4.3.1.11"),sQuery(id+"F0.wireOp",EDGE,"E4.3.2.11"),sQuery(id+"F0.wireOp",EDGE,"E4.4.1.0"),sQuery(id+"F0.wireOp",EDGE,"E4.4.1.13"),sQuery(id+"F0.wireOp",EDGE,"E4.4.2.1"),sQuery(id+"F0.wireOp",EDGE,"E4.4.2.7"),sQuery(id+"F0.wireOp",EDGE,"E4.4.2.8"),sQuery(id+"F0.wireOp",EDGE,"E4.4.2.9"),sQuery(id+"F0.wireOp",EDGE,"E4.4.2.10"),sQuery(id+"F0.wireOp",EDGE,"E4.4.2.13"),sQuery(id+"F0.wireOp",EDGE,"E46.trimOffspring")])],"isStart":false});
            var Q19;
            Q19=makeQuery(id+"F2.opExtrude","CAP_FACE",FACE,{"disambiguationData":[OSD([sQuery(id+"F0.wireOp",EDGE,"E4.3.1.0"),sQuery(id+"F0.wireOp",EDGE,"E4.3.2.15"),sQuery(id+"F0.wireOp",EDGE,"E4.4.2.12"),sQuery(id+"F0.wireOp",EDGE,"E46.trimOffspring")])],"isStart":false});
            var Q20;
            Q20=makeQuery(id+"F2.opExtrude","CAP_FACE",FACE,{"disambiguationData":[OSD([sQuery(id+"F0.wireOp",EDGE,"E4.3.2.7"),sQuery(id+"F0.wireOp",EDGE,"E4.3.2.8"),sQuery(id+"F0.wireOp",EDGE,"E4.3.2.9"),sQuery(id+"F0.wireOp",EDGE,"E37.trimOffspring"),sQuery(id+"F0.wireOp",EDGE,"E38.trimOffspring"),sQuery(id+"F0.wireOp",EDGE,"E45.trimOffspring")])],"isStart":false});
            var Q21;
            Q21=makeQuery(id+"F2.opExtrude","CAP_FACE",FACE,{"disambiguationData":[OSD([sQuery(id+"F0.wireOp",EDGE,"E4.2.1.0"),sQuery(id+"F0.wireOp",EDGE,"E4.2.2.1"),sQuery(id+"F0.wireOp",EDGE,"E4.2.2.15"),sQuery(id+"F0.wireOp",EDGE,"E4.3.2.12")])],"isStart":false});
            var Q22;
            Q22=makeQuery(id+"F2.opExtrude","CAP_FACE",FACE,{"disambiguationData":[OSD([sQuery(id+"F0.wireOp",EDGE,"E4.1.1.0"),sQuery(id+"F0.wireOp",EDGE,"E4.1.1.11"),sQuery(id+"F0.wireOp",EDGE,"E4.1.2.1"),sQuery(id+"F0.wireOp",EDGE,"E4.1.2.11"),sQuery(id+"F0.wireOp",EDGE,"E4.2.1.0"),sQuery(id+"F0.wireOp",EDGE,"E4.2.1.13"),sQuery(id+"F0.wireOp",EDGE,"E4.2.2.1"),sQuery(id+"F0.wireOp",EDGE,"E4.2.2.7"),sQuery(id+"F0.wireOp",EDGE,"E4.2.2.8"),sQuery(id+"F0.wireOp",EDGE,"E4.2.2.9"),sQuery(id+"F0.wireOp",EDGE,"E4.2.2.10"),sQuery(id+"F0.wireOp",EDGE,"E4.2.2.13")])],"isStart":false});
            var Q23;
            Q23=makeQuery(id+"F2.opExtrude","CAP_FACE",FACE,{"disambiguationData":[OSD([sQuery(id+"F0.wireOp",EDGE,"E4.1.1.11"),sQuery(id+"F0.wireOp",EDGE,"E4.2.1.13"),sQuery(id+"F0.wireOp",EDGE,"E4.2.1.14"),sQuery(id+"F0.wireOp",EDGE,"E4.2.2.3")])],"isStart":false});
            var Q24;
            Q24=makeQuery(id+"F2.opExtrude","CAP_FACE",FACE,{"disambiguationData":[OSD([sQuery(id+"F0.wireOp",EDGE,"E4.1.1.0"),sQuery(id+"F0.wireOp",EDGE,"E4.1.2.1"),sQuery(id+"F0.wireOp",EDGE,"E4.1.2.15"),sQuery(id+"F0.wireOp",EDGE,"E4.2.2.12")])],"isStart":false});
            var Q25;
            Q25=makeQuery(id+"F2.opExtrude","CAP_FACE",FACE,{"disambiguationData":[OSD([sQuery(id+"F0.wireOp",EDGE,"E4.1.2.7"),sQuery(id+"F0.wireOp",EDGE,"E4.1.2.8"),sQuery(id+"F0.wireOp",EDGE,"E4.1.2.9"),sQuery(id+"F0.wireOp",EDGE,"E4.1.2.10"),sQuery(id+"F0.wireOp",EDGE,"E32.trimOffspring"),sQuery(id+"F0.wireOp",EDGE,"E34.trimOffspring")])],"isStart":false});
            var Q26;
            Q26=makeQuery(id+"F2.opExtrude","CAP_FACE",FACE,{"disambiguationData":[OSD([sQuery(id+"F0.wireOp",EDGE,"E4.0.1.11"),sQuery(id+"F0.wireOp",EDGE,"E4.1.1.13"),sQuery(id+"F0.wireOp",EDGE,"E4.1.1.14"),sQuery(id+"F0.wireOp",EDGE,"E4.1.2.3")])],"isStart":false});
            var Q27;
            Q27=makeQuery(id+"F2.opExtrude","CAP_FACE",FACE,{"disambiguationData":[OSD([sQuery(id+"F0.wireOp",EDGE,"E4.0.1.0"),sQuery(id+"F0.wireOp",EDGE,"E4.0.2.1"),sQuery(id+"F0.wireOp",EDGE,"E4.0.2.15"),sQuery(id+"F0.wireOp",EDGE,"E4.1.2.12")])],"isStart":false});
            var Q28;
            Q28=makeQuery(id+"F2.opExtrude","CAP_FACE",FACE,{"disambiguationData":[OSD([sQuery(id+"F0.wireOp",EDGE,"E4.0.1.0"),sQuery(id+"F0.wireOp",EDGE,"E4.0.1.13"),sQuery(id+"F0.wireOp",EDGE,"E4.0.2.1"),sQuery(id+"F0.wireOp",EDGE,"E4.0.2.7"),sQuery(id+"F0.wireOp",EDGE,"E4.0.2.9"),sQuery(id+"F0.wireOp",EDGE,"E4.0.2.10"),sQuery(id+"F0.wireOp",EDGE,"E4.0.2.13"),sQuery(id+"F0.wireOp",EDGE,"E5.left")])],"isStart":false});
            var Q29;
            Q29=makeQuery(id+"F2.opExtrude","CAP_FACE",FACE,{"disambiguationData":[OSD([sQuery(id+"F0.wireOp",EDGE,"E4.0.2.14"),sQuery(id+"F0.wireOp",EDGE,"E4.0.3.3"),sQuery(id+"F0.wireOp",EDGE,"E5.left"),sQuery(id+"F0.wireOp",EDGE,"E74")])],"isStart":false});
            var Q30;
            Q30=makeQuery(id+"F2.opExtrude","CAP_FACE",FACE,{"disambiguationData":[OSD([sQuery(id+"F0.wireOp",EDGE,"E4.0.2.11"),sQuery(id+"F0.wireOp",EDGE,"E4.1.2.13"),sQuery(id+"F0.wireOp",EDGE,"E4.1.2.14"),sQuery(id+"F0.wireOp",EDGE,"E4.1.3.3")])],"isStart":false});
            var Q31;
            Q31=makeQuery(id+"F2.opExtrude","CAP_FACE",FACE,{"disambiguationData":[OSD([sQuery(id+"F0.wireOp",EDGE,"E4.1.2.2"),sQuery(id+"F0.wireOp",EDGE,"E4.1.2.4"),sQuery(id+"F0.wireOp",EDGE,"E4.1.2.14"),sQuery(id+"F0.wireOp",EDGE,"E4.1.2.15"),sQuery(id+"F0.wireOp",EDGE,"E4.1.3.3"),sQuery(id+"F0.wireOp",EDGE,"E4.1.3.15"),sQuery(id+"F0.wireOp",EDGE,"E4.2.2.12"),sQuery(id+"F0.wireOp",EDGE,"E4.2.2.14"),sQuery(id+"F0.wireOp",EDGE,"E4.2.3.3"),sQuery(id+"F0.wireOp",EDGE,"E4.2.3.12"),sQuery(id+"F0.wireOp",EDGE,"E35.trimOffspring"),sQuery(id+"F0.wireOp",EDGE,"E73")])],"isStart":false});
            var Q32;
            Q32=makeQuery(id+"F2.opExtrude","CAP_FACE",FACE,{"disambiguationData":[OSD([sQuery(id+"F0.wireOp",EDGE,"E4.1.2.2"),sQuery(id+"F0.wireOp",EDGE,"E4.1.2.4"),sQuery(id+"F0.wireOp",EDGE,"E4.1.2.14"),sQuery(id+"F0.wireOp",EDGE,"E4.1.2.15"),sQuery(id+"F0.wireOp",EDGE,"E4.1.3.3"),sQuery(id+"F0.wireOp",EDGE,"E4.1.3.15"),sQuery(id+"F0.wireOp",EDGE,"E4.2.2.12"),sQuery(id+"F0.wireOp",EDGE,"E4.2.2.14"),sQuery(id+"F0.wireOp",EDGE,"E4.2.3.3"),sQuery(id+"F0.wireOp",EDGE,"E4.2.3.12"),sQuery(id+"F0.wireOp",EDGE,"E35.trimOffspring"),sQuery(id+"F0.wireOp",EDGE,"E73")])],"isStart":true});
            var Q33;
            Q33=makeQuery(id+"F2.opExtrude","CAP_FACE",FACE,{"disambiguationData":[OSD([sQuery(id+"F0.wireOp",EDGE,"E4.1.2.11"),sQuery(id+"F0.wireOp",EDGE,"E4.2.2.13"),sQuery(id+"F0.wireOp",EDGE,"E4.2.2.14"),sQuery(id+"F0.wireOp",EDGE,"E4.2.3.3")])],"isStart":false});
            var Q34;
            Q34=makeQuery(id+"F2.opExtrude","CAP_FACE",FACE,{"disambiguationData":[OSD([sQuery(id+"F0.wireOp",EDGE,"E4.3.2.13"),sQuery(id+"F0.wireOp",EDGE,"E4.3.2.14"),sQuery(id+"F0.wireOp",EDGE,"E4.3.3.3"),sQuery(id+"F0.wireOp",EDGE,"E48.trimOffspring")])],"isStart":false});
            var Q35;
            Q35=makeQuery(id+"F2.opExtrude","CAP_FACE",FACE,{"disambiguationData":[OSD([sQuery(id+"F0.wireOp",EDGE,"E4.3.2.4"),sQuery(id+"F0.wireOp",EDGE,"E4.3.2.5"),sQuery(id+"F0.wireOp",EDGE,"E4.3.2.14"),sQuery(id+"F0.wireOp",EDGE,"E4.3.2.15"),sQuery(id+"F0.wireOp",EDGE,"E4.3.3.3"),sQuery(id+"F0.wireOp",EDGE,"E4.3.3.15"),sQuery(id+"F0.wireOp",EDGE,"E4.4.2.12"),sQuery(id+"F0.wireOp",EDGE,"E4.4.2.14"),sQuery(id+"F0.wireOp",EDGE,"E4.4.3.3"),sQuery(id+"F0.wireOp",EDGE,"E4.4.3.12"),sQuery(id+"F0.wireOp",EDGE,"E47.trimOffspring"),sQuery(id+"F0.wireOp",EDGE,"E69")])],"isStart":false});
            var Q36;
            Q36=makeQuery(id+"F2.opExtrude","CAP_FACE",FACE,{"disambiguationData":[OSD([sQuery(id+"F0.wireOp",EDGE,"E4.3.2.11"),sQuery(id+"F0.wireOp",EDGE,"E4.4.2.13"),sQuery(id+"F0.wireOp",EDGE,"E4.4.2.14"),sQuery(id+"F0.wireOp",EDGE,"E4.4.3.3")])],"isStart":false});
            var Q37;
            Q37=makeQuery(id+"F2.opExtrude","CAP_FACE",FACE,{"disambiguationData":[OSD([sQuery(id+"F0.wireOp",EDGE,"E4.4.2.2"),sQuery(id+"F0.wireOp",EDGE,"E4.4.2.14"),sQuery(id+"F0.wireOp",EDGE,"E4.4.3.3"),sQuery(id+"F0.wireOp",EDGE,"E4.4.3.15"),sQuery(id+"F0.wireOp",EDGE,"E5.right"),sQuery(id+"F0.wireOp",EDGE,"E62.trimOffspring"),sQuery(id+"F0.wireOp",EDGE,"E71.trimOffspring"),sQuery(id+"F0.wireOp",EDGE,"E75")])],"isStart":false});
            var Q38;
            Q38=makeQuery(id+"F2.opExtrude","CAP_FACE",FACE,{"disambiguationData":[OSD([sQuery(id+"F0.wireOp",EDGE,"E4.4.2.2"),sQuery(id+"F0.wireOp",EDGE,"E4.4.2.5"),sQuery(id+"F0.wireOp",EDGE,"E4.4.2.7"),sQuery(id+"F0.wireOp",EDGE,"E4.4.2.9")])],"isStart":false});
            var Q39;
            Q39=makeQuery(id+"F2.opExtrude","CAP_FACE",FACE,{"disambiguationData":[OSD([sQuery(id+"F0.wireOp",EDGE,"E4.3.2.4"),sQuery(id+"F0.wireOp",EDGE,"E4.4.2.8"),sQuery(id+"F0.wireOp",EDGE,"E4.4.2.9"),sQuery(id+"F0.wireOp",EDGE,"E47.trimOffspring")])],"isStart":false});
            var Q40;
            Q40=makeQuery(id+"F2.opExtrude","CAP_FACE",FACE,{"disambiguationData":[OSD([sQuery(id+"F0.wireOp",EDGE,"E4.3.2.5"),sQuery(id+"F0.wireOp",EDGE,"E4.3.2.6"),sQuery(id+"F0.wireOp",EDGE,"E4.3.3.7"),sQuery(id+"F0.wireOp",EDGE,"E4.3.3.10")])],"isStart":false});
            var Q41;
            Q41=makeQuery(id+"F2.opExtrude","CAP_FACE",FACE,{"disambiguationData":[OSD([sQuery(id+"F0.wireOp",EDGE,"E4.3.3.8"),sQuery(id+"F0.wireOp",EDGE,"E4.3.3.10"),sQuery(id+"F0.wireOp",EDGE,"E49.trimOffspring"),sQuery(id+"F0.wireOp",EDGE,"E54.trimOffspring")])],"isStart":false});
            var Q42;
            Q42=makeQuery(id+"F2.opExtrude","CAP_FACE",FACE,{"disambiguationData":[OSD([sQuery(id+"F0.wireOp",EDGE,"E4.2.2.2"),sQuery(id+"F0.wireOp",EDGE,"E4.2.2.5"),sQuery(id+"F0.wireOp",EDGE,"E4.2.2.7"),sQuery(id+"F0.wireOp",EDGE,"E4.2.2.9")])],"isStart":false});
            var Q43;
            Q43=makeQuery(id+"F2.opExtrude","CAP_FACE",FACE,{"disambiguationData":[OSD([sQuery(id+"F0.wireOp",EDGE,"E4.1.2.2"),sQuery(id+"F0.wireOp",EDGE,"E4.1.2.4"),sQuery(id+"F0.wireOp",EDGE,"E4.2.2.8"),sQuery(id+"F0.wireOp",EDGE,"E4.2.2.9")])],"isStart":false});
            var Q44;
            Q44=makeQuery(id+"F2.opExtrude","CAP_FACE",FACE,{"disambiguationData":[OSD([sQuery(id+"F0.wireOp",EDGE,"E4.1.2.6"),sQuery(id+"F0.wireOp",EDGE,"E4.1.3.7"),sQuery(id+"F0.wireOp",EDGE,"E4.1.3.10"),sQuery(id+"F0.wireOp",EDGE,"E35.trimOffspring")])],"isStart":false});
            var Q45;
            Q45=makeQuery(id+"F2.opExtrude","CAP_FACE",FACE,{"disambiguationData":[OSD([sQuery(id+"F0.wireOp",EDGE,"E4.0.2.4"),sQuery(id+"F0.wireOp",EDGE,"E4.0.2.6"),sQuery(id+"F0.wireOp",EDGE,"E4.1.3.8"),sQuery(id+"F0.wireOp",EDGE,"E4.1.3.10")])],"isStart":false});
            var Q46;
            Q46=makeQuery(id+"F2.opExtrude","CAP_FACE",FACE,{"disambiguationData":[OSD([sQuery(id+"F0.wireOp",EDGE,"E4.0.2.2"),sQuery(id+"F0.wireOp",EDGE,"E4.0.2.5"),sQuery(id+"F0.wireOp",EDGE,"E4.0.2.7"),sQuery(id+"F0.wireOp",EDGE,"E4.0.2.9")])],"isStart":false});
            var Q47;
            Q47=makeQuery(id+"F2.opExtrude","CAP_FACE",FACE,{"disambiguationData":[OSD([sQuery(id+"F0.wireOp",EDGE,"E4.0.3.13"),sQuery(id+"F0.wireOp",EDGE,"E4.0.3.14"),sQuery(id+"F0.wireOp",EDGE,"E5.top"),sQuery(id+"F0.wireOp",EDGE,"E5.left")])],"isStart":false});
            var Q48;
            Q48=makeQuery(id+"F2.opExtrude","CAP_FACE",FACE,{"disambiguationData":[OSD([sQuery(id+"F0.wireOp",EDGE,"E4.0.3.2"),sQuery(id+"F0.wireOp",EDGE,"E4.0.3.5"),sQuery(id+"F0.wireOp",EDGE,"E50.trimOffspring"),sQuery(id+"F0.wireOp",EDGE,"E52.trimOffspring")])],"isStart":false});
            var Q49;
            Q49=makeQuery(id+"F2.opExtrude","CAP_FACE",FACE,{"disambiguationData":[OSD([sQuery(id+"F0.wireOp",EDGE,"E4.0.3.11"),sQuery(id+"F0.wireOp",EDGE,"E4.1.3.13"),sQuery(id+"F0.wireOp",EDGE,"E4.1.3.14"),sQuery(id+"F0.wireOp",EDGE,"E5.top")])],"isStart":false});
            var Q50;
            Q50=makeQuery(id+"F2.opExtrude","CAP_FACE",FACE,{"disambiguationData":[OSD([sQuery(id+"F0.wireOp",EDGE,"E4.1.3.2"),sQuery(id+"F0.wireOp",EDGE,"E4.1.3.4"),sQuery(id+"F0.wireOp",EDGE,"E4.1.3.5"),sQuery(id+"F0.wireOp",EDGE,"E4.1.3.14"),sQuery(id+"F0.wireOp",EDGE,"E4.1.3.15"),sQuery(id+"F0.wireOp",EDGE,"E4.2.3.12"),sQuery(id+"F0.wireOp",EDGE,"E4.2.3.14"),sQuery(id+"F0.wireOp",EDGE,"E5.top")])],"isStart":false});
            var Q51;
            Q51=makeQuery(id+"F2.opExtrude","CAP_FACE",FACE,{"disambiguationData":[OSD([sQuery(id+"F0.wireOp",EDGE,"E4.1.3.1"),sQuery(id+"F0.wireOp",EDGE,"E4.1.3.15"),sQuery(id+"F0.wireOp",EDGE,"E4.2.3.12"),sQuery(id+"F0.wireOp",EDGE,"E72")])],"isStart":false});
            var Q52;
            Q52=makeQuery(id+"F2.opExtrude","CAP_FACE",FACE,{"disambiguationData":[OSD([sQuery(id+"F0.wireOp",EDGE,"E4.1.3.2"),sQuery(id+"F0.wireOp",EDGE,"E4.1.3.5"),sQuery(id+"F0.wireOp",EDGE,"E4.1.3.7"),sQuery(id+"F0.wireOp",EDGE,"E4.1.3.9")])],"isStart":false});
            var Q53;
            Q53=makeQuery(id+"F2.opExtrude","CAP_FACE",FACE,{"disambiguationData":[OSD([sQuery(id+"F0.wireOp",EDGE,"E4.1.3.11"),sQuery(id+"F0.wireOp",EDGE,"E4.2.3.13"),sQuery(id+"F0.wireOp",EDGE,"E4.2.3.14"),sQuery(id+"F0.wireOp",EDGE,"E5.top")])],"isStart":false});
            var Q54;
            Q54=makeQuery(id+"F2.opExtrude","CAP_FACE",FACE,{"disambiguationData":[OSD([sQuery(id+"F0.wireOp",EDGE,"E4.2.3.2"),sQuery(id+"F0.wireOp",EDGE,"E4.2.3.4"),sQuery(id+"F0.wireOp",EDGE,"E4.2.3.5"),sQuery(id+"F0.wireOp",EDGE,"E5.top"),sQuery(id+"F0.wireOp",EDGE,"E57.trimOffspring"),sQuery(id+"F0.wireOp",EDGE,"E59.trimOffspring")])],"isStart":false});
            var Q55;
            Q55=makeQuery(id+"F2.opExtrude","CAP_FACE",FACE,{"disambiguationData":[OSD([sQuery(id+"F0.wireOp",EDGE,"E4.2.3.2"),sQuery(id+"F0.wireOp",EDGE,"E4.2.3.5"),sQuery(id+"F0.wireOp",EDGE,"E56.trimOffspring"),sQuery(id+"F0.wireOp",EDGE,"E58.trimOffspring")])],"isStart":false});
            var Q56;
            Q56=makeQuery(id+"F2.opExtrude","CAP_FACE",FACE,{"disambiguationData":[OSD([sQuery(id+"F0.wireOp",EDGE,"E4.2.3.11"),sQuery(id+"F0.wireOp",EDGE,"E4.3.3.13"),sQuery(id+"F0.wireOp",EDGE,"E5.top"),sQuery(id+"F0.wireOp",EDGE,"E61.trimOffspring")])],"isStart":false});
            var Q57;
            Q57=makeQuery(id+"F2.opExtrude","CAP_FACE",FACE,{"disambiguationData":[OSD([sQuery(id+"F0.wireOp",EDGE,"E4.3.3.4"),sQuery(id+"F0.wireOp",EDGE,"E4.3.3.5"),sQuery(id+"F0.wireOp",EDGE,"E4.3.3.15"),sQuery(id+"F0.wireOp",EDGE,"E4.4.3.12"),sQuery(id+"F0.wireOp",EDGE,"E4.4.3.14"),sQuery(id+"F0.wireOp",EDGE,"E5.top"),sQuery(id+"F0.wireOp",EDGE,"E61.trimOffspring"),sQuery(id+"F0.wireOp",EDGE,"E68")])],"isStart":false});
            var Q58;
            Q58=makeQuery(id+"F2.opExtrude","CAP_FACE",FACE,{"disambiguationData":[OSD([sQuery(id+"F0.wireOp",EDGE,"E4.3.3.2"),sQuery(id+"F0.wireOp",EDGE,"E4.3.3.5"),sQuery(id+"F0.wireOp",EDGE,"E4.3.3.7"),sQuery(id+"F0.wireOp",EDGE,"E60.trimOffspring")])],"isStart":false});
            var Q59;
            Q59=makeQuery(id+"F2.opExtrude","CAP_FACE",FACE,{"disambiguationData":[OSD([sQuery(id+"F0.wireOp",EDGE,"E4.3.3.11"),sQuery(id+"F0.wireOp",EDGE,"E4.4.3.13"),sQuery(id+"F0.wireOp",EDGE,"E4.4.3.14"),sQuery(id+"F0.wireOp",EDGE,"E5.top")])],"isStart":false});
            var Q60;
            Q60=makeQuery(id+"F2.opExtrude","CAP_FACE",FACE,{"disambiguationData":[OSD([sQuery(id+"F0.wireOp",EDGE,"E4.4.3.2"),sQuery(id+"F0.wireOp",EDGE,"E4.4.3.5"),sQuery(id+"F0.wireOp",EDGE,"E5.top"),sQuery(id+"F0.wireOp",EDGE,"E5.right"),sQuery(id+"F0.wireOp",EDGE,"E65.trimOffspring"),sQuery(id+"F0.wireOp",EDGE,"E67.trimOffspring")])],"isStart":false});
            var Q61;
            Q61=makeQuery(id+"F2.opExtrude","CAP_FACE",FACE,{"disambiguationData":[OSD([sQuery(id+"F0.wireOp",EDGE,"E4.4.3.2"),sQuery(id+"F0.wireOp",EDGE,"E4.4.3.5"),sQuery(id+"F0.wireOp",EDGE,"E64.trimOffspring"),sQuery(id+"F0.wireOp",EDGE,"E66.trimOffspring")])],"isStart":false});
            var Q62;
            Q62=makeQuery(id+"F2.opExtrude","CAP_FACE",FACE,{"disambiguationData":[OSD([sQuery(id+"F0.wireOp",EDGE,"E3.1"),sQuery(id+"F0.wireOp",EDGE,"E3.2"),sQuery(id+"F0.wireOp",EDGE,"E4.0.1.1"),sQuery(id+"F0.wireOp",EDGE,"E4.0.1.7"),sQuery(id+"F0.wireOp",EDGE,"E4.0.1.9"),sQuery(id+"F0.wireOp",EDGE,"E4.0.1.10"),sQuery(id+"F0.wireOp",EDGE,"E4.0.1.13"),sQuery(id+"F0.wireOp",EDGE,"E5.left")])],"isStart":true});
            var Q63;
            Q63=makeQuery(id+"F2.opExtrude","CAP_FACE",FACE,{"disambiguationData":[OSD([sQuery(id+"F0.wireOp",EDGE,"E3.2"),sQuery(id+"F0.wireOp",EDGE,"E4.0.1.1"),sQuery(id+"F0.wireOp",EDGE,"E4.0.1.15"),sQuery(id+"F0.wireOp",EDGE,"E4.1.1.12")])],"isStart":true});
            var Q64;
            Q64=makeQuery(id+"F2.opExtrude","CAP_FACE",FACE,{"disambiguationData":[OSD([sQuery(id+"F0.wireOp",EDGE,"E3.2"),sQuery(id+"F0.wireOp",EDGE,"E3.3"),sQuery(id+"F0.wireOp",EDGE,"E4.0.1.1"),sQuery(id+"F0.wireOp",EDGE,"E4.0.1.11"),sQuery(id+"F0.wireOp",EDGE,"E4.1.0.0"),sQuery(id+"F0.wireOp",EDGE,"E4.1.1.1"),sQuery(id+"F0.wireOp",EDGE,"E4.1.1.7"),sQuery(id+"F0.wireOp",EDGE,"E4.1.1.8"),sQuery(id+"F0.wireOp",EDGE,"E4.1.1.9"),sQuery(id+"F0.wireOp",EDGE,"E4.1.1.10"),sQuery(id+"F0.wireOp",EDGE,"E4.1.1.13"),sQuery(id+"F0.wireOp",EDGE,"E17.trimOffspring")])],"isStart":true});
            var Q65;
            Q65=makeQuery(id+"F2.opExtrude","CAP_FACE",FACE,{"disambiguationData":[OSD([sQuery(id+"F0.wireOp",EDGE,"E4.0.1.13"),sQuery(id+"F0.wireOp",EDGE,"E4.0.1.14"),sQuery(id+"F0.wireOp",EDGE,"E5.left"),sQuery(id+"F0.wireOp",EDGE,"E70")])],"isStart":true});
            var Q66;
            Q66=makeQuery(id+"F2.opExtrude","CAP_FACE",FACE,{"disambiguationData":[OSD([sQuery(id+"F0.wireOp",EDGE,"E4.1.0.0"),sQuery(id+"F0.wireOp",EDGE,"E4.1.0.11"),sQuery(id+"F0.wireOp",EDGE,"E4.1.1.1"),sQuery(id+"F0.wireOp",EDGE,"E4.1.1.11"),sQuery(id+"F0.wireOp",EDGE,"E4.2.0.0"),sQuery(id+"F0.wireOp",EDGE,"E4.2.0.13"),sQuery(id+"F0.wireOp",EDGE,"E4.2.1.1"),sQuery(id+"F0.wireOp",EDGE,"E4.2.1.7"),sQuery(id+"F0.wireOp",EDGE,"E4.2.1.8"),sQuery(id+"F0.wireOp",EDGE,"E4.2.1.9"),sQuery(id+"F0.wireOp",EDGE,"E4.2.1.10"),sQuery(id+"F0.wireOp",EDGE,"E4.2.1.13")])],"isStart":true});
            var Q67;
            Q67=makeQuery(id+"F2.opExtrude","CAP_FACE",FACE,{"disambiguationData":[OSD([sQuery(id+"F0.wireOp",EDGE,"E4.2.1.2"),sQuery(id+"F0.wireOp",EDGE,"E4.2.1.4"),sQuery(id+"F0.wireOp",EDGE,"E4.2.1.5"),sQuery(id+"F0.wireOp",EDGE,"E4.2.1.6"),sQuery(id+"F0.wireOp",EDGE,"E4.3.2.3"),sQuery(id+"F0.wireOp",EDGE,"E4.3.2.12")])],"isStart":true});
            var Q68;
            Q68=makeQuery(id+"F2.opExtrude","CAP_FACE",FACE,{"disambiguationData":[OSD([sQuery(id+"F0.wireOp",EDGE,"E4.2.3.1"),sQuery(id+"F0.wireOp",EDGE,"E4.2.3.7"),sQuery(id+"F0.wireOp",EDGE,"E4.2.3.8"),sQuery(id+"F0.wireOp",EDGE,"E4.2.3.9"),sQuery(id+"F0.wireOp",EDGE,"E4.2.3.10"),sQuery(id+"F0.wireOp",EDGE,"E4.2.3.13")])],"isStart":true});
            var Q69;
            Q69=makeQuery(id+"F2.opExtrude","CAP_FACE",FACE,{"disambiguationData":[OSD([sQuery(id+"F0.wireOp",EDGE,"E4.0.2.0"),sQuery(id+"F0.wireOp",EDGE,"E4.0.2.11"),sQuery(id+"F0.wireOp",EDGE,"E4.0.3.1"),sQuery(id+"F0.wireOp",EDGE,"E4.0.3.11"),sQuery(id+"F0.wireOp",EDGE,"E4.1.2.0"),sQuery(id+"F0.wireOp",EDGE,"E4.1.2.13"),sQuery(id+"F0.wireOp",EDGE,"E4.1.3.1"),sQuery(id+"F0.wireOp",EDGE,"E4.1.3.7"),sQuery(id+"F0.wireOp",EDGE,"E4.1.3.8"),sQuery(id+"F0.wireOp",EDGE,"E4.1.3.9"),sQuery(id+"F0.wireOp",EDGE,"E4.1.3.10"),sQuery(id+"F0.wireOp",EDGE,"E4.1.3.13")])],"isStart":true});
            var Q70;
            Q70=makeQuery(id+"F2.opExtrude","CAP_FACE",FACE,{"disambiguationData":[OSD([sQuery(id+"F0.wireOp",EDGE,"E4.0.2.0"),sQuery(id+"F0.wireOp",EDGE,"E4.0.3.1"),sQuery(id+"F0.wireOp",EDGE,"E4.0.3.15"),sQuery(id+"F0.wireOp",EDGE,"E4.1.3.12")])],"isStart":true});
            var Q71;
            Q71=makeQuery(id+"F2.opExtrude","CAP_FACE",FACE,{"disambiguationData":[OSD([sQuery(id+"F0.wireOp",EDGE,"E4.0.3.1"),sQuery(id+"F0.wireOp",EDGE,"E4.0.3.7"),sQuery(id+"F0.wireOp",EDGE,"E4.0.3.9"),sQuery(id+"F0.wireOp",EDGE,"E4.0.3.10"),sQuery(id+"F0.wireOp",EDGE,"E4.0.3.13"),sQuery(id+"F0.wireOp",EDGE,"E5.left")])],"isStart":true});
            var Q72;
            Q72=makeQuery(id+"F2.opExtrude","CAP_FACE",FACE,{"disambiguationData":[OSD([sQuery(id+"F0.wireOp",EDGE,"E4.0.2.2"),sQuery(id+"F0.wireOp",EDGE,"E4.0.2.4"),sQuery(id+"F0.wireOp",EDGE,"E4.0.2.5"),sQuery(id+"F0.wireOp",EDGE,"E4.0.2.6"),sQuery(id+"F0.wireOp",EDGE,"E4.0.2.14"),sQuery(id+"F0.wireOp",EDGE,"E4.0.2.15"),sQuery(id+"F0.wireOp",EDGE,"E4.0.3.3"),sQuery(id+"F0.wireOp",EDGE,"E4.0.3.15"),sQuery(id+"F0.wireOp",EDGE,"E4.1.2.12"),sQuery(id+"F0.wireOp",EDGE,"E4.1.2.14"),sQuery(id+"F0.wireOp",EDGE,"E4.1.3.3"),sQuery(id+"F0.wireOp",EDGE,"E4.1.3.12")])],"isStart":true});
            var Q73;
            Q73=makeQuery(id+"F2.opExtrude","CAP_FACE",FACE,{"disambiguationData":[OSD([sQuery(id+"F0.wireOp",EDGE,"E4.2.2.2"),sQuery(id+"F0.wireOp",EDGE,"E4.2.2.5"),sQuery(id+"F0.wireOp",EDGE,"E4.2.2.14"),sQuery(id+"F0.wireOp",EDGE,"E4.2.2.15"),sQuery(id+"F0.wireOp",EDGE,"E4.2.3.3"),sQuery(id+"F0.wireOp",EDGE,"E4.2.3.15"),sQuery(id+"F0.wireOp",EDGE,"E4.3.2.12"),sQuery(id+"F0.wireOp",EDGE,"E4.3.2.14"),sQuery(id+"F0.wireOp",EDGE,"E4.3.3.3"),sQuery(id+"F0.wireOp",EDGE,"E4.3.3.12"),sQuery(id+"F0.wireOp",EDGE,"E49.trimOffspring"),sQuery(id+"F0.wireOp",EDGE,"E54.trimOffspring")])],"isStart":true});
            var Q74;
            Q74=makeQuery(id+"F2.opExtrude","CAP_FACE",FACE,{"disambiguationData":[OSD([sQuery(id+"F0.wireOp",EDGE,"E4.2.3.1"),sQuery(id+"F0.wireOp",EDGE,"E4.2.3.11"),sQuery(id+"F0.wireOp",EDGE,"E4.3.2.0"),sQuery(id+"F0.wireOp",EDGE,"E4.3.2.13"),sQuery(id+"F0.wireOp",EDGE,"E4.3.3.1"),sQuery(id+"F0.wireOp",EDGE,"E4.3.3.7"),sQuery(id+"F0.wireOp",EDGE,"E4.3.3.8"),sQuery(id+"F0.wireOp",EDGE,"E4.3.3.10"),sQuery(id+"F0.wireOp",EDGE,"E4.3.3.13"),sQuery(id+"F0.wireOp",EDGE,"E48.trimOffspring"),sQuery(id+"F0.wireOp",EDGE,"E55.trimOffspring"),sQuery(id+"F0.wireOp",EDGE,"E60.trimOffspring")])],"isStart":true});
            var Q75;
            Q75=makeQuery(id+"F2.opExtrude","CAP_FACE",FACE,{"disambiguationData":[OSD([sQuery(id+"F0.wireOp",EDGE,"E4.3.2.0"),sQuery(id+"F0.wireOp",EDGE,"E4.3.3.1"),sQuery(id+"F0.wireOp",EDGE,"E4.3.3.15"),sQuery(id+"F0.wireOp",EDGE,"E4.4.3.12")])],"isStart":true});
            var Q76;
            Q76=makeQuery(id+"F2.opExtrude","CAP_FACE",FACE,{"disambiguationData":[OSD([sQuery(id+"F0.wireOp",EDGE,"E4.4.3.1"),sQuery(id+"F0.wireOp",EDGE,"E4.4.3.15"),sQuery(id+"F0.wireOp",EDGE,"E5.right"),sQuery(id+"F0.wireOp",EDGE,"E63.trimOffspring")])],"isStart":true});
            var Q77;
            Q77=makeQuery(id+"F2.opExtrude","CAP_FACE",FACE,{"disambiguationData":[OSD([sQuery(id+"F0.wireOp",EDGE,"E4.2.1.11"),sQuery(id+"F0.wireOp",EDGE,"E4.3.1.13"),sQuery(id+"F0.wireOp",EDGE,"E39.trimOffspring"),sQuery(id+"F0.wireOp",EDGE,"E40.trimOffspring")])],"isStart":true});
            var Q78;
            Q78=makeQuery(id+"F2.opExtrude","CAP_FACE",FACE,{"disambiguationData":[OSD([sQuery(id+"F0.wireOp",EDGE,"E4.3.1.2"),sQuery(id+"F0.wireOp",EDGE,"E4.3.1.4"),sQuery(id+"F0.wireOp",EDGE,"E4.3.1.5"),sQuery(id+"F0.wireOp",EDGE,"E4.3.1.6"),sQuery(id+"F0.wireOp",EDGE,"E4.3.2.15"),sQuery(id+"F0.wireOp",EDGE,"E4.4.1.12"),sQuery(id+"F0.wireOp",EDGE,"E4.4.1.14"),sQuery(id+"F0.wireOp",EDGE,"E4.4.2.3"),sQuery(id+"F0.wireOp",EDGE,"E4.4.2.12"),sQuery(id+"F0.wireOp",EDGE,"E29.trimOffspring"),sQuery(id+"F0.wireOp",EDGE,"E39.trimOffspring"),sQuery(id+"F0.wireOp",EDGE,"E40.trimOffspring")])],"isStart":true});
            var Q79;
            Q79=makeQuery(id+"F2.opExtrude","CAP_FACE",FACE,{"disambiguationData":[OSD([sQuery(id+"F0.wireOp",EDGE,"E4.3.1.11"),sQuery(id+"F0.wireOp",EDGE,"E4.4.1.13"),sQuery(id+"F0.wireOp",EDGE,"E4.4.1.14"),sQuery(id+"F0.wireOp",EDGE,"E4.4.2.3")])],"isStart":true});
            var Q80;
            Q80=makeQuery(id+"F2.opExtrude","CAP_FACE",FACE,{"disambiguationData":[OSD([sQuery(id+"F0.wireOp",EDGE,"E4.4.1.0"),sQuery(id+"F0.wireOp",EDGE,"E4.4.2.1"),sQuery(id+"F0.wireOp",EDGE,"E5.right"),sQuery(id+"F0.wireOp",EDGE,"E71.trimOffspring")])],"isStart":true});
            var Q81;
            Q81=makeQuery(id+"F2.opExtrude","CAP_FACE",FACE,{"disambiguationData":[OSD([sQuery(id+"F0.wireOp",EDGE,"E4.4.3.1"),sQuery(id+"F0.wireOp",EDGE,"E4.4.3.7"),sQuery(id+"F0.wireOp",EDGE,"E4.4.3.8"),sQuery(id+"F0.wireOp",EDGE,"E4.4.3.9"),sQuery(id+"F0.wireOp",EDGE,"E4.4.3.10"),sQuery(id+"F0.wireOp",EDGE,"E4.4.3.13")])],"isStart":true});
            var Q82;
            Q82=makeQuery(id+"F2.opExtrude","CAP_FACE",FACE,{"disambiguationData":[OSD([sQuery(id+"F0.wireOp",EDGE,"E4.2.3.1"),sQuery(id+"F0.wireOp",EDGE,"E4.2.3.15"),sQuery(id+"F0.wireOp",EDGE,"E4.3.3.12"),sQuery(id+"F0.wireOp",EDGE,"E55.trimOffspring")])],"isStart":true});
            var Q83;
            Q83=makeQuery(id+"F2.opExtrude","CAP_FACE",FACE,{"disambiguationData":[OSD([sQuery(id+"F0.wireOp",EDGE,"E4.0.3.2"),sQuery(id+"F0.wireOp",EDGE,"E4.0.3.4"),sQuery(id+"F0.wireOp",EDGE,"E4.0.3.5"),sQuery(id+"F0.wireOp",EDGE,"E5.top"),sQuery(id+"F0.wireOp",EDGE,"E51.trimOffspring"),sQuery(id+"F0.wireOp",EDGE,"E53.trimOffspring")])],"isStart":true});
            extrude(context, id + "F3", {"entities" : qUnion([Q0, Q1, Q2, Q3, Q4, Q5, Q6, Q7, Q8, Q9, Q10, Q11, Q12, Q13, Q14, Q15, Q16, Q17, Q18, Q19, Q20, Q21, Q22, Q23, Q24, Q25, Q26, Q27, Q28, Q29, Q30, Q31, Q32, Q33, Q34, Q35, Q36, Q37, Q38, Q39, Q40, Q41, Q42, Q43, Q44, Q45, Q46, Q47, Q48, Q49, Q50, Q51, Q52, Q53, Q54, Q55, Q56, Q57, Q58, Q59, Q60, Q61, Q62, Q63, Q64, Q65, Q66, Q67, Q68, Q69, Q70, Q71, Q72, Q73, Q74, Q75, Q76, Q77, Q78, Q79, Q80, Q81, Q82, Q83]), "oppositeDirection" : true, "depth" : 25.4 * mm, "offsetDistance" : 25.4 * mm});
        }
    });
